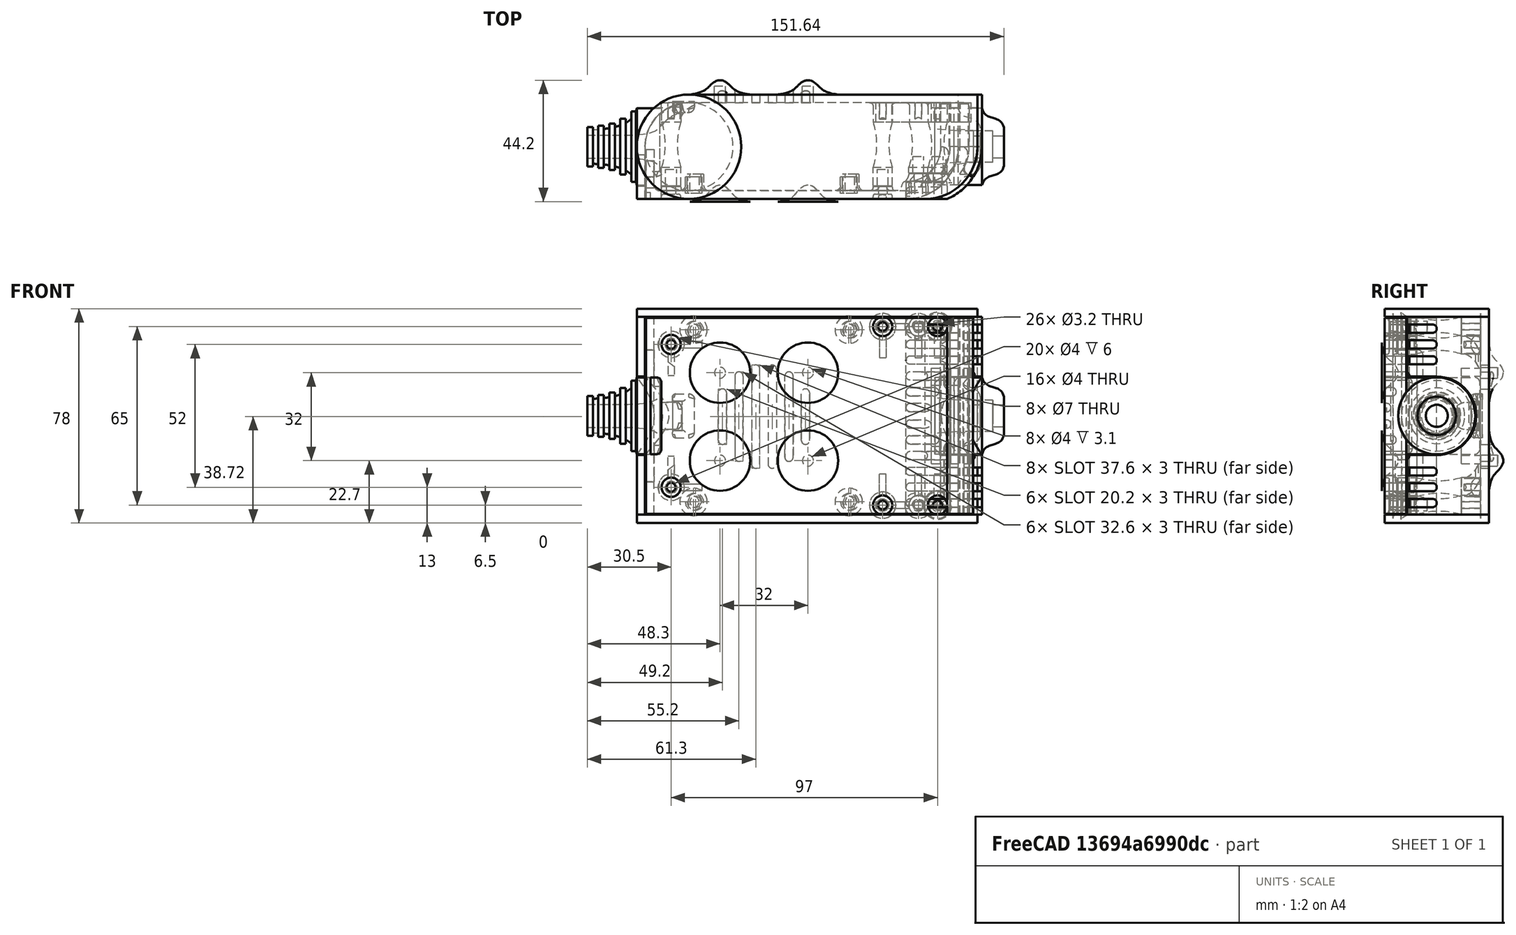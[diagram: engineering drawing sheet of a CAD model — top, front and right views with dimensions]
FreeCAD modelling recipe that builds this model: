
FCSTD DOCUMENT  (FreeCAD 0.19R0.19.2)
Label: enclosure_161
License: All rights reserved
LicenseURL: http://en.wikipedia.org/wiki/All_rights_reserved
objects: Part::Feature×140, Part::Revolution×140, Part::MultiFuse×120, Sketcher::SketchObject×67, Part::Extrusion×52, Part::Fillet×51, Part::Cut×51, Part::Cylinder×50, Part::Box×33, App::MeasureDistance×4
note: 704 computed .brp shape members not serialized (recipe doc carries the construction recipe); baked Part::Feature solids carry a one-line shape summary decoded from their .brp

FEATURE [Sketcher::SketchObject] Sketch  label="topSketch"
  FullyConstrained = true
  sketch-geometry (20):
    g0: LineSegment StartX=5.21097e-06 StartY=3 StartZ=0 EndX=5.21097e-06 EndY=19 EndZ=0
    g1: ArcOfCircle CenterX=19 CenterY=19 CenterZ=0 NormalX=0 NormalY=0 NormalZ=1 AngleXU=0 Radius=19 StartAngle=1.5708 EndAngle=3.14159
    g2: ArcOfCircle CenterX=19 CenterY=19 CenterZ=0 NormalX=0 NormalY=0 NormalZ=1 AngleXU=0 Radius=16 StartAngle=1.5708 EndAngle=3.14159
    g3: LineSegment StartX=114 StartY=35 StartZ=0 EndX=19 EndY=35 EndZ=0
    g4: LineSegment StartX=5.21097e-06 StartY=3 StartZ=0 EndX=5.21097e-06 EndY=0 EndZ=0
    g5: LineSegment StartX=3 StartY=0 StartZ=0 EndX=5.21097e-06 EndY=0 EndZ=0
    g6: LineSegment StartX=3 StartY=19 StartZ=0 EndX=3 EndY=0 EndZ=0
    g7: LineSegment StartX=19 StartY=38 StartZ=0 EndX=124 EndY=38 EndZ=0
    g8: Circle CenterX=119 CenterY=35 CenterZ=0 NormalX=0 NormalY=0 NormalZ=1 AngleXU=0 Radius=1
    g9: Circle CenterX=121 CenterY=35 CenterZ=0 NormalX=0 NormalY=0 NormalZ=1 AngleXU=0 Radius=1
    g10: Circle CenterX=121 CenterY=33 CenterZ=0 NormalX=0 NormalY=0 NormalZ=1 AngleXU=0 Radius=1
    g11: BSplineCurve PolesCount=3 KnotsCount=2 Degree=2 IsPeriodic=0
    g12: GeomPoint X=119 Y=35 Z=0
    g13: GeomPoint X=121 Y=33 Z=0
    g14: LineSegment StartX=119 StartY=35 StartZ=0 EndX=114 EndY=35 EndZ=0
    g15: ArcOfCircle CenterX=105 CenterY=19 CenterZ=0 NormalX=0 NormalY=0 NormalZ=1 AngleXU=0 Radius=19 StartAngle=5.7297 EndAngle=6.28319
    g16: ArcOfCircle CenterX=105 CenterY=19 CenterZ=0 NormalX=0 NormalY=0 NormalZ=1 AngleXU=0 Radius=16 StartAngle=5.60905 EndAngle=6.28319
    g17: LineSegment StartX=121 StartY=33 StartZ=0 EndX=121 EndY=19 EndZ=0
    g18: LineSegment StartX=124 StartY=38 StartZ=0 EndX=124 EndY=19 EndZ=0
    g19: LineSegment StartX=117.5 StartY=9.01251 StartZ=0 EndX=121.163 EndY=9.0125 EndZ=0
  constraints (46):
    c: Vertical(g0)
    c: Block(g0)
    c: Coincident(g1,g0)
    c: Block(g1)
    c: Coincident(g2,g1)
    c: Block(g2)
    c: Coincident(g3,g2)
    c: Horizontal(g3)
    c: Tangent(g3,g2)
    c: Coincident(g4,g0)
    c: Distance(g4) = 3
    c: Vertical(g4)
    c: Coincident(g5,g4)
    c: Horizontal(g5)
    c: Coincident(g6,g2)
    c: Coincident(g6,g5)
    c: Vertical(g6)
    c: Horizontal(g7)
    c: Distance(g7) = 105
    c: Coincident(g7,g1)
    c: Block(g3)
    c: Weight(g8) = 1
    c: Equal(g8,g9)
    c: Equal(g8,g10)
    c: InternalAlignment(g8,g11)
    c: InternalAlignment(g9,g11)
    c: InternalAlignment(g10,g11)
    c: InternalAlignment(g12,g11)
    c: InternalAlignment(g13,g11)
    c: Block(g11)
    c: Coincident(g14,g11)
    c: Coincident(g14,g3)
    c: Horizontal(g14)
    c: Block(g15)
    c: Coincident(g16,g15)
    c: Block(g16)
    c: Coincident(g17,g11)
    c: Coincident(g17,g16)
    c: Vertical(g17)
    c: Distance(g17) = 14
    c: Coincident(g18,g7)
    c: Coincident(g18,g15)
    c: Vertical(g18)
    c: Distance(g18) = 19
    c: Coincident(g19,g16)
    c: Coincident(g19,g15)
FEATURE [Sketcher::SketchObject] Sketch001  label="bottomSketch"
  FullyConstrained = true
  sketch-geometry (32):
    g0: LineSegment StartX=3.3 StartY=-6.03275e-07 StartZ=0 EndX=98 EndY=-6.03275e-07 EndZ=0
    g1: ArcOfCircle CenterX=98 CenterY=19 CenterZ=0 NormalX=0 NormalY=0 NormalZ=1 AngleXU=0 Radius=19 StartAngle=4.71239 EndAngle=5.71103
    g2: LineSegment StartX=6.3 StartY=8 StartZ=0 EndX=3.3 EndY=8 EndZ=0
    g3: LineSegment StartX=3.3 StartY=8 StartZ=0 EndX=3.3 EndY=-6.03275e-07 EndZ=0
    g4: ArcOfCircle CenterX=8.3 CenterY=5 CenterZ=0 NormalX=0 NormalY=0 NormalZ=1 AngleXU=0 Radius=2 StartAngle=3.14159 EndAngle=4.71239
    g5: LineSegment StartX=6.3 StartY=8 StartZ=0 EndX=6.3 EndY=5 EndZ=0
    g6: ArcOfCircle CenterX=98 CenterY=19 CenterZ=0 NormalX=0 NormalY=0 NormalZ=1 AngleXU=0 Radius=12.7 StartAngle=4.71239 EndAngle=6.28319
    g7: LineSegment StartX=94.7 StartY=3 StartZ=0 EndX=8.3 EndY=3 EndZ=0
    g8-g12: Circle x5 (B-spline internal-alignment scaffolding for g13; pole/knot coordinates omitted)
    g13: BSplineCurve PolesCount=5 KnotsCount=3 Degree=3 IsPeriodic=0
    g14: GeomPoint X=98 Y=6.3 Z=0
    g15: GeomPoint X=96.3938 Y=4.71946 Z=0
    g16: GeomPoint X=94.7 Y=3 Z=0
    g17-g23: Circle x7 (B-spline internal-alignment scaffolding for g24; pole/knot coordinates omitted)
    g24: BSplineCurve PolesCount=7 KnotsCount=5 Degree=3 IsPeriodic=0
    g25-g29: GeomPoint x5 (B-spline internal-alignment scaffolding for g24; pole/knot coordinates omitted)
    g30: ArcOfCircle CenterX=98 CenterY=19 CenterZ=0 NormalX=0 NormalY=0 NormalZ=1 AngleXU=0 Radius=15.7 StartAngle=5.81226 EndAngle=6.28319
    g31: LineSegment StartX=110.7 StartY=19 StartZ=0 EndX=113.7 EndY=19 EndZ=0
  constraints (41):
    c: Horizontal(g0)
    c: Coincident(g1,g0)
    c: Block(g1)
    c: Horizontal(g2)
    c: Distance(g2) = 3
    c: Coincident(g3,g2)
    c: Vertical(g3)
    c: Coincident(g3,g0)
    c: Block(g4)
    c: Block(g2)
    c: Coincident(g5,g2)
    c: Coincident(g5,g4)
    c: Vertical(g5)
    c: Coincident(g6,g1)
    c: Block(g6)
    c: Coincident(g7,g4)
    c: Horizontal(g7)
    c: Block(g0)
    c: Block(g7)
    c: Block(g3)
    c: Coincident(g13,g6)
    c: Weight(g8) = 1
    c: Equal(g8, g9-g12) x4
    c: Coincident(g13,g7)
    c: InternalAlignment(g8-g12 -> g13) x5
    c: InternalAlignment(g14,g13)
    c: InternalAlignment(g15,g13)
    c: InternalAlignment(g16,g13)
    c: Block(g13)
    c: Weight(g17) = 1
    c: Equal(g17, g18-g23) x6
    c: Coincident(g24,g1)
    c: InternalAlignment(g17-g23 -> g24) x7
    c: InternalAlignment(g25-g29 -> g24) x5
    c: Block(g24)
    c: Coincident(g30,g24)
    c: Coincident(g31,g6)
    c: Coincident(g31,g30)
    c: Horizontal(g31)
    c: Block(g31)
    c: Block(g30)
FEATURE [Part::Extrusion] Extrude  label="top"
  Base = -> Sketch
  Dir = (0,0,1)
  DirMode = 2
  FaceMakerClass = Part::FaceMakerBullseye
  LengthFwd = 72
  LengthRev = 0
  Solid = true
  Symmetric = false
FEATURE [Part::Extrusion] Extrude001  label="bottom"
  Base = -> Sketch001
  Dir = (0,0,1)
  DirMode = 2
  FaceMakerClass = Part::FaceMakerBullseye
  LengthFwd = 71.4
  LengthRev = 0
  Placement = pos=(0,0,0.3) rot=(0,0,1;0rad)
  Solid = true
  Symmetric = false
FEATURE [Sketcher::SketchObject] Sketch002  label="topSketch001"
  FullyConstrained = true
  sketch-geometry (6):
    g0: ArcOfCircle CenterX=19 CenterY=19 CenterZ=0 NormalX=0 NormalY=0 NormalZ=1 AngleXU=0 Radius=19 StartAngle=1.5708 EndAngle=3.14159
    g1: LineSegment StartX=5.22862e-06 StartY=19 StartZ=0 EndX=5.22862e-06 EndY=1.19904e-11 EndZ=0
    g2: LineSegment StartX=19 StartY=38 StartZ=0 EndX=124 EndY=38 EndZ=0
    g3: LineSegment StartX=5.22862e-06 StartY=1.19904e-11 StartZ=0 EndX=105 EndY=1.19904e-11 EndZ=0
    g4: ArcOfCircle CenterX=105 CenterY=19 CenterZ=0 NormalX=0 NormalY=0 NormalZ=1 AngleXU=0 Radius=19 StartAngle=4.71239 EndAngle=6.28319
    g5: LineSegment StartX=124 StartY=38 StartZ=0 EndX=124 EndY=19 EndZ=0
  constraints (16):
    c: Block(g0)
    c: Coincident(g1,g0)
    c: Vertical(g1)
    c: Horizontal(g2)
    c: Distance(g2) = 105
    c: Coincident(g2,g0)
    c: Distance(g1) = 19
    c: Coincident(g3,g1)
    c: Horizontal(g3)
    c: Distance(g3) = 105
    c: Block(g4)
    c: Coincident(g4,g3)
    c: Coincident(g5,g2)
    c: Coincident(g5,g4)
    c: Vertical(g5)
    c: Distance(g5) = 19
FEATURE [Part::Extrusion] Extrude002  label="sideA"
  Base = -> Sketch002
  Dir = (0,0,1)
  DirMode = 2
  FaceMakerClass = Part::FaceMakerBullseye
  LengthFwd = 3
  LengthRev = 0
  Placement = pos=(0,0,-3) rot=(0,0,1;0rad)
  Solid = true
  Symmetric = false
FEATURE [Sketcher::SketchObject] Sketch003  label="topSketch002"
  FullyConstrained = true
  sketch-geometry (6):
    g0: LineSegment StartX=19 StartY=38 StartZ=0 EndX=117 EndY=38 EndZ=0
    g1: ArcOfCircle CenterX=19 CenterY=19 CenterZ=0 NormalX=0 NormalY=0 NormalZ=1 AngleXU=0 Radius=19 StartAngle=1.5708 EndAngle=3.14159
    g2: LineSegment StartX=117 StartY=38 StartZ=0 EndX=117 EndY=19 EndZ=0
    g3: LineSegment StartX=98 StartY=1.0161e-12 StartZ=0 EndX=5.22862e-06 EndY=1.0161e-12 EndZ=0
    g4: LineSegment StartX=5.22862e-06 StartY=19 StartZ=0 EndX=5.22862e-06 EndY=1.0161e-12 EndZ=0
    g5: ArcOfCircle CenterX=98 CenterY=19 CenterZ=0 NormalX=0 NormalY=0 NormalZ=1 AngleXU=0 Radius=19 StartAngle=4.71239 EndAngle=6.28319
  constraints (16):
    c: Horizontal(g0)
    c: Distance(g0) = 98
    c: Coincident(g1,g0)
    c: Block(g1)
    c: Coincident(g2,g0)
    c: Vertical(g2)
    c: Distance(g2) = 19
    c: Horizontal(g3)
    c: Coincident(g4,g1)
    c: Vertical(g4)
    c: Coincident(g3,g4)
    c: Block(g3)
    c: Coincident(g5,g2)
    c: Coincident(g5,g3)
    c: Block(g0)
    c: Block(g5)
FEATURE [Sketcher::SketchObject] Sketch004
  FullyConstrained = true
  MapMode = 3
  Placement = pos=(0,0,0) rot=(1,0,0;1.5708rad)
  Support = -> [Extrude]
  sketch-geometry (8):
    g0: Circle CenterX=80.351 CenterY=-67.6202 CenterZ=0 NormalX=0 NormalY=0 NormalZ=1 AngleXU=0 Radius=2
    g1: Circle CenterX=80.351 CenterY=-67.6202 CenterZ=0 NormalX=0 NormalY=0 NormalZ=1 AngleXU=0 Radius=3
    g2: Circle CenterX=80.351 CenterY=-4.92017 CenterZ=0 NormalX=0 NormalY=0 NormalZ=1 AngleXU=0 Radius=2
    g3: Circle CenterX=80.351 CenterY=-4.92017 CenterZ=0 NormalX=0 NormalY=0 NormalZ=1 AngleXU=0 Radius=3
    g4: Circle CenterX=23.851 CenterY=-4.92017 CenterZ=0 NormalX=0 NormalY=0 NormalZ=1 AngleXU=0 Radius=2
    g5: Circle CenterX=23.851 CenterY=-4.92017 CenterZ=0 NormalX=0 NormalY=0 NormalZ=1 AngleXU=0 Radius=3
    g6: Circle CenterX=23.851 CenterY=-67.6202 CenterZ=0 NormalX=0 NormalY=0 NormalZ=1 AngleXU=0 Radius=2
    g7: Circle CenterX=23.851 CenterY=-67.6202 CenterZ=0 NormalX=0 NormalY=0 NormalZ=1 AngleXU=0 Radius=3
  constraints (8):
    c: Block(g3)
    c: Block(g2)
    c: Block(g1)
    c: Block(g0)
    c: Block(g6)
    c: Block(g7)
    c: Block(g4)
    c: Block(g5)
FEATURE [Part::Extrusion] Extrude004
  Base = -> Sketch004
  Dir = (0,-1,2e-16)
  DirMode = 2
  FaceMakerClass = Part::FaceMakerBullseye
  LengthFwd = 6
  LengthRev = 0
  Placement = pos=(0,9,0) rot=(0,0,1;0rad)
  Solid = true
  Symmetric = false
FEATURE [Sketcher::SketchObject] Sketch005
  FullyConstrained = true
  MapMode = 3
  Placement = pos=(0,0,0) rot=(1,0,0;1.5708rad)
  Support = -> [Extrude]
  sketch-geometry (8):
    g0: Circle CenterX=80.351 CenterY=-67.6202 CenterZ=0 NormalX=0 NormalY=0 NormalZ=1 AngleXU=0 Radius=3
    g1: Circle CenterX=80.351 CenterY=-4.92017 CenterZ=0 NormalX=0 NormalY=0 NormalZ=1 AngleXU=0 Radius=3
    g2: Circle CenterX=23.851 CenterY=-4.92017 CenterZ=0 NormalX=0 NormalY=0 NormalZ=1 AngleXU=0 Radius=3
    g3: Circle CenterX=23.851 CenterY=-67.6202 CenterZ=0 NormalX=0 NormalY=0 NormalZ=1 AngleXU=0 Radius=3
    g4: Circle CenterX=23.851 CenterY=-67.6202 CenterZ=0 NormalX=0 NormalY=0 NormalZ=1 AngleXU=0 Radius=5
    g5: Circle CenterX=80.351 CenterY=-67.6202 CenterZ=0 NormalX=0 NormalY=0 NormalZ=1 AngleXU=0 Radius=5
    g6: Circle CenterX=23.851 CenterY=-4.92017 CenterZ=0 NormalX=0 NormalY=0 NormalZ=1 AngleXU=0 Radius=5
    g7: Circle CenterX=80.351 CenterY=-4.92017 CenterZ=0 NormalX=0 NormalY=0 NormalZ=1 AngleXU=0 Radius=5
  constraints (8):
    c: Block(g1)
    c: Block(g0)
    c: Block(g3)
    c: Block(g2)
    c: Block(g5)
    c: Block(g4)
    c: Block(g6)
    c: Block(g7)
FEATURE [Part::Extrusion] Extrude005
  Base = -> Sketch005
  Dir = (0,-1,2e-16)
  DirMode = 2
  FaceMakerClass = Part::FaceMakerBullseye
  LengthFwd = 2
  LengthRev = 0
  Solid = true
  Symmetric = false
FEATURE [Sketcher::SketchObject] Sketch006
  FullyConstrained = true
  MapMode = 3
  Placement = pos=(0,0,0) rot=(1,0,0;1.5708rad)
  sketch-geometry (8):
    g0: Circle CenterX=80.351 CenterY=-67.6202 CenterZ=0 NormalX=0 NormalY=0 NormalZ=1 AngleXU=0 Radius=3
    g1: Circle CenterX=80.351 CenterY=-4.92017 CenterZ=0 NormalX=0 NormalY=0 NormalZ=1 AngleXU=0 Radius=3
    g2: Circle CenterX=23.851 CenterY=-4.92017 CenterZ=0 NormalX=0 NormalY=0 NormalZ=1 AngleXU=0 Radius=3
    g3: Circle CenterX=23.851 CenterY=-67.6202 CenterZ=0 NormalX=0 NormalY=0 NormalZ=1 AngleXU=0 Radius=3
    g4: Circle CenterX=23.851 CenterY=-67.6202 CenterZ=0 NormalX=0 NormalY=0 NormalZ=1 AngleXU=0 Radius=5
    g5: Circle CenterX=80.351 CenterY=-67.6202 CenterZ=0 NormalX=0 NormalY=0 NormalZ=1 AngleXU=0 Radius=5
    g6: Circle CenterX=23.851 CenterY=-4.92017 CenterZ=0 NormalX=0 NormalY=0 NormalZ=1 AngleXU=0 Radius=5
    g7: Circle CenterX=80.351 CenterY=-4.92017 CenterZ=0 NormalX=0 NormalY=0 NormalZ=1 AngleXU=0 Radius=5
  constraints (8):
    c: Block(g1)
    c: Block(g0)
    c: Block(g3)
    c: Block(g2)
    c: Block(g5)
    c: Block(g4)
    c: Block(g6)
    c: Block(g7)
FEATURE [Part::Extrusion] Extrude007
  Base = -> Sketch006
  Dir = (0,-1,2e-16)
  DirMode = 2
  FaceMakerClass = Part::FaceMakerBullseye
  LengthFwd = 2
  LengthRev = 0
  Solid = true
  Symmetric = false
FEATURE [Part::Fillet] Fillet
  Base = -> Extrude007
  Edges = 4 edges r=1.99: [Edge6,Edge12,Edge18,Edge24]
FEATURE [Part::Cut] Cut
  Base = -> Extrude005
  Placement = pos=(0,5,0) rot=(0,0,1;0rad)
  Tool = -> Fillet
FEATURE [Part::MultiFuse] Fusion  label="pCBScrews"
  Placement = pos=(-2.5,0,72.3) rot=(0,0,1;0rad)
  Shapes = -> [Extrude004,Cut]
FEATURE [App::MeasureDistance] Distance  label="Distance: 0.69 mm"
  Distance = 0.685967
  P1 = (24.0138,2.9647,0.3)
  P2 = (23.8901,3,-0.373787)
FEATURE [App::MeasureDistance] Distance001  label="Distance: 0.53 mm"
  Distance = 0.533607
  P1 = (80.2939,3,72.2334)
  P2 = (80.281,2.99661,71.7)
FEATURE [Part::Fillet] Fillet001
  Base = -> Extrude001
  Edges = 1 edges r=2.4: [Edge17]
FEATURE [Part::Fillet] Fillet002  label="bottom001"
  Base = -> Fillet001
  Edges = 1 edges r=2.4: [Edge36]
FEATURE [Part::Fillet] Fillet003  label="top001"
  Base = -> Extrude
  Edges = 1 edges r=2: [Edge1]
FEATURE [Sketcher::SketchObject] Sketch007
  FullyConstrained = true
  sketch-geometry (16):
    g0: LineSegment StartX=4 StartY=0 StartZ=0 EndX=4 EndY=2.4 EndZ=0
    g1: LineSegment StartX=4 StartY=2.4 StartZ=0 EndX=7 EndY=2.4 EndZ=0
    g2: LineSegment StartX=4 StartY=0 StartZ=0 EndX=5.7 EndY=0 EndZ=0
    g3: LineSegment StartX=5.7 StartY=0 StartZ=0 EndX=5.7 EndY=-5.6 EndZ=0
    g4-g8: Circle x5 (B-spline internal-alignment scaffolding for g9; pole/knot coordinates omitted)
    g9: BSplineCurve PolesCount=5 KnotsCount=3 Degree=3 IsPeriodic=0
    g10: GeomPoint X=7 Y=2.4 Z=0
    g11: GeomPoint X=10.4582 Y=-1.55472 Z=0
    g12: GeomPoint X=14 Y=-5.6 Z=0
    g13: LineSegment StartX=14 StartY=-5.6 StartZ=0 EndX=14 EndY=-14.1 EndZ=0
    g14: LineSegment StartX=14 StartY=-14.1 StartZ=0 EndX=6.5 EndY=-14.1 EndZ=0
    g15: LineSegment StartX=5.7 StartY=-5.6 StartZ=0 EndX=6.5 EndY=-14.1 EndZ=0
  constraints (28):
    c: Distance(g0) = 2.4
    c: Vertical(g0)
    c: Block(g0)
    c: Coincident(g1,g0)
    c: Horizontal(g1)
    c: Distance(g1) = 3
    c: Coincident(g2,g0)
    c: Horizontal(g2)
    c: Distance(g2) = 1.7
    c: Coincident(g3,g2)
    c: Vertical(g3)
    c: Distance(g3) = 5.6
    c: Coincident(g9,g1)
    c: Weight(g4) = 1
    c: Equal(g4, g5-g8) x4
    c: InternalAlignment(g4-g8 -> g9) x5
    c: InternalAlignment(g10,g9)
    c: InternalAlignment(g11,g9)
    c: InternalAlignment(g12,g9)
    c: Block(g9)
    c: Coincident(g13,g9)
    c: Vertical(g13)
    c: Distance(g13) = 8.5
    c: Coincident(g14,g13)
    c: Horizontal(g14)
    c: Distance(g14) = 7.5
    c: Coincident(g15,g3)
    c: Coincident(g15,g14)
FEATURE [Part::Feature] Face
  shape: bbox 10 x 16.5 x 2e-07 mm, 1 faces, 0 solids (baked)
FEATURE [Part::Revolution] Revolve  label="plugHousing"
  Angle = 360
  Axis = (0,1,0)
  Base = (0,0,0)
  FaceMakerClass = Part::FaceMakerBullseye
  Placement = pos=(0,0,36.15) rot=(0,0,1;0rad)
  Solid = false
  Source = -> Face
  Symmetric = false
FEATURE [Part::Feature] Face001
  shape: bbox 10 x 16.5 x 2e-07 mm, 1 faces, 0 solids (baked)
FEATURE [Part::Revolution] Revolve001  label="plugHousing001"
  Angle = 360
  Axis = (0,1,0)
  Base = (0,0,0)
  FaceMakerClass = Part::FaceMakerBullseye
  Placement = pos=(0,0,36.15) rot=(0,0,1;0rad)
  Solid = false
  Source = -> Face001
  Symmetric = false
FEATURE [Part::MultiFuse] Fusion001  label="plugHousing002"
  Placement = pos=(0,0,0) rot=(0,0,1;1.5708rad)
  Shapes = -> [Revolve001,Revolve]
FEATURE [Part::Feature] Face002
  shape: bbox 10 x 16.5 x 2e-07 mm, 1 faces, 0 solids (baked)
FEATURE [Part::Revolution] Revolve003  label="plugHousing005"
  Angle = 360
  Axis = (0,1,0)
  Base = (0,0,0)
  FaceMakerClass = Part::FaceMakerBullseye
  Placement = pos=(0,0,36.15) rot=(0,0,1;0rad)
  Solid = false
  Source = -> Face002
  Symmetric = false
FEATURE [Part::Feature] Face003
  shape: bbox 10 x 16.5 x 2e-07 mm, 1 faces, 0 solids (baked)
FEATURE [Part::Revolution] Revolve002  label="plugHousing003"
  Angle = 360
  Axis = (0,1,0)
  Base = (0,0,0)
  FaceMakerClass = Part::FaceMakerBullseye
  Placement = pos=(0,0,36.15) rot=(0,0,1;0rad)
  Solid = false
  Source = -> Face003
  Symmetric = false
FEATURE [Part::MultiFuse] Fusion002  label="plugHousing004"
  Placement = pos=(0,0,0) rot=(0,0,1;1.5708rad)
  Shapes = -> [Revolve002,Revolve003]
FEATURE [Part::MultiFuse] Fusion003  label="plugHousing006"
  Placement = pos=(0,19,0) rot=(0,0,1;3.14159rad)
  Shapes = -> [Fusion002,Fusion001]
FEATURE [Part::Feature] Face004
  shape: bbox 10 x 16.5 x 2e-07 mm, 1 faces, 0 solids (baked)
FEATURE [Part::Revolution] Revolve006  label="plugHousing010"
  Angle = 360
  Axis = (0,1,0)
  Base = (0,0,0)
  FaceMakerClass = Part::FaceMakerBullseye
  Placement = pos=(0,0,36.15) rot=(0,0,1;0rad)
  Solid = false
  Source = -> Face004
  Symmetric = false
FEATURE [Part::Feature] Face005
  shape: bbox 10 x 16.5 x 2e-07 mm, 1 faces, 0 solids (baked)
FEATURE [Part::Revolution] Revolve007  label="plugHousing011"
  Angle = 360
  Axis = (0,1,0)
  Base = (0,0,0)
  FaceMakerClass = Part::FaceMakerBullseye
  Placement = pos=(0,0,36.15) rot=(0,0,1;0rad)
  Solid = false
  Source = -> Face005
  Symmetric = false
FEATURE [Part::Feature] Face006
  shape: bbox 10 x 16.5 x 2e-07 mm, 1 faces, 0 solids (baked)
FEATURE [Part::Revolution] Revolve004  label="plugHousing007"
  Angle = 360
  Axis = (0,1,0)
  Base = (0,0,0)
  FaceMakerClass = Part::FaceMakerBullseye
  Placement = pos=(0,0,36.15) rot=(0,0,1;0rad)
  Solid = false
  Source = -> Face006
  Symmetric = false
FEATURE [Part::MultiFuse] Fusion004  label="plugHousing009"
  Placement = pos=(0,0,0) rot=(0,0,1;1.5708rad)
  Shapes = -> [Revolve004,Revolve007]
FEATURE [Part::Feature] Face007
  shape: bbox 10 x 16.5 x 2e-07 mm, 1 faces, 0 solids (baked)
FEATURE [Part::Revolution] Revolve005  label="plugHousing008"
  Angle = 360
  Axis = (0,1,0)
  Base = (0,0,0)
  FaceMakerClass = Part::FaceMakerBullseye
  Placement = pos=(0,0,36.15) rot=(0,0,1;0rad)
  Solid = false
  Source = -> Face007
  Symmetric = false
FEATURE [Part::MultiFuse] Fusion005  label="plugHousing012"
  Placement = pos=(0,0,0) rot=(0,0,1;1.5708rad)
  Shapes = -> [Revolve006,Revolve005]
FEATURE [Part::MultiFuse] Fusion006  label="plugHousing013"
  Placement = pos=(0,19,0) rot=(0,0,1;3.14159rad)
  Shapes = -> [Fusion005,Fusion004]
FEATURE [Part::MultiFuse] Fusion007  label="plugHousing014"
  Placement = pos=(122.621,0,-0.15) rot=(0,0,1;0rad)
  Shapes = -> [Fusion003,Fusion006]
FEATURE [Part::Cylinder] Cylinder002
  Angle = 360
  AttacherType = Attacher::AttachEngine3D
  Height = 20
  Placement = pos=(0,0,36.15) rot=(0,0,1;0rad)
  Radius = 4
FEATURE [Part::Cylinder] Cylinder003
  Angle = 360
  AttacherType = Attacher::AttachEngine3D
  Height = 10
  Placement = pos=(0,0,36.15) rot=(0,0,1;0rad)
  Radius = 4
FEATURE [Part::MultiFuse] Fusion009  label="removeToCreateHoleForPlugHousing"
  Placement = pos=(70,19,36.15) rot=(0,1,0;1.5708rad)
  Shapes = -> [Cylinder002,Cylinder003]
FEATURE [Part::Cylinder] Cylinder004
  Angle = 360
  AttacherType = Attacher::AttachEngine3D
  Height = 20
  Placement = pos=(0,0,36.15) rot=(0,0,1;0rad)
  Radius = 4
FEATURE [Part::Cylinder] Cylinder005
  Angle = 360
  AttacherType = Attacher::AttachEngine3D
  Height = 10
  Placement = pos=(0,0,36.15) rot=(0,0,1;0rad)
  Radius = 4
FEATURE [Part::MultiFuse] Fusion010  label="removeToCreateHoleForPlugHousing001"
  Placement = pos=(70,19,36.15) rot=(0,1,0;1.5708rad)
  Shapes = -> [Cylinder004,Cylinder005]
FEATURE [Part::Cut] Cut001
  Base = -> Fillet003
  Tool = -> Fusion010
FEATURE [Part::Cut] Cut002  label="Bottom"
  Base = -> Fillet002
  Tool = -> Fusion009
FEATURE [Part::Feature] Face008
  shape: bbox 10 x 16.5 x 2e-07 mm, 1 faces, 0 solids (baked)
FEATURE [Part::Revolution] Revolve011  label="plugHousing021"
  Angle = 360
  Axis = (0,1,0)
  Base = (0,0,0)
  FaceMakerClass = Part::FaceMakerBullseye
  Placement = pos=(0,0,36.15) rot=(0,0,1;0rad)
  Solid = false
  Source = -> Face008
  Symmetric = false
FEATURE [Part::Feature] Face009
  shape: bbox 10 x 16.5 x 2e-07 mm, 1 faces, 0 solids (baked)
FEATURE [Part::Revolution] Revolve012  label="plugHousing022"
  Angle = 360
  Axis = (0,1,0)
  Base = (0,0,0)
  FaceMakerClass = Part::FaceMakerBullseye
  Placement = pos=(0,0,36.15) rot=(0,0,1;0rad)
  Solid = false
  Source = -> Face009
  Symmetric = false
FEATURE [Part::Feature] Face010 .. Face013  x4 (patterned run collapsed; names and placements below)
  shape: bbox 10 x 16.5 x 2e-07 mm, 1 faces, 0 solids (baked)
FEATURE [Part::Revolution] Revolve015  label="plugHousing027"
  Angle = 360
  Axis = (0,1,0)
  Base = (0,0,0)
  FaceMakerClass = Part::FaceMakerBullseye
  Placement = pos=(0,0,36.15) rot=(0,0,1;0rad)
  Solid = false
  Source = -> Face013
  Symmetric = false
FEATURE [Part::Feature] Face014
  shape: bbox 10 x 16.5 x 2e-07 mm, 1 faces, 0 solids (baked)
FEATURE [Part::Feature] Face015
  shape: bbox 10 x 16.5 x 2e-07 mm, 1 faces, 0 solids (baked)
FEATURE [Part::Feature] Face016
  shape: bbox 10 x 16.5 x 2e-07 mm, 1 faces, 0 solids (baked)
FEATURE [Part::Revolution] Revolve019  label="plugHousing033"
  Angle = 360
  Axis = (0,1,0)
  Base = (0,0,0)
  FaceMakerClass = Part::FaceMakerBullseye
  Placement = pos=(0,0,36.15) rot=(0,0,1;0rad)
  Solid = false
  Source = -> Face016
  Symmetric = false
FEATURE [Part::Feature] Face017
  shape: bbox 10 x 16.5 x 2e-07 mm, 1 faces, 0 solids (baked)
FEATURE [Part::Revolution] Revolve020  label="plugHousing034"
  Angle = 360
  Axis = (0,1,0)
  Base = (0,0,0)
  FaceMakerClass = Part::FaceMakerBullseye
  Placement = pos=(0,0,36.15) rot=(0,0,1;0rad)
  Solid = false
  Source = -> Face017
  Symmetric = false
FEATURE [Part::Feature] Face018
  shape: bbox 10 x 16.5 x 2e-07 mm, 1 faces, 0 solids (baked)
FEATURE [Part::Revolution] Revolve016  label="plugHousing030"
  Angle = 360
  Axis = (0,1,0)
  Base = (0,0,0)
  FaceMakerClass = Part::FaceMakerBullseye
  Placement = pos=(0,0,36.15) rot=(0,0,1;0rad)
  Solid = false
  Source = -> Face018
  Symmetric = false
FEATURE [Part::MultiFuse] Fusion020  label="plugHousing038"
  Placement = pos=(0,0,0) rot=(0,0,1;1.5708rad)
  Shapes = -> [Revolve016,Revolve020]
FEATURE [Part::Feature] Face019
  shape: bbox 10 x 16.5 x 2e-07 mm, 1 faces, 0 solids (baked)
FEATURE [Part::Feature] Face020
  shape: bbox 10 x 16.5 x 2e-07 mm, 1 faces, 0 solids (baked)
FEATURE [Part::Revolution] Revolve017  label="plugHousing031"
  Angle = 360
  Axis = (0,1,0)
  Base = (0,0,0)
  FaceMakerClass = Part::FaceMakerBullseye
  Placement = pos=(0,0,36.15) rot=(0,0,1;0rad)
  Solid = false
  Source = -> Face020
  Symmetric = false
FEATURE [Part::MultiFuse] Fusion021  label="plugHousing039"
  Placement = pos=(0,0,0) rot=(0,0,1;1.5708rad)
  Shapes = -> [Revolve019,Revolve017]
FEATURE [Part::MultiFuse] Fusion023  label="plugHousing041"
  Placement = pos=(0,19,0) rot=(0,0,1;3.14159rad)
  Shapes = -> [Fusion021,Fusion020]
FEATURE [Part::Revolution] Revolve022  label="plugHousing043"
  Angle = 360
  Axis = (0,1,0)
  Base = (0,0,0)
  FaceMakerClass = Part::FaceMakerBullseye
  Placement = pos=(0,0,36.15) rot=(0,0,1;0rad)
  Solid = false
  Source = -> Face019
  Symmetric = false
FEATURE [Part::Feature] Face021
  shape: bbox 10 x 16.5 x 2e-07 mm, 1 faces, 0 solids (baked)
FEATURE [Part::Revolution] Revolve023  label="plugHousing044"
  Angle = 360
  Axis = (0,1,0)
  Base = (0,0,0)
  FaceMakerClass = Part::FaceMakerBullseye
  Placement = pos=(0,0,36.15) rot=(0,0,1;0rad)
  Solid = false
  Source = -> Face021
  Symmetric = false
FEATURE [Part::Feature] Face022
  shape: bbox 10 x 16.5 x 2e-07 mm, 1 faces, 0 solids (baked)
FEATURE [Part::Revolution] Revolve018  label="plugHousing032"
  Angle = 360
  Axis = (0,1,0)
  Base = (0,0,0)
  FaceMakerClass = Part::FaceMakerBullseye
  Placement = pos=(0,0,36.15) rot=(0,0,1;0rad)
  Solid = false
  Source = -> Face022
  Symmetric = false
FEATURE [Part::MultiFuse] Fusion022  label="plugHousing040"
  Placement = pos=(0,0,0) rot=(0,0,1;1.5708rad)
  Shapes = -> [Revolve018,Revolve023]
FEATURE [Part::Feature] Face023
  shape: bbox 10 x 16.5 x 2e-07 mm, 1 faces, 0 solids (baked)
FEATURE [Part::Revolution] Revolve021  label="plugHousing035"
  Angle = 360
  Axis = (0,1,0)
  Base = (0,0,0)
  FaceMakerClass = Part::FaceMakerBullseye
  Placement = pos=(0,0,36.15) rot=(0,0,1;0rad)
  Solid = false
  Source = -> Face023
  Symmetric = false
FEATURE [Part::MultiFuse] Fusion018  label="plugHousing036"
  Placement = pos=(0,0,0) rot=(0,0,1;1.5708rad)
  Shapes = -> [Revolve022,Revolve021]
FEATURE [Part::MultiFuse] Fusion019  label="plugHousing037"
  Placement = pos=(0,19,0) rot=(0,0,1;3.14159rad)
  Shapes = -> [Fusion018,Fusion022]
FEATURE [Part::MultiFuse] Fusion024  label="plugHousing042"
  Placement = pos=(122.621,0,-0.15) rot=(0,0,1;0rad)
  Shapes = -> [Fusion023,Fusion019]
FEATURE [Part::Cylinder] Cylinder006
  Angle = 360
  AttacherType = Attacher::AttachEngine3D
  Height = 20
  Placement = pos=(0,0,36.15) rot=(0,0,1;0rad)
  Radius = 14.3
FEATURE [Part::Cylinder] Cylinder007
  Angle = 360
  AttacherType = Attacher::AttachEngine3D
  Height = 10
  Placement = pos=(0,0,36.15) rot=(0,0,1;0rad)
  Radius = 4
FEATURE [Part::MultiFuse] Fusion026  label="removeToCreteHoleForPlugHousing"
  Placement = pos=(70,19,36) rot=(0,1,0;1.5708rad)
  Shapes = -> [Cylinder006,Cylinder007]
FEATURE [Part::Box] Box001  label="Cube001"
  AttacherType = Attacher::AttachEngine3D
  Height = 28
  Length = 3
  Placement = pos=(110.7,19,22) rot=(0,0,1;0rad)
  Width = 15.7
FEATURE [Part::Cut] Cut003  label="top002"
  Base = -> Cut001
  Tool = -> Fusion007
FEATURE [Part::Revolution] Revolve008  label="plugHousing015"
  Angle = 360
  Axis = (0,1,0)
  Base = (0,0,0)
  FaceMakerClass = Part::FaceMakerBullseye
  Placement = pos=(0,0,36.15) rot=(0,0,1;0rad)
  Solid = false
  Source = -> Face010
  Symmetric = false
FEATURE [Part::MultiFuse] Fusion013  label="plugHousing020"
  Placement = pos=(0,0,0) rot=(0,0,1;1.5708rad)
  Shapes = -> [Revolve008,Revolve012]
FEATURE [Part::Cut] Cut004  label="top003"
  Base = -> Cut003
  Placement = pos=(1,0,0) rot=(0,0,1;0rad)
  Tool = -> Fusion026
FEATURE [Part::Cylinder] Cylinder008
  Angle = 360
  AttacherType = Attacher::AttachEngine3D
  Height = 20
  Placement = pos=(0,0,36.15) rot=(0,0,1;0rad)
  Radius = 10.3
FEATURE [Part::Cylinder] Cylinder009
  Angle = 360
  AttacherType = Attacher::AttachEngine3D
  Height = 10
  Placement = pos=(0,0,36.15) rot=(0,0,1;0rad)
  Radius = 4
FEATURE [Part::MultiFuse] Fusion027  label="removeToCreteHoleForPlugHousing001"
  Placement = pos=(70,19,36) rot=(0,1,0;1.5708rad)
  Shapes = -> [Cylinder008,Cylinder009]
FEATURE [Part::Cut] Cut005  label="plugHousingTab"
  Base = -> Box001
  Tool = -> Fusion027
FEATURE [Part::MultiFuse] Fusion028  label="plugHousing045"
  Shapes = -> [Fusion024,Cut005]
FEATURE [Part::Box] Box002  label="Cube002"
  AttacherType = Attacher::AttachEngine3D
  Height = 28.8
  Length = 3
  Placement = pos=(107.3,28,21.6) rot=(0,0,1;0rad)
  Width = 7
FEATURE [Part::Box] Box003  label="Cube003"
  AttacherType = Attacher::AttachEngine3D
  Height = 3
  Length = 6.4
  Placement = pos=(107.3,28,18.6) rot=(0,0,1;0rad)
  Width = 7
FEATURE [Part::Box] Box004  label="Cube004"
  AttacherType = Attacher::AttachEngine3D
  Height = 3
  Length = 6.4
  Placement = pos=(107.3,28,50.4) rot=(0,0,1;0rad)
  Width = 7
FEATURE [Part::MultiFuse] Fusion029  label="plugHousingBracketHolder"
  Shapes = -> [Box004,Box002,Box003]
FEATURE [Part::Cylinder] Cylinder010
  Angle = 360
  AttacherType = Attacher::AttachEngine3D
  Height = 20
  Placement = pos=(0,0,36.15) rot=(0,0,1;0rad)
  Radius = 14.3
FEATURE [Part::Cylinder] Cylinder011
  Angle = 360
  AttacherType = Attacher::AttachEngine3D
  Height = 10
  Placement = pos=(0,0,36.15) rot=(0,0,1;0rad)
  Radius = 4
FEATURE [Part::MultiFuse] Fusion030  label="removeToCreteHoleForPlugHousing002"
  Placement = pos=(70,19,36) rot=(0,1,0;1.5708rad)
  Shapes = -> [Cylinder010,Cylinder011]
FEATURE [Part::Cut] Cut006  label="plugHousingBracketHolder001"
  Base = -> Fusion029
  Tool = -> Fusion030
FEATURE [Part::Cylinder] Cylinder012
  Angle = 360
  AttacherType = Attacher::AttachEngine3D
  Height = 20
  Placement = pos=(0,0,36.15) rot=(0,0,1;0rad)
  Radius = 7
FEATURE [Part::Cylinder] Cylinder013
  Angle = 360
  AttacherType = Attacher::AttachEngine3D
  Height = 10
  Placement = pos=(0,0,36.15) rot=(0,0,1;0rad)
  Radius = 4
FEATURE [Part::MultiFuse] Fusion032  label="removeToCreteHoleForPlugHousing003"
  Placement = pos=(70,19,36) rot=(0,1,0;1.5708rad)
  Shapes = -> [Cylinder012,Cylinder013]
FEATURE [Part::Cut] Cut007  label="bottom002"
  Base = -> Cut002
  Tool = -> Fusion032
FEATURE [Sketcher::SketchObject] Sketch008
  FullyConstrained = true
  sketch-geometry (54):
    g0: LineSegment StartX=-4.2 StartY=0 StartZ=0 EndX=-6.2 EndY=0 EndZ=0
    g1: LineSegment StartX=-14 StartY=-18 StartZ=0 EndX=-14 EndY=-26.5 EndZ=0
    g2: LineSegment StartX=-4.2 StartY=0 StartZ=0 EndX=-4.2 EndY=-13.4877 EndZ=0
    g3: Circle CenterX=-4.2 CenterY=-13.4877 CenterZ=0 NormalX=0 NormalY=0 NormalZ=1 AngleXU=0 Radius=1
    g4: Circle CenterX=-4.2 CenterY=-26.5 CenterZ=0 NormalX=0 NormalY=0 NormalZ=1 AngleXU=0 Radius=1
    g5: Circle CenterX=-8.2 CenterY=-26.5 CenterZ=0 NormalX=0 NormalY=0 NormalZ=1 AngleXU=0 Radius=1
    g6: BSplineCurve PolesCount=3 KnotsCount=2 Degree=2 IsPeriodic=0
    g7: GeomPoint X=-4.2 Y=-13.4877 Z=0
    g8: GeomPoint X=-8.2 Y=-26.5 Z=0
    g9: LineSegment StartX=-14 StartY=-26.5 StartZ=0 EndX=-8.2 EndY=-26.5 EndZ=0
    g10: LineSegment StartX=-10.15 StartY=-12 StartZ=0 EndX=-10.15 EndY=-14 EndZ=0
    g11: LineSegment StartX=-12.8401 StartY=-16 StartZ=0 EndX=-10.1571 EndY=-16 EndZ=0
    g12: LineSegment StartX=-10.15 StartY=-14 StartZ=0 EndX=-8.70761 EndY=-14 EndZ=0
    g13: LineSegment StartX=-12.8401 StartY=-16 StartZ=0 EndX=-12.8401 EndY=-17.6958 EndZ=0
    g14: LineSegment StartX=-10.15 StartY=-12 StartZ=0 EndX=-7.79258 EndY=-12 EndZ=0
    g15: Circle CenterX=-6.2215 CenterY=-2 CenterZ=0 NormalX=0 NormalY=0 NormalZ=1 AngleXU=0 Radius=1
    g16: Circle CenterX=-6.22762 CenterY=-2.58724 CenterZ=0 NormalX=0 NormalY=0 NormalZ=1 AngleXU=0 Radius=1
    g17: Circle CenterX=-6.32538 CenterY=-4 CenterZ=0 NormalX=0 NormalY=0 NormalZ=1 AngleXU=0 Radius=1
    g18: BSplineCurve PolesCount=3 KnotsCount=2 Degree=2 IsPeriodic=0
    g19: GeomPoint X=-6.2215 Y=-2 Z=0
    g20: GeomPoint X=-6.32538 Y=-4 Z=0
    g21: Circle CenterX=-6.48644 CenterY=-5.99526 CenterZ=0 NormalX=0 NormalY=0 NormalZ=1 AngleXU=0 Radius=1
    g22: Circle CenterX=-6.58486 CenterY=-6.99526 CenterZ=0 NormalX=0 NormalY=0 NormalZ=1 AngleXU=0 Radius=1
    g23: Circle CenterX=-6.77343 CenterY=-8 CenterZ=0 NormalX=0 NormalY=0 NormalZ=1 AngleXU=0 Radius=1
    g24: BSplineCurve PolesCount=3 KnotsCount=2 Degree=2 IsPeriodic=0
    g25: GeomPoint X=-6.48644 Y=-5.99526 Z=0
    g26: GeomPoint X=-6.77343 Y=-8 Z=0
    g27: Circle CenterX=-7.19003 CenterY=-10 CenterZ=0 NormalX=0 NormalY=0 NormalZ=1 AngleXU=0 Radius=1
    g28: Circle CenterX=-7.44407 CenterY=-11.0915 CenterZ=0 NormalX=0 NormalY=0 NormalZ=1 AngleXU=0 Radius=1
    g29: Circle CenterX=-7.79258 CenterY=-12 CenterZ=0 NormalX=0 NormalY=0 NormalZ=1 AngleXU=0 Radius=1
    g30: BSplineCurve PolesCount=3 KnotsCount=2 Degree=2 IsPeriodic=0
    g31: GeomPoint X=-7.19003 Y=-10 Z=0
    g32: GeomPoint X=-7.79258 Y=-12 Z=0
    g33: Circle CenterX=-8.70761 CenterY=-14 CenterZ=0 NormalX=0 NormalY=0 NormalZ=1 AngleXU=0 Radius=1
    g34: Circle CenterX=-9.33087 CenterY=-15.1837 CenterZ=0 NormalX=0 NormalY=0 NormalZ=1 AngleXU=0 Radius=1
    g35: Circle CenterX=-10.1571 CenterY=-16 CenterZ=0 NormalX=0 NormalY=0 NormalZ=1 AngleXU=0 Radius=1
    g36: BSplineCurve PolesCount=3 KnotsCount=2 Degree=2 IsPeriodic=0
    g37: GeomPoint X=-8.70761 Y=-14 Z=0
    g38: GeomPoint X=-10.1571 Y=-16 Z=0
    g39: Circle CenterX=-12.8401 CenterY=-17.6958 CenterZ=0 NormalX=0 NormalY=0 NormalZ=1 AngleXU=0 Radius=1
    g40: Circle CenterX=-13.3521 CenterY=-17.9027 CenterZ=0 NormalX=0 NormalY=0 NormalZ=1 AngleXU=0 Radius=1
    g41: Circle CenterX=-14 CenterY=-18 CenterZ=0 NormalX=0 NormalY=0 NormalZ=1 AngleXU=0 Radius=1
    g42: BSplineCurve PolesCount=3 KnotsCount=2 Degree=2 IsPeriodic=0
    g43: GeomPoint X=-12.8401 Y=-17.6958 Z=0
    g44: GeomPoint X=-14 Y=-18 Z=0
    g45: LineSegment StartX=-6.2 StartY=0 StartZ=0 EndX=-7.2 EndY=0 EndZ=0
    g46: LineSegment StartX=-7.2 StartY=0 StartZ=0 EndX=-7.2 EndY=-2 EndZ=0
    g47: LineSegment StartX=-7.2 StartY=-2 StartZ=0 EndX=-6.2215 EndY=-2 EndZ=0
    g48: LineSegment StartX=-6.32538 StartY=-4 StartZ=0 EndX=-7.65538 EndY=-4 EndZ=0
    g49: LineSegment StartX=-7.65538 StartY=-4 StartZ=0 EndX=-7.65538 EndY=-5.99526 EndZ=0
    g50: LineSegment StartX=-7.65538 StartY=-5.99526 StartZ=0 EndX=-6.48644 EndY=-5.99526 EndZ=0
    g51: LineSegment StartX=-6.77343 StartY=-8 StartZ=0 EndX=-8.43343 EndY=-8 EndZ=0
    g52: LineSegment StartX=-8.43343 StartY=-8 StartZ=0 EndX=-8.43343 EndY=-10 EndZ=0
    g53: LineSegment StartX=-8.43343 StartY=-10 StartZ=0 EndX=-7.19003 EndY=-10 EndZ=0
  constraints (112):
    c: Horizontal(g0)
    c: Distance(g0) = 2
    c: Block(g0)
    c: Vertical(g1)
    c: Coincident(g2,g0)
    c: Vertical(g2)
    c: Block(g2)
    c: Coincident(g6,g2)
    c: Weight(g3) = 1
    c: Equal(g3,g4)
    c: Equal(g3,g5)
    c: InternalAlignment(g3,g6)
    c: InternalAlignment(g4,g6)
    c: InternalAlignment(g5,g6)
    c: InternalAlignment(g7,g6)
    c: InternalAlignment(g8,g6)
    c: Block(g6)
    c: Coincident(g9,g1)
    c: Coincident(g9,g6)
    c: Horizontal(g9)
    c: Vertical(g10)
    c: Block(g10)
    c: Horizontal(g11)
    c: Block(g11)
    c: Coincident(g12,g10)
    c: Horizontal(g12)
    c: Block(g12)
    c: Coincident(g13,g11)
    c: Vertical(g13)
    c: Block(g13)
    c: Coincident(g14,g10)
    c: Horizontal(g14)
    c: Block(g14)
    c: Block(g9)
    c: Block(g1)
    c: Weight(g15) = 1
    c: Equal(g15,g16)
    c: Equal(g15,g17)
    c: InternalAlignment(g15,g18)
    c: InternalAlignment(g16,g18)
    c: InternalAlignment(g17,g18)
    c: InternalAlignment(g19,g18)
    c: InternalAlignment(g20,g18)
    c: Weight(g21) = 1
    c: Equal(g21,g22)
    c: Equal(g21,g23)
    c: InternalAlignment(g21,g24)
    c: InternalAlignment(g22,g24)
    c: InternalAlignment(g23,g24)
    c: InternalAlignment(g25,g24)
    c: InternalAlignment(g26,g24)
    c: Weight(g27) = 1
    c: Equal(g27,g28)
    c: Equal(g27,g29)
    c: Coincident(g30,g14)
    c: InternalAlignment(g27,g30)
    c: InternalAlignment(g28,g30)
    c: InternalAlignment(g29,g30)
    c: InternalAlignment(g31,g30)
    c: InternalAlignment(g32,g30)
    c: Coincident(g36,g12)
    c: Weight(g33) = 1
    c: Equal(g33,g34)
    c: Equal(g33,g35)
    c: Coincident(g36,g11)
    c: InternalAlignment(g33,g36)
    c: InternalAlignment(g34,g36)
    c: InternalAlignment(g35,g36)
    c: InternalAlignment(g37,g36)
    c: InternalAlignment(g38,g36)
    c: Coincident(g42,g13)
    c: Weight(g39) = 1
    c: Equal(g39,g40)
    c: Equal(g39,g41)
    c: Coincident(g42,g1)
    c: InternalAlignment(g39,g42)
    c: InternalAlignment(g40,g42)
    c: InternalAlignment(g41,g42)
    c: InternalAlignment(g43,g42)
    c: InternalAlignment(g44,g42)
    c: Block(g18)
    c: Block(g24)
    c: Block(g30)
    c: Block(g36)
    c: Block(g42)
    c: Horizontal(g45)
    c: Coincident(g45,g0)
    c: Vertical(g46)
    c: Coincident(g46,g45)
    c: Coincident(g47,g46)
    c: Coincident(g47,g18)
    c: Horizontal(g47)
    c: Block(g46)
    c: Coincident(g48,g18)
    c: Horizontal(g48)
    c: Distance(g48) = 1.33
    c: Vertical(g49)
    c: Coincident(g49,g48)
    c: Coincident(g50,g49)
    c: Coincident(g50,g24)
    c: Horizontal(g50)
    c: Tangent(g50,g22)
    c: Horizontal(g51)
    c: Coincident(g51,g24)
    c: Block(g51)
    c: Vertical(g52)
    c: Block(g52)
    c: Coincident(g52,g51)
    c: Coincident(g53,g52)
    c: Coincident(g53,g30)
    c: Horizontal(g53)
    c: Distance(g1) = 8.5
FEATURE [Part::Feature] Face024
  shape: bbox 9.8 x 26.5 x 2e-07 mm, 1 faces, 0 solids (baked)
FEATURE [Part::Revolution] Revolve024
  Angle = 360
  Axis = (0,1,0)
  Base = (0,0,0)
  FaceMakerClass = Part::FaceMakerBullseye
  Placement = pos=(0,0,0) rot=(0,0,1;1.5708rad)
  Solid = false
  Source = -> Face024
  Symmetric = false
FEATURE [Part::Feature] Face025
  shape: bbox 9.8 x 26.5 x 2e-07 mm, 1 faces, 0 solids (baked)
FEATURE [Part::Revolution] Revolve025
  Angle = 360
  Axis = (0,1,0)
  Base = (0,0,0)
  FaceMakerClass = Part::FaceMakerBullseye
  Placement = pos=(0,0,0) rot=(0,0,1;1.5708rad)
  Solid = false
  Source = -> Face025
  Symmetric = false
FEATURE [Part::MultiFuse] Fusion033
  Placement = pos=(-18,19,36) rot=(0,0,1;0rad)
  Shapes = -> [Revolve025,Revolve024]
FEATURE [Part::Cylinder] Cylinder014
  Angle = 360
  AttacherType = Attacher::AttachEngine3D
  Height = 20
  Placement = pos=(0,0,36.15) rot=(0,0,1;0rad)
  Radius = 14.3
FEATURE [Part::Cylinder] Cylinder015
  Angle = 360
  AttacherType = Attacher::AttachEngine3D
  Height = 10
  Placement = pos=(0,0,36.15) rot=(0,0,1;0rad)
  Radius = 4
FEATURE [Part::MultiFuse] Fusion034  label="removeToCreteHoleForPlugHousing004"
  Placement = pos=(-42,19,36) rot=(0,1,0;1.5708rad)
  Shapes = -> [Cylinder014,Cylinder015]
FEATURE [Part::Cut] Cut008  label="top004"
  Base = -> Cut004
  Placement = pos=(-1,0,0) rot=(0,0,1;0rad)
  Tool = -> Fusion034
FEATURE [Part::Box] Box005  label="Cube005"
  AttacherType = Attacher::AttachEngine3D
  Height = 28
  Length = 3
  Placement = pos=(110.7,19,22) rot=(0,0,1;0rad)
  Width = 15.7
FEATURE [Part::Cylinder] Cylinder016
  Angle = 360
  AttacherType = Attacher::AttachEngine3D
  Height = 10
  Placement = pos=(0,0,36.15) rot=(0,0,1;0rad)
  Radius = 4
FEATURE [Part::Cylinder] Cylinder017
  Angle = 360
  AttacherType = Attacher::AttachEngine3D
  Height = 20
  Placement = pos=(0,0,36.15) rot=(0,0,1;0rad)
  Radius = 10.3
FEATURE [Part::MultiFuse] Fusion035  label="removeToCreteHoleForPlugHousing005"
  Placement = pos=(70,19,36) rot=(0,1,0;1.5708rad)
  Shapes = -> [Cylinder017,Cylinder016]
FEATURE [Part::Cut] Cut009  label="plugHousingTab001"
  Base = -> Box005
  Placement = pos=(-107.4,-14,0) rot=(0,0,1;0rad)
  Tool = -> Fusion035
FEATURE [Part::Box] Box006  label="Cube006"
  AttacherType = Attacher::AttachEngine3D
  Height = 28
  Length = 3
  Placement = pos=(110.7,19,22) rot=(0,0,1;0rad)
  Width = 15.7
FEATURE [Part::Cylinder] Cylinder018
  Angle = 360
  AttacherType = Attacher::AttachEngine3D
  Height = 10
  Placement = pos=(0,0,36.15) rot=(0,0,1;0rad)
  Radius = 4
FEATURE [Part::Cylinder] Cylinder019
  Angle = 360
  AttacherType = Attacher::AttachEngine3D
  Height = 20
  Placement = pos=(0,0,36.15) rot=(0,0,1;0rad)
  Radius = 10.3
FEATURE [Part::MultiFuse] Fusion036  label="removeToCreteHoleForPlugHousing006"
  Placement = pos=(70,19,36) rot=(0,1,0;1.5708rad)
  Shapes = -> [Cylinder019,Cylinder018]
FEATURE [Part::Cut] Cut010  label="plugHousingTab002"
  Base = -> Box006
  Placement = pos=(-107.4,-14,0) rot=(0,0,1;0rad)
  Tool = -> Fusion036
FEATURE [Part::MultiFuse] Fusion037
  Placement = pos=(9.6,23,0) rot=(0,0,1;3.14159rad)
  Shapes = -> [Cut009,Cut010]
FEATURE [Part::Box] Box  label="Cube"
  AttacherType = Attacher::AttachEngine3D
  Height = 10
  Length = 3
  Placement = pos=(3.3,4,12) rot=(0,0,1;0rad)
  Width = 10
FEATURE [Part::Fillet] Fillet004
  Base = -> Fusion028
  Edges = 1 edges r=2: [Edge25]
FEATURE [Part::Fillet] Fillet005  label="plugHousing046"
  Base = -> Fillet004
  Edges = 1 edges r=2: [Edge8]
FEATURE [Part::Fillet] Fillet006
  Base = -> Box
  Edges = 1 edges r=2: [Edge11]
FEATURE [Part::Box] Box007  label="Cube007"
  AttacherType = Attacher::AttachEngine3D
  Height = 10
  Length = 3
  Placement = pos=(3.3,4,50) rot=(0,0,1;0rad)
  Width = 10
FEATURE [Part::Fillet] Fillet007
  Base = -> Box007
  Edges = 1 edges r=2: [Edge12]
FEATURE [Part::Box] Box008  label="Cube008"
  AttacherType = Attacher::AttachEngine3D
  Height = 28
  Length = 4
  Placement = pos=(5,0,22) rot=(0,0,1;0rad)
  Width = 10
FEATURE [Part::Fillet] Fillet008
  Base = -> Box008
  Edges = 1 edges r=1: [Edge7]
FEATURE [Part::Fillet] Fillet009
  Base = -> Fillet008
  Edges = 1 edges r=2: [Edge5]
FEATURE [Part::Fillet] Fillet010
  Base = -> Fillet009
  Edges = 1 edges r=2: [Edge2]
FEATURE [Sketcher::SketchObject] Sketch009  label="topSketch003"
  FullyConstrained = true
  sketch-geometry (4):
    g0: LineSegment StartX=16.8446 StartY=31.512 StartZ=0 EndX=16.3251 EndY=34.4666 EndZ=0
    g1: ArcOfCircle CenterX=19 CenterY=19.2524 CenterZ=0 NormalX=0 NormalY=0 NormalZ=1 AngleXU=0 Radius=15.4476 StartAngle=1.74483 EndAngle=2.72717
    g2: ArcOfCircle CenterX=19 CenterY=19.2524 CenterZ=0 NormalX=0 NormalY=0 NormalZ=1 AngleXU=0 Radius=12.4476 StartAngle=1.74483 EndAngle=2.73189
    g3: LineSegment StartX=4.86004 StartY=25.4725 StartZ=0 EndX=7.58253 EndY=24.2107 EndZ=0
  constraints (7):
    c: Block(g0)
    c: Coincident(g1,g0)
    c: Coincident(g2,g0)
    c: Coincident(g3,g1)
    c: Coincident(g3,g2)
    c: Block(g1)
    c: Block(g2)
FEATURE [Part::Extrusion] Extrude008
  Base = -> Sketch009
  Dir = (0,0,1)
  DirMode = 2
  FaceMakerClass = Part::FaceMakerBullseye
  LengthFwd = 10
  LengthRev = 0
  Placement = pos=(0,0,31) rot=(0,0,1;0rad)
  Solid = true
  Symmetric = false
FEATURE [Part::Cylinder] Cylinder020
  Angle = 360
  AttacherType = Attacher::AttachEngine3D
  Height = 20
  Placement = pos=(0,0,36.15) rot=(0,0,1;0rad)
  Radius = 8.2
FEATURE [Part::Cylinder] Cylinder021
  Angle = 360
  AttacherType = Attacher::AttachEngine3D
  Height = 10
  Placement = pos=(0,0,36.15) rot=(0,0,1;0rad)
  Radius = 4
FEATURE [Part::MultiFuse] Fusion038  label="removeToCreteHoleForPlugHousing007"
  Placement = pos=(-42,19,36) rot=(0,1,0;1.5708rad)
  Shapes = -> [Cylinder020,Cylinder021]
FEATURE [Part::Cut] Cut011
  Base = -> Extrude008
  Tool = -> Fusion038
FEATURE [Part::Fillet] Fillet011
  Base = -> Cut011
  Edges = 1 edges r=2: [Edge1]
FEATURE [Part::Fillet] Fillet012
  Base = -> Fillet011
  Edges = 1 edges r=2.5: [Edge1]
FEATURE [Part::Fillet] Fillet013
  Base = -> Fillet012
  Edges = 1 edges r=2.5: [Edge2]
FEATURE [Part::Box] Box010  label="Cube010"
  AttacherType = Attacher::AttachEngine3D
  Height = 16
  Length = 8
  Placement = pos=(12.7,31.52,28) rot=(0,0,1;0rad)
  Width = 4
FEATURE [Sketcher::SketchObject] Sketch010  label="topSketch004"
  FullyConstrained = true
  sketch-geometry (4):
    g0: LineSegment StartX=16.8446 StartY=31.512 StartZ=0 EndX=16.3251 EndY=34.4666 EndZ=0
    g1: ArcOfCircle CenterX=19 CenterY=19.2524 CenterZ=0 NormalX=0 NormalY=0 NormalZ=1 AngleXU=0 Radius=15.4476 StartAngle=1.74483 EndAngle=2.72717
    g2: ArcOfCircle CenterX=19 CenterY=19.2524 CenterZ=0 NormalX=0 NormalY=0 NormalZ=1 AngleXU=0 Radius=12.4476 StartAngle=1.74483 EndAngle=2.73189
    g3: LineSegment StartX=4.86004 StartY=25.4725 StartZ=0 EndX=7.58253 EndY=24.2107 EndZ=0
  constraints (7):
    c: Block(g0)
    c: Coincident(g1,g0)
    c: Coincident(g2,g0)
    c: Coincident(g3,g1)
    c: Coincident(g3,g2)
    c: Block(g1)
    c: Block(g2)
FEATURE [Part::Cylinder] Cylinder022
  Angle = 360
  AttacherType = Attacher::AttachEngine3D
  Height = 10
  Placement = pos=(0,0,36.15) rot=(0,0,1;0rad)
  Radius = 4
FEATURE [Sketcher::SketchObject] Sketch011  label="topSketch005"
  FullyConstrained = true
  sketch-geometry (4):
    g0: LineSegment StartX=16.8446 StartY=31.512 StartZ=0 EndX=16.3251 EndY=34.4666 EndZ=0
    g1: ArcOfCircle CenterX=19 CenterY=19.2524 CenterZ=0 NormalX=0 NormalY=0 NormalZ=1 AngleXU=0 Radius=15.4476 StartAngle=1.74483 EndAngle=2.72717
    g2: ArcOfCircle CenterX=19 CenterY=19.2524 CenterZ=0 NormalX=0 NormalY=0 NormalZ=1 AngleXU=0 Radius=12.4476 StartAngle=1.74483 EndAngle=2.73189
    g3: LineSegment StartX=4.86004 StartY=25.4725 StartZ=0 EndX=7.58253 EndY=24.2107 EndZ=0
  constraints (7):
    c: Block(g0)
    c: Coincident(g1,g0)
    c: Coincident(g2,g0)
    c: Coincident(g3,g1)
    c: Coincident(g3,g2)
    c: Block(g1)
    c: Block(g2)
FEATURE [Part::Extrusion] Extrude010
  Base = -> Sketch011
  Dir = (0,0,1)
  DirMode = 2
  FaceMakerClass = Part::FaceMakerBullseye
  LengthFwd = 10.6
  LengthRev = 0
  Placement = pos=(0,0,31) rot=(0,0,1;0rad)
  Solid = true
  Symmetric = false
FEATURE [Part::Cylinder] Cylinder023
  Angle = 360
  AttacherType = Attacher::AttachEngine3D
  Height = 20
  Placement = pos=(0,0,36.15) rot=(0,0,1;0rad)
  Radius = 8.2
FEATURE [Part::MultiFuse] Fusion039  label="removeToCreteHoleForPlugHousing008"
  Placement = pos=(-42,19,36) rot=(0,1,0;1.5708rad)
  Shapes = -> [Cylinder023,Cylinder022]
FEATURE [Part::Cut] Cut012
  Base = -> Extrude010
  Placement = pos=(0,0,-0.3) rot=(0,0,1;0rad)
  Tool = -> Fusion039
FEATURE [Part::Cut] Cut013
  Base = -> Box010
  Tool = -> Cut012
FEATURE [Part::Fillet] Fillet014
  Base = -> Cut013
  Edges = 1 edges r=0.7: [Edge13]
FEATURE [Part::Fillet] Fillet015
  Base = -> Fillet014
  Edges = 1 edges r=0.7: [Edge13]
FEATURE [Part::Fillet] Fillet016
  Base = -> Fillet015
  Edges = 1 edges r=0.7: [Edge16]
FEATURE [Part::Fillet] Fillet017
  Base = -> Fillet016
  Edges = 1 edges r=0.7: [Edge11]
FEATURE [Part::Fillet] Fillet018
  Base = -> Fillet017
  Edges = 1 edges r=0.7: [Edge10]
FEATURE [Part::Fillet] Fillet019
  Base = -> Fillet018
  Edges = 1 edges r=1.2: [Edge5]
FEATURE [Part::Fillet] Fillet020
  Base = -> Fillet019
  Edges = 1 edges r=1.2: [Edge12]
FEATURE [Part::Fillet] Fillet021
  Base = -> Fillet020
  Edges = 1 edges r=2: [Edge1]
  Placement = pos=(0.3,0,0) rot=(0,0,1;0rad)
FEATURE [Part::MultiFuse] Fusion040  label="top005"
  Shapes = -> [Cut008,Fillet021]
FEATURE [Part::MultiFuse] Fusion041  label="wireHolder"
  Shapes = -> [Fusion033,Fillet013]
FEATURE [Part::MultiFuse] Fusion042
  Shapes = -> [Fillet007,Fusion041]
FEATURE [Part::MultiFuse] Fusion043  label="wireHolder001"
  Shapes = -> [Fusion042,Fillet010]
FEATURE [Part::MultiFuse] Fusion044  label="wireHolder002"
  Shapes = -> [Fillet006,Fusion037,Fusion043]
FEATURE [Part::Feature] Face026
  shape: bbox 11 x 6 x 2e-07 mm, 1 faces, 0 solids (baked)
FEATURE [Part::Revolution] Revolve026
  Angle = 360
  Axis = (0,1,0)
  Base = (0,0,0)
  FaceMakerClass = Part::FaceMakerBullseye
  Placement = pos=(30.3,-1,19.7) rot=(0,0,1;0rad)
  Solid = false
  Source = -> Face026
  Symmetric = false
FEATURE [Sketcher::SketchObject] Sketch013  label="topSketch006"
  FullyConstrained = true
  sketch-geometry (13):
    g0: LineSegment StartX=117 StartY=19 StartZ=0 EndX=117 EndY=38 EndZ=0
    g1: ArcOfCircle CenterX=98 CenterY=19 CenterZ=0 NormalX=0 NormalY=0 NormalZ=1 AngleXU=0 Radius=19 StartAngle=5.7297 EndAngle=6.28319
    g2: LineSegment StartX=0 StartY=3 StartZ=0 EndX=0 EndY=19 EndZ=0
    g3: LineSegment StartX=19 StartY=38 StartZ=0 EndX=117 EndY=38 EndZ=0
    g4: ArcOfCircle CenterX=19 CenterY=19 CenterZ=0 NormalX=0 NormalY=0 NormalZ=1 AngleXU=0 Radius=19 StartAngle=1.5708 EndAngle=3.14159
    g5: ArcOfCircle CenterX=19 CenterY=19 CenterZ=0 NormalX=0 NormalY=0 NormalZ=1 AngleXU=0 Radius=16 StartAngle=1.5708 EndAngle=3.14159
    g6: ArcOfCircle CenterX=98 CenterY=19 CenterZ=0 NormalX=0 NormalY=0 NormalZ=1 AngleXU=0 Radius=16 StartAngle=5.60905 EndAngle=6.28319
    g7: LineSegment StartX=114 StartY=19 StartZ=0 EndX=114 EndY=35 EndZ=0
    g8: LineSegment StartX=110.5 StartY=9.01251 StartZ=0 EndX=114.163 EndY=9.01251 EndZ=0
    g9: LineSegment StartX=114 StartY=35 StartZ=0 EndX=19 EndY=35 EndZ=0
    g10: LineSegment StartX=0 StartY=3 StartZ=0 EndX=0 EndY=0 EndZ=0
    g11: LineSegment StartX=3 StartY=0 StartZ=0 EndX=0 EndY=0 EndZ=0
    g12: LineSegment StartX=3 StartY=19 StartZ=0 EndX=3 EndY=0 EndZ=0
  constraints (33):
    c: Vertical(g0)
    c: Distance(g0) = 19
    c: Block(g0)
    c: Coincident(g1,g0)
    c: Block(g1)
    c: Vertical(g2)
    c: Block(g2)
    c: Coincident(g3,g0)
    c: Horizontal(g3)
    c: Distance(g3) = 98
    c: Coincident(g4,g3)
    c: Coincident(g4,g2)
    c: Block(g4)
    c: Coincident(g5,g4)
    c: Coincident(g6,g1)
    c: Block(g6)
    c: Block(g5)
    c: Coincident(g7,g6)
    c: Vertical(g7)
    c: Coincident(g8,g6)
    c: Coincident(g8,g1)
    c: Coincident(g9,g7)
    c: Coincident(g9,g5)
    c: Horizontal(g9)
    c: Tangent(g9,g5)
    c: Coincident(g10,g2)
    c: Distance(g10) = 3
    c: Vertical(g10)
    c: Coincident(g11,g10)
    c: Horizontal(g11)
    c: Coincident(g12,g5)
    c: Coincident(g12,g11)
    c: Vertical(g12)
FEATURE [Part::Extrusion] Extrude011  label="top006"
  Base = -> Sketch013
  Dir = (0,0,1)
  DirMode = 2
  FaceMakerClass = Part::FaceMakerBullseye
  LengthFwd = 72
  LengthRev = 0
  Solid = true
  Symmetric = false
FEATURE [Sketcher::SketchObject] Sketch014
  FullyConstrained = true
  MapMode = 3
  Placement = pos=(0,0,0) rot=(1,0,0;1.5708rad)
  Support = -> [Extrude011]
  sketch-geometry (8):
    g0: Circle CenterX=80.351 CenterY=-67.6202 CenterZ=0 NormalX=0 NormalY=0 NormalZ=1 AngleXU=0 Radius=2
    g1: Circle CenterX=80.351 CenterY=-67.6202 CenterZ=0 NormalX=0 NormalY=0 NormalZ=1 AngleXU=0 Radius=3
    g2: Circle CenterX=80.351 CenterY=-4.92017 CenterZ=0 NormalX=0 NormalY=0 NormalZ=1 AngleXU=0 Radius=2
    g3: Circle CenterX=80.351 CenterY=-4.92017 CenterZ=0 NormalX=0 NormalY=0 NormalZ=1 AngleXU=0 Radius=3
    g4: Circle CenterX=23.851 CenterY=-4.92017 CenterZ=0 NormalX=0 NormalY=0 NormalZ=1 AngleXU=0 Radius=2
    g5: Circle CenterX=23.851 CenterY=-4.92017 CenterZ=0 NormalX=0 NormalY=0 NormalZ=1 AngleXU=0 Radius=3
    g6: Circle CenterX=23.851 CenterY=-67.6202 CenterZ=0 NormalX=0 NormalY=0 NormalZ=1 AngleXU=0 Radius=2
    g7: Circle CenterX=23.851 CenterY=-67.6202 CenterZ=0 NormalX=0 NormalY=0 NormalZ=1 AngleXU=0 Radius=3
  constraints (8):
    c: Block(g3)
    c: Block(g2)
    c: Block(g1)
    c: Block(g0)
    c: Block(g6)
    c: Block(g7)
    c: Block(g4)
    c: Block(g5)
FEATURE [Part::Feature] Face027
  shape: bbox 11 x 6 x 2e-07 mm, 1 faces, 0 solids (baked)
FEATURE [Part::Revolution] Revolve027
  Angle = 360
  Axis = (0,1,0)
  Base = (0,0,0)
  FaceMakerClass = Part::FaceMakerBullseye
  Placement = pos=(30.3,-1,51.7) rot=(0,0,1;0rad)
  Solid = false
  Source = -> Face027
  Symmetric = false
FEATURE [Part::Feature] Face028
  shape: bbox 11 x 6 x 2e-07 mm, 1 faces, 0 solids (baked)
FEATURE [Part::Revolution] Revolve028
  Angle = 360
  Axis = (0,1,0)
  Base = (0,0,0)
  FaceMakerClass = Part::FaceMakerBullseye
  Placement = pos=(62.3,-1,19.7) rot=(0,0,1;0rad)
  Solid = false
  Source = -> Face028
  Symmetric = false
FEATURE [Part::Feature] Face029
  shape: bbox 11 x 6 x 2e-07 mm, 1 faces, 0 solids (baked)
FEATURE [Part::Revolution] Revolve029
  Angle = 360
  Axis = (0,1,0)
  Base = (0,0,0)
  FaceMakerClass = Part::FaceMakerBullseye
  Placement = pos=(62.3,-1,51.7) rot=(0,0,1;0rad)
  Solid = false
  Source = -> Face029
  Symmetric = false
FEATURE [Part::Feature] Wire
  shape: bbox 11 x 5.2 x 2e-07 mm, 0 faces, 0 solids (baked)
FEATURE [Part::Revolution] Revolve030
  Angle = 360
  Axis = (0,1,0)
  Base = (0,0,0)
  FaceMakerClass = Part::FaceMakerBullseye
  Placement = pos=(30.3,38,19.7) rot=(0,0,1;0rad)
  Solid = true
  Source = -> Wire
  Symmetric = false
FEATURE [Part::Feature] Wire001
  shape: bbox 11 x 5.2 x 2e-07 mm, 0 faces, 0 solids (baked)
FEATURE [Part::Revolution] Revolve031
  Angle = 360
  Axis = (0,1,0)
  Base = (0,0,0)
  FaceMakerClass = Part::FaceMakerBullseye
  Placement = pos=(30.3,38,51.7) rot=(0,0,1;0rad)
  Solid = true
  Source = -> Wire001
  Symmetric = false
FEATURE [Part::Feature] Wire002
  shape: bbox 11 x 5.2 x 2e-07 mm, 0 faces, 0 solids (baked)
FEATURE [Part::Revolution] Revolve032
  Angle = 360
  Axis = (0,1,0)
  Base = (0,0,0)
  FaceMakerClass = Part::FaceMakerBullseye
  Placement = pos=(62.3,38,51.7) rot=(0,0,1;0rad)
  Solid = true
  Source = -> Wire002
  Symmetric = false
FEATURE [Part::Feature] Wire003
  shape: bbox 11 x 5.2 x 2e-07 mm, 0 faces, 0 solids (baked)
FEATURE [Part::Revolution] Revolve033
  Angle = 360
  Axis = (0,1,0)
  Base = (0,0,0)
  FaceMakerClass = Part::FaceMakerBullseye
  Placement = pos=(62.3,38,19.7) rot=(0,0,1;0rad)
  Solid = true
  Source = -> Wire003
  Symmetric = false
FEATURE [Part::MultiFuse] Fusion045  label="altRandScrewHousing"
  Shapes = -> [Revolve029,Revolve027,Revolve028,Revolve026]
FEATURE [Part::MultiFuse] Fusion046  label="fanScrewHousing"
  Shapes = -> [Revolve033,Revolve032,Revolve031,Revolve030]
FEATURE [Sketcher::SketchObject] Sketch015
  FullyConstrained = true
  sketch-geometry (17):
    g0: Circle CenterX=-3.5 CenterY=23.5 CenterZ=0 NormalX=0 NormalY=0 NormalZ=1 AngleXU=0 Radius=1
    g1: Circle CenterX=-1 CenterY=15.25 CenterZ=0 NormalX=0 NormalY=0 NormalZ=1 AngleXU=0 Radius=1
    g2: Circle CenterX=-3.5 CenterY=7 CenterZ=0 NormalX=0 NormalY=0 NormalZ=1 AngleXU=0 Radius=1
    g3: BSplineCurve PolesCount=3 KnotsCount=2 Degree=2 IsPeriodic=0
    g4: GeomPoint X=-3.5 Y=23.5 Z=0
    g5: GeomPoint X=-3.5 Y=7 Z=0
    g6: Circle CenterX=-4.8 CenterY=30.5 CenterZ=0 NormalX=0 NormalY=0 NormalZ=1 AngleXU=0 Radius=1
    g7: Circle CenterX=-3.5 CenterY=30.5 CenterZ=0 NormalX=0 NormalY=0 NormalZ=1 AngleXU=0 Radius=1
    g8: Circle CenterX=-3.5 CenterY=29.2 CenterZ=0 NormalX=0 NormalY=0 NormalZ=1 AngleXU=0 Radius=1
    g9: BSplineCurve PolesCount=3 KnotsCount=2 Degree=2 IsPeriodic=0
    g10: GeomPoint X=-4.8 Y=30.5 Z=0
    g11: GeomPoint X=-3.5 Y=29.2 Z=0
    g12: LineSegment StartX=-3.5 StartY=29.2 StartZ=0 EndX=-3.5 EndY=23.5 EndZ=0
    g13: LineSegment StartX=-4.8 StartY=30.5 StartZ=0 EndX=0 EndY=30.5 EndZ=0
    g14: LineSegment StartX=-3.5 StartY=0.3 StartZ=0 EndX=0 EndY=0.3 EndZ=0
    g15: LineSegment StartX=-3.5 StartY=0.3 StartZ=0 EndX=-3.5 EndY=7 EndZ=0
    g16: LineSegment StartX=0 StartY=0.3 StartZ=0 EndX=0 EndY=30.5 EndZ=0
  constraints (33):
    c: Weight(g0) = 1
    c: Equal(g0,g1)
    c: Equal(g0,g2)
    c: InternalAlignment(g0,g3)
    c: InternalAlignment(g1,g3)
    c: InternalAlignment(g2,g3)
    c: InternalAlignment(g4,g3)
    c: InternalAlignment(g5,g3)
    c: Block(g3)
    c: Weight(g6) = 1
    c: Equal(g6,g7)
    c: Equal(g6,g8)
    c: InternalAlignment(g6,g9)
    c: InternalAlignment(g7,g9)
    c: InternalAlignment(g8,g9)
    c: InternalAlignment(g10,g9)
    c: InternalAlignment(g11,g9)
    c: Block(g9)
    c: Coincident(g12,g9)
    c: Coincident(g12,g3)
    c: Vertical(g12)
    c: Coincident(g13,g9)
    c: Horizontal(g13)
    c: Distance(g13) = 4.8
    c: Horizontal(g14)
    c: Block(g14)
    c: Coincident(g15,g14)
    c: Coincident(g15,g3)
    c: Vertical(g15)
    c: Coincident(g16,g14)
    c: Coincident(g16,g13)
    c: Vertical(g16)
    c: Tangent(g16,g1)
FEATURE [Sketcher::SketchObject] Sketch016
  FullyConstrained = true
  sketch-geometry (16):
    g0: Circle CenterX=-3.5 CenterY=23.5 CenterZ=0 NormalX=0 NormalY=0 NormalZ=1 AngleXU=0 Radius=1
    g1: Circle CenterX=-1 CenterY=15.25 CenterZ=0 NormalX=0 NormalY=0 NormalZ=1 AngleXU=0 Radius=1
    g2: Circle CenterX=-3.5 CenterY=7 CenterZ=0 NormalX=0 NormalY=0 NormalZ=1 AngleXU=0 Radius=1
    g3: BSplineCurve PolesCount=3 KnotsCount=2 Degree=2 IsPeriodic=0
    g4: GeomPoint X=-3.5 Y=23.5 Z=0
    g5: GeomPoint X=-3.5 Y=7 Z=0
    g6: LineSegment StartX=-3.5 StartY=28.2 StartZ=0 EndX=-3.5 EndY=23.5 EndZ=0
    g7: LineSegment StartX=0 StartY=29.5 StartZ=0 EndX=0 EndY=30 EndZ=0
    g8: LineSegment StartX=-3.5 StartY=28.2 StartZ=0 EndX=-3.5 EndY=30 EndZ=0
    g9: LineSegment StartX=0 StartY=30 StartZ=0 EndX=0 EndY=30.5 EndZ=0
    g10: LineSegment StartX=0 StartY=30.5 StartZ=0 EndX=-3.5 EndY=30.5 EndZ=0
    g11: LineSegment StartX=-3.5 StartY=30.5 StartZ=0 EndX=-3.5 EndY=30 EndZ=0
    g12: LineSegment StartX=0 StartY=29.5 StartZ=0 EndX=0 EndY=5 EndZ=0
    g13: LineSegment StartX=-3.5 StartY=0.3 StartZ=0 EndX=-3.5 EndY=7 EndZ=0
    g14: LineSegment StartX=-3.5 StartY=0.3 StartZ=0 EndX=0 EndY=0.3 EndZ=0
    g15: LineSegment StartX=0 StartY=5 StartZ=0 EndX=0 EndY=0.3 EndZ=0
  constraints (39):
    c: Weight(g0) = 1
    c: Equal(g0,g1)
    c: Equal(g0,g2)
    c: InternalAlignment(g0,g3)
    c: InternalAlignment(g1,g3)
    c: InternalAlignment(g2,g3)
    c: InternalAlignment(g4,g3)
    c: InternalAlignment(g5,g3)
    c: Block(g3)
    c: Coincident(g6,g3)
    c: Vertical(g6)
    c: Vertical(g7)
    c: Distance(g7) = 0.5
    c: Coincident(g8,g6)
    c: Vertical(g8)
    c: Block(g6)
    c: Block(g7)
    c: Vertical(g9)
    c: Equal(g7,g9) = 0.5
    c: Block(g9)
    c: Coincident(g9,g7)
    c: Horizontal(g10)
    c: Coincident(g10,g9)
    c: Coincident(g11,g10)
    c: Coincident(g11,g8)
    c: Vertical(g11)
    c: Block(g11)
    c: Coincident(g12,g7)
    c: Vertical(g12)
    c: Coincident(g13,g3)
    c: Vertical(g13)
    c: Distance(g13) = 6.7
    c: Coincident(g14,g13)
    c: Horizontal(g14)
    c: Block(g14)
    c: Coincident(g15,g12)
    c: Coincident(g15,g14)
    c: Vertical(g15)
    c: Block(g15)
FEATURE [Sketcher::SketchObject] Sketch017
  FullyConstrained = true
  sketch-geometry (11):
    g0: LineSegment StartX=-3.5 StartY=1e-16 StartZ=0 EndX=-1.6 EndY=1e-16 EndZ=0
    g1: LineSegment StartX=-1.6 StartY=1e-16 StartZ=0 EndX=-1.6 EndY=1.5 EndZ=0
    g2: LineSegment StartX=-3.5 StartY=1.5 StartZ=0 EndX=-1.6 EndY=1.5 EndZ=0
    g3: LineSegment StartX=-3.5 StartY=1e-16 StartZ=0 EndX=-4.8 EndY=1e-16 EndZ=0
    g4: Circle CenterX=-3.5 CenterY=1.3 CenterZ=0 NormalX=0 NormalY=0 NormalZ=1 AngleXU=0 Radius=1
    g5: Circle CenterX=-3.5 CenterY=1e-16 CenterZ=0 NormalX=0 NormalY=0 NormalZ=1 AngleXU=0 Radius=1
    g6: Circle CenterX=-4.8 CenterY=1e-16 CenterZ=0 NormalX=0 NormalY=0 NormalZ=1 AngleXU=0 Radius=1
    g7: BSplineCurve PolesCount=3 KnotsCount=2 Degree=2 IsPeriodic=0
    g8: GeomPoint X=-3.5 Y=1.3 Z=0
    g9: GeomPoint X=-4.8 Y=1e-16 Z=0
    g10: LineSegment StartX=-3.5 StartY=1.3 StartZ=0 EndX=-3.5 EndY=1.5 EndZ=0
  constraints (24):
    c: Horizontal(g0)
    c: Distance(g0) = 1.9
    c: Block(g0)
    c: Coincident(g1,g0)
    c: Vertical(g1)
    c: Coincident(g2,g1)
    c: Horizontal(g2)
    c: Coincident(g3,g0)
    c: Horizontal(g3)
    c: Distance(g3) = 1.3
    c: Weight(g4) = 1
    c: Equal(g4,g5)
    c: Coincident(g5,g0)
    c: Equal(g4,g6)
    c: Coincident(g7,g3)
    c: InternalAlignment(g4,g7)
    c: InternalAlignment(g5,g7)
    c: InternalAlignment(g6,g7)
    c: InternalAlignment(g8,g7)
    c: InternalAlignment(g9,g7)
    c: Coincident(g10,g7)
    c: Coincident(g10,g2)
    c: Vertical(g10)
    c: Block(g10)
FEATURE [Part::Feature] Face035
  shape: bbox 3.2 x 1.5 x 2e-07 mm, 1 faces, 0 solids (baked)
FEATURE [Part::Revolution] Revolve039  label="backCaseScrewRetainer"
  Angle = 360
  Axis = (0,1,0)
  Base = (0,0,0)
  FaceMakerClass = Part::FaceMakerBullseye
  Placement = pos=(12.5,3,62) rot=(0,0,1;0rad)
  Solid = false
  Source = -> Face035
  Symmetric = false
FEATURE [Part::Feature] Face036
  shape: bbox 3.2 x 1.5 x 2e-07 mm, 1 faces, 0 solids (baked)
FEATURE [Part::Feature] Face039
  shape: bbox 4.8 x 30.2 x 2e-07 mm, 1 faces, 0 solids (baked)
FEATURE [Part::Revolution] Revolve043  label="frontCaseScrewPost002"
  Angle = 360
  Axis = (0,1,0)
  Base = (0,0,0)
  FaceMakerClass = Part::FaceMakerBullseye
  Placement = pos=(89.5,4.5,3.5) rot=(0,0,1;0rad)
  Solid = false
  Source = -> Face039
  Symmetric = false
FEATURE [Part::Feature] Face042
  shape: bbox 4.8 x 30.2 x 2e-07 mm, 1 faces, 0 solids (baked)
FEATURE [Part::Revolution] Revolve046  label="frontCaseScrewPost003"
  Angle = 360
  Axis = (0,1,0)
  Base = (0,0,0)
  FaceMakerClass = Part::FaceMakerBullseye
  Placement = pos=(89.5,4.5,68.5) rot=(0,0,1;0rad)
  Solid = false
  Source = -> Face042
  Symmetric = false
FEATURE [Part::Feature] Face043
  shape: bbox 3.2 x 1.5 x 2e-07 mm, 1 faces, 0 solids (baked)
FEATURE [Part::Revolution] Revolve047  label="frontCaseScrewRetainer002"
  Angle = 360
  Axis = (0,1,0)
  Base = (0,0,0)
  FaceMakerClass = Part::FaceMakerBullseye
  Placement = pos=(89.5,3,68.5) rot=(0,0,1;0rad)
  Solid = false
  Source = -> Face043
  Symmetric = false
FEATURE [Part::Feature] Face044
  shape: bbox 3.2 x 1.5 x 2e-07 mm, 1 faces, 0 solids (baked)
FEATURE [Part::Revolution] Revolve048  label="frontCaseScrewRetainer003"
  Angle = 360
  Axis = (0,1,0)
  Base = (0,0,0)
  FaceMakerClass = Part::FaceMakerBullseye
  Placement = pos=(89.5,3,3.5) rot=(0,0,1;0rad)
  Solid = false
  Source = -> Face044
  Symmetric = false
FEATURE [App::MeasureDistance] Distance002  label="Distance: 1.67 mm"
  Distance = 1.66921
  P1 = (99.2361,4.7524,71.7)
  P2 = (99.2347,6.42161,71.7)
FEATURE [Sketcher::SketchObject] Sketch018
  FullyConstrained = true
  sketch-geometry (7):
    g0: LineSegment StartX=0 StartY=0 StartZ=0 EndX=0 EndY=6 EndZ=0
    g1: Circle CenterX=0 CenterY=0 CenterZ=0 NormalX=0 NormalY=0 NormalZ=1 AngleXU=0 Radius=1
    g2: Circle CenterX=8 CenterY=6 CenterZ=0 NormalX=0 NormalY=0 NormalZ=1 AngleXU=0 Radius=1
    g3: BSplineCurve PolesCount=3 KnotsCount=2 Degree=2 IsPeriodic=0
    g4: GeomPoint X=0 Y=0 Z=0
    g5: GeomPoint X=8 Y=6 Z=0
    g6: LineSegment StartX=0 StartY=6 StartZ=0 EndX=8 EndY=6 EndZ=0
  constraints (14):
    c: Coincident(g0,g-1)
    c: Distance(g0) = 6
    c: Vertical(g0)
    c: Coincident(g3,g0)
    c: Weight(g1) = 1
    c: Equal(g1,g2)
    c: InternalAlignment(g1,g3)
    c: InternalAlignment(g2,g3)
    c: InternalAlignment(g4,g3)
    c: InternalAlignment(g5,g3)
    c: Block(g3)
    c: Coincident(g6,g0)
    c: Coincident(g6,g3)
    c: Horizontal(g6)
FEATURE [Part::Extrusion] Extrude012  label="caseScrewPillarBracket"
  Base = -> Sketch018
  Dir = (0,0,1)
  DirMode = 2
  FaceMakerClass = Part::FaceMakerBullseye
  LengthFwd = 2.4
  LengthRev = 0
  Placement = pos=(15.76,29,8.8) rot=(0,1,0;0rad)
  Solid = true
  Symmetric = false
FEATURE [Sketcher::SketchObject] Sketch019
  FullyConstrained = true
  sketch-geometry (7):
    g0: LineSegment StartX=0 StartY=0 StartZ=0 EndX=0 EndY=6 EndZ=0
    g1: Circle CenterX=0 CenterY=0 CenterZ=0 NormalX=0 NormalY=0 NormalZ=1 AngleXU=0 Radius=1
    g2: Circle CenterX=8 CenterY=6 CenterZ=0 NormalX=0 NormalY=0 NormalZ=1 AngleXU=0 Radius=1
    g3: BSplineCurve PolesCount=3 KnotsCount=2 Degree=2 IsPeriodic=0
    g4: GeomPoint X=0 Y=0 Z=0
    g5: GeomPoint X=8 Y=6 Z=0
    g6: LineSegment StartX=0 StartY=6 StartZ=0 EndX=8 EndY=6 EndZ=0
  constraints (14):
    c: Coincident(g0,g-1)
    c: Distance(g0) = 6
    c: Vertical(g0)
    c: Coincident(g3,g0)
    c: Weight(g1) = 1
    c: Equal(g1,g2)
    c: InternalAlignment(g1,g3)
    c: InternalAlignment(g2,g3)
    c: InternalAlignment(g4,g3)
    c: InternalAlignment(g5,g3)
    c: Block(g3)
    c: Coincident(g6,g0)
    c: Coincident(g6,g3)
    c: Horizontal(g6)
FEATURE [Part::Extrusion] Extrude013  label="caseScrewPillarBracket001"
  Base = -> Sketch019
  Dir = (0,0,1)
  DirMode = 2
  FaceMakerClass = Part::FaceMakerBullseye
  LengthFwd = 2.4
  LengthRev = 0
  Placement = pos=(15.76,29,60.8) rot=(0,0,1;0rad)
  Solid = true
  Symmetric = false
FEATURE [Sketcher::SketchObject] Sketch020
  FullyConstrained = true
  sketch-geometry (7):
    g0: LineSegment StartX=0 StartY=0 StartZ=0 EndX=0 EndY=6 EndZ=0
    g1: Circle CenterX=0 CenterY=0 CenterZ=0 NormalX=0 NormalY=0 NormalZ=1 AngleXU=0 Radius=1
    g2: Circle CenterX=8 CenterY=6 CenterZ=0 NormalX=0 NormalY=0 NormalZ=1 AngleXU=0 Radius=1
    g3: BSplineCurve PolesCount=3 KnotsCount=2 Degree=2 IsPeriodic=0
    g4: GeomPoint X=0 Y=0 Z=0
    g5: GeomPoint X=8 Y=6 Z=0
    g6: LineSegment StartX=0 StartY=6 StartZ=0 EndX=8 EndY=6 EndZ=0
  constraints (14):
    c: Coincident(g0,g-1)
    c: Distance(g0) = 6
    c: Vertical(g0)
    c: Coincident(g3,g0)
    c: Weight(g1) = 1
    c: Equal(g1,g2)
    c: InternalAlignment(g1,g3)
    c: InternalAlignment(g2,g3)
    c: InternalAlignment(g4,g3)
    c: InternalAlignment(g5,g3)
    c: Block(g3)
    c: Coincident(g6,g0)
    c: Coincident(g6,g3)
    c: Horizontal(g6)
FEATURE [Part::Extrusion] Extrude014  label="caseScrewPillarBracket002"
  Base = -> Sketch020
  Dir = (0,0,1)
  DirMode = 2
  FaceMakerClass = Part::FaceMakerBullseye
  LengthFwd = 2.4
  LengthRev = 0
  Placement = pos=(13.7,29,13.26) rot=(0,-1,0;1.5708rad)
  Solid = true
  Symmetric = false
FEATURE [Sketcher::SketchObject] Sketch021
  FullyConstrained = true
  sketch-geometry (7):
    g0: LineSegment StartX=0 StartY=0 StartZ=0 EndX=0 EndY=6 EndZ=0
    g1: Circle CenterX=0 CenterY=0 CenterZ=0 NormalX=0 NormalY=0 NormalZ=1 AngleXU=0 Radius=1
    g2: Circle CenterX=8 CenterY=6 CenterZ=0 NormalX=0 NormalY=0 NormalZ=1 AngleXU=0 Radius=1
    g3: BSplineCurve PolesCount=3 KnotsCount=2 Degree=2 IsPeriodic=0
    g4: GeomPoint X=0 Y=0 Z=0
    g5: GeomPoint X=8 Y=6 Z=0
    g6: LineSegment StartX=0 StartY=6 StartZ=0 EndX=8 EndY=6 EndZ=0
  constraints (14):
    c: Coincident(g0,g-1)
    c: Distance(g0) = 6
    c: Vertical(g0)
    c: Coincident(g3,g0)
    c: Weight(g1) = 1
    c: Equal(g1,g2)
    c: InternalAlignment(g1,g3)
    c: InternalAlignment(g2,g3)
    c: InternalAlignment(g4,g3)
    c: InternalAlignment(g5,g3)
    c: Block(g3)
    c: Coincident(g6,g0)
    c: Coincident(g6,g3)
    c: Horizontal(g6)
FEATURE [Part::Extrusion] Extrude015  label="caseScrewPillarBracket003"
  Base = -> Sketch021
  Dir = (0,0,1)
  DirMode = 2
  FaceMakerClass = Part::FaceMakerBullseye
  LengthFwd = 2.4
  LengthRev = 0
  Placement = pos=(11.3,29,58.74) rot=(0,1,0;1.5708rad)
  Solid = true
  Symmetric = false
FEATURE [Sketcher::SketchObject] Sketch022
  FullyConstrained = true
  sketch-geometry (7):
    g0: LineSegment StartX=0 StartY=0 StartZ=0 EndX=0 EndY=6 EndZ=0
    g1: Circle CenterX=0 CenterY=0 CenterZ=0 NormalX=0 NormalY=0 NormalZ=1 AngleXU=0 Radius=1
    g2: Circle CenterX=8 CenterY=6 CenterZ=0 NormalX=0 NormalY=0 NormalZ=1 AngleXU=0 Radius=1
    g3: BSplineCurve PolesCount=3 KnotsCount=2 Degree=2 IsPeriodic=0
    g4: GeomPoint X=0 Y=0 Z=0
    g5: GeomPoint X=8 Y=6 Z=0
    g6: LineSegment StartX=0 StartY=6 StartZ=0 EndX=8 EndY=6 EndZ=0
  constraints (14):
    c: Coincident(g0,g-1)
    c: Distance(g0) = 6
    c: Vertical(g0)
    c: Coincident(g3,g0)
    c: Weight(g1) = 1
    c: Equal(g1,g2)
    c: InternalAlignment(g1,g3)
    c: InternalAlignment(g2,g3)
    c: InternalAlignment(g4,g3)
    c: InternalAlignment(g5,g3)
    c: Block(g3)
    c: Coincident(g6,g0)
    c: Coincident(g6,g3)
    c: Horizontal(g6)
FEATURE [Part::Extrusion] Extrude016  label="caseScrewPillarBracket004"
  Base = -> Sketch022
  Dir = (0,0,1)
  DirMode = 2
  FaceMakerClass = Part::FaceMakerBullseye
  LengthFwd = 2.4
  LengthRev = 0
  Placement = pos=(88.3,29,65.23) rot=(0,1,0;1.5708rad)
  Solid = true
  Symmetric = false
FEATURE [Sketcher::SketchObject] Sketch023
  FullyConstrained = true
  sketch-geometry (7):
    g0: LineSegment StartX=0 StartY=0 StartZ=0 EndX=0 EndY=6 EndZ=0
    g1: Circle CenterX=0 CenterY=0 CenterZ=0 NormalX=0 NormalY=0 NormalZ=1 AngleXU=0 Radius=1
    g2: Circle CenterX=8 CenterY=6 CenterZ=0 NormalX=0 NormalY=0 NormalZ=1 AngleXU=0 Radius=1
    g3: BSplineCurve PolesCount=3 KnotsCount=2 Degree=2 IsPeriodic=0
    g4: GeomPoint X=0 Y=0 Z=0
    g5: GeomPoint X=8 Y=6 Z=0
    g6: LineSegment StartX=0 StartY=6 StartZ=0 EndX=8 EndY=6 EndZ=0
  constraints (14):
    c: Coincident(g0,g-1)
    c: Distance(g0) = 6
    c: Vertical(g0)
    c: Coincident(g3,g0)
    c: Weight(g1) = 1
    c: Equal(g1,g2)
    c: InternalAlignment(g1,g3)
    c: InternalAlignment(g2,g3)
    c: InternalAlignment(g4,g3)
    c: InternalAlignment(g5,g3)
    c: Block(g3)
    c: Coincident(g6,g0)
    c: Coincident(g6,g3)
    c: Horizontal(g6)
FEATURE [Part::Extrusion] Extrude017  label="caseScrewPillarBracket005"
  Base = -> Sketch023
  Dir = (0,0,1)
  DirMode = 2
  FaceMakerClass = Part::FaceMakerBullseye
  LengthFwd = 2.4
  LengthRev = 0
  Placement = pos=(90.7,29,6.77) rot=(0,-1,0;1.5708rad)
  Solid = true
  Symmetric = false
FEATURE [Sketcher::SketchObject] Sketch024
  FullyConstrained = true
  sketch-geometry (7):
    g0: LineSegment StartX=0 StartY=0 StartZ=0 EndX=0 EndY=6 EndZ=0
    g1: Circle CenterX=0 CenterY=0 CenterZ=0 NormalX=0 NormalY=0 NormalZ=1 AngleXU=0 Radius=1
    g2: Circle CenterX=8 CenterY=6 CenterZ=0 NormalX=0 NormalY=0 NormalZ=1 AngleXU=0 Radius=1
    g3: BSplineCurve PolesCount=3 KnotsCount=2 Degree=2 IsPeriodic=0
    g4: GeomPoint X=0 Y=0 Z=0
    g5: GeomPoint X=8 Y=6 Z=0
    g6: LineSegment StartX=0 StartY=6 StartZ=0 EndX=8 EndY=6 EndZ=0
  constraints (14):
    c: Coincident(g0,g-1)
    c: Distance(g0) = 6
    c: Vertical(g0)
    c: Coincident(g3,g0)
    c: Weight(g1) = 1
    c: Equal(g1,g2)
    c: InternalAlignment(g1,g3)
    c: InternalAlignment(g2,g3)
    c: InternalAlignment(g4,g3)
    c: InternalAlignment(g5,g3)
    c: Block(g3)
    c: Coincident(g6,g0)
    c: Coincident(g6,g3)
    c: Horizontal(g6)
FEATURE [Part::Extrusion] Extrude018  label="caseScrewPillarBracket006"
  Base = -> Sketch024
  Dir = (0,0,1)
  DirMode = 2
  FaceMakerClass = Part::FaceMakerBullseye
  LengthFwd = 2.4
  LengthRev = 0
  Placement = pos=(103.7,29,6.77) rot=(0,-1,0;1.5708rad)
  Solid = true
  Symmetric = false
FEATURE [Sketcher::SketchObject] Sketch025
  FullyConstrained = true
  sketch-geometry (7):
    g0: LineSegment StartX=0 StartY=0 StartZ=0 EndX=0 EndY=6 EndZ=0
    g1: Circle CenterX=0 CenterY=0 CenterZ=0 NormalX=0 NormalY=0 NormalZ=1 AngleXU=0 Radius=1
    g2: Circle CenterX=8 CenterY=6 CenterZ=0 NormalX=0 NormalY=0 NormalZ=1 AngleXU=0 Radius=1
    g3: BSplineCurve PolesCount=3 KnotsCount=2 Degree=2 IsPeriodic=0
    g4: GeomPoint X=0 Y=0 Z=0
    g5: GeomPoint X=8 Y=6 Z=0
    g6: LineSegment StartX=0 StartY=6 StartZ=0 EndX=8 EndY=6 EndZ=0
  constraints (14):
    c: Coincident(g0,g-1)
    c: Distance(g0) = 6
    c: Vertical(g0)
    c: Coincident(g3,g0)
    c: Weight(g1) = 1
    c: Equal(g1,g2)
    c: InternalAlignment(g1,g3)
    c: InternalAlignment(g2,g3)
    c: InternalAlignment(g4,g3)
    c: InternalAlignment(g5,g3)
    c: Block(g3)
    c: Coincident(g6,g0)
    c: Coincident(g6,g3)
    c: Horizontal(g6)
FEATURE [Part::Extrusion] Extrude019  label="caseScrewPillarBracket007"
  Base = -> Sketch025
  Dir = (0,0,1)
  DirMode = 2
  FaceMakerClass = Part::FaceMakerBullseye
  LengthFwd = 2.4
  LengthRev = 0
  Placement = pos=(101.3,29,65.23) rot=(0,1,0;1.5708rad)
  Solid = true
  Symmetric = false
FEATURE [Part::Box] Box011  label="frontCaseScrewPillarBracket"
  AttacherType = Attacher::AttachEngine3D
  Height = 2.4
  Length = 16
  Placement = pos=(87,28,2.3) rot=(0,0,1;0rad)
  Width = 7
FEATURE [Part::Box] Box012  label="frontCaseScrewPillarBracket001"
  AttacherType = Attacher::AttachEngine3D
  Height = 2.4
  Length = 16
  Placement = pos=(87,28,67.3) rot=(0,0,1;0rad)
  Width = 7
FEATURE [Sketcher::SketchObject] Sketch026
  FullyConstrained = true
  sketch-geometry (17):
    g0: Circle CenterX=-3.5 CenterY=23.5 CenterZ=0 NormalX=0 NormalY=0 NormalZ=1 AngleXU=0 Radius=1
    g1: Circle CenterX=-1 CenterY=15.25 CenterZ=0 NormalX=0 NormalY=0 NormalZ=1 AngleXU=0 Radius=1
    g2: Circle CenterX=-3.5 CenterY=7 CenterZ=0 NormalX=0 NormalY=0 NormalZ=1 AngleXU=0 Radius=1
    g3: BSplineCurve PolesCount=3 KnotsCount=2 Degree=2 IsPeriodic=0
    g4: GeomPoint X=-3.5 Y=23.5 Z=0
    g5: GeomPoint X=-3.5 Y=7 Z=0
    g6: Circle CenterX=-4.8 CenterY=30.5 CenterZ=0 NormalX=0 NormalY=0 NormalZ=1 AngleXU=0 Radius=1
    g7: Circle CenterX=-3.5 CenterY=30.5 CenterZ=0 NormalX=0 NormalY=0 NormalZ=1 AngleXU=0 Radius=1
    g8: Circle CenterX=-3.5 CenterY=29.2 CenterZ=0 NormalX=0 NormalY=0 NormalZ=1 AngleXU=0 Radius=1
    g9: BSplineCurve PolesCount=3 KnotsCount=2 Degree=2 IsPeriodic=0
    g10: GeomPoint X=-4.8 Y=30.5 Z=0
    g11: GeomPoint X=-3.5 Y=29.2 Z=0
    g12: LineSegment StartX=-3.5 StartY=29.2 StartZ=0 EndX=-3.5 EndY=23.5 EndZ=0
    g13: LineSegment StartX=-4.8 StartY=30.5 StartZ=0 EndX=0 EndY=30.5 EndZ=0
    g14: LineSegment StartX=-3.5 StartY=5 StartZ=0 EndX=-3.5 EndY=7 EndZ=0
    g15: LineSegment StartX=0 StartY=5 StartZ=0 EndX=0 EndY=30.5 EndZ=0
    g16: LineSegment StartX=-3.5 StartY=5 StartZ=0 EndX=0 EndY=5 EndZ=0
  constraints (33):
    c: Weight(g0) = 1
    c: Equal(g0,g1)
    c: Equal(g0,g2)
    c: InternalAlignment(g0,g3)
    c: InternalAlignment(g1,g3)
    c: InternalAlignment(g2,g3)
    c: InternalAlignment(g4,g3)
    c: InternalAlignment(g5,g3)
    c: Block(g3)
    c: Weight(g6) = 1
    c: Equal(g6,g7)
    c: Equal(g6,g8)
    c: InternalAlignment(g6,g9)
    c: InternalAlignment(g7,g9)
    c: InternalAlignment(g8,g9)
    c: InternalAlignment(g10,g9)
    c: InternalAlignment(g11,g9)
    c: Block(g9)
    c: Coincident(g12,g9)
    c: Coincident(g12,g3)
    c: Vertical(g12)
    c: Coincident(g13,g9)
    c: Horizontal(g13)
    c: Distance(g13) = 4.8
    c: Coincident(g14,g3)
    c: Vertical(g14)
    c: Coincident(g15,g13)
    c: Vertical(g15)
    c: Tangent(g15,g1)
    c: Distance(g14) = 2
    c: Coincident(g16,g14)
    c: Horizontal(g16)
    c: Coincident(g15,g16)
FEATURE [Part::Feature] Face050
  shape: bbox 4.8 x 25.5 x 2e-07 mm, 1 faces, 0 solids (baked)
FEATURE [Part::Revolution] Revolve054  label="moreFrontCaseScrewPost001"
  Angle = 360
  Axis = (0,1,0)
  Base = (0,0,0)
  FaceMakerClass = Part::FaceMakerBullseye
  Placement = pos=(102.5,4.5,3.5) rot=(0,0,1;0rad)
  Solid = false
  Source = -> Face050
  Symmetric = false
FEATURE [Part::Feature] Face051
  shape: bbox 4.8 x 25.5 x 2e-07 mm, 1 faces, 0 solids (baked)
FEATURE [Part::Revolution] Revolve055  label="moreFrontCaseScrewPost002"
  Angle = 360
  Axis = (0,1,0)
  Base = (0,0,0)
  FaceMakerClass = Part::FaceMakerBullseye
  Placement = pos=(102.5,4.5,68.5) rot=(0,0,1;0rad)
  Solid = false
  Source = -> Face051
  Symmetric = false
FEATURE [Sketcher::SketchObject] Sketch027
  FullyConstrained = true
  sketch-geometry (10):
    g0: LineSegment StartX=-1.6 StartY=4.7 StartZ=0 EndX=-1.6 EndY=1.7 EndZ=0
    g1: LineSegment StartX=-3.5 StartY=4.7 StartZ=0 EndX=-1.6 EndY=4.7 EndZ=0
    g2: LineSegment StartX=-1.6 StartY=1.7 StartZ=0 EndX=-1.6 EndY=1.5 EndZ=0
    g3: LineSegment StartX=-1.6 StartY=1.5 StartZ=0 EndX=-5.2 EndY=1.5 EndZ=0
    g4: Circle CenterX=-3.5 CenterY=4.7 CenterZ=0 NormalX=0 NormalY=0 NormalZ=1 AngleXU=0 Radius=1
    g5: Circle CenterX=-3.59627 CenterY=2.99743 CenterZ=0 NormalX=0 NormalY=0 NormalZ=1 AngleXU=0 Radius=1
    g6: Circle CenterX=-5.2 CenterY=1.5 CenterZ=0 NormalX=0 NormalY=0 NormalZ=1 AngleXU=0 Radius=1
    g7: BSplineCurve PolesCount=3 KnotsCount=2 Degree=2 IsPeriodic=0
    g8: GeomPoint X=-3.5 Y=4.7 Z=0
    g9: GeomPoint X=-5.2 Y=1.5 Z=0
  constraints (23):
    c: Vertical(g0)
    c: Distance(g0) = 3
    c: Coincident(g1,g0)
    c: Horizontal(g1)
    c: Block(g0)
    c: Block(g1)
    c: Coincident(g2,g0)
    c: Vertical(g2)
    c: Distance(g2) = 0.2
    c: Coincident(g3,g2)
    c: Horizontal(g3)
    c: Block(g3)
    c: Coincident(g7,g1)
    c: Weight(g4) = 1
    c: Equal(g4,g5)
    c: Equal(g4,g6)
    c: Coincident(g7,g3)
    c: InternalAlignment(g4,g7)
    c: InternalAlignment(g5,g7)
    c: InternalAlignment(g6,g7)
    c: InternalAlignment(g8,g7)
    c: InternalAlignment(g9,g7)
    c: Block(g7)
FEATURE [Sketcher::SketchObject] Sketch028
  FullyConstrained = true
  sketch-geometry (18):
    g0: LineSegment StartX=0 StartY=3e-16 StartZ=0 EndX=0 EndY=1.7 EndZ=0
    g1: LineSegment StartX=-3.5 StartY=0 StartZ=0 EndX=-3.5 EndY=0.9 EndZ=0
    g2: Circle CenterX=-2.7 CenterY=1.7 CenterZ=0 NormalX=0 NormalY=0 NormalZ=1 AngleXU=0 Radius=1
    g3: Circle CenterX=-3.5 CenterY=1.7 CenterZ=0 NormalX=0 NormalY=0 NormalZ=1 AngleXU=0 Radius=1
    g4: Circle CenterX=-3.5 CenterY=0.9 CenterZ=0 NormalX=0 NormalY=0 NormalZ=1 AngleXU=0 Radius=1
    g5: BSplineCurve PolesCount=3 KnotsCount=2 Degree=2 IsPeriodic=0
    g6: GeomPoint X=-2.7 Y=1.7 Z=0
    g7: GeomPoint X=-3.5 Y=0.9 Z=0
    g8: LineSegment StartX=-3.5 StartY=0 StartZ=0 EndX=-3.5 EndY=-7 EndZ=0
    g9: LineSegment StartX=0 StartY=3e-16 StartZ=0 EndX=0 EndY=-7 EndZ=0
    g10: LineSegment StartX=-3.5 StartY=-7 StartZ=0 EndX=0 EndY=-7 EndZ=0
    g11: LineSegment StartX=-2.7 StartY=1.7 StartZ=0 EndX=-1.6 EndY=1.7 EndZ=0
    g12: LineSegment StartX=0 StartY=1.7 StartZ=0 EndX=0 EndY=4.5 EndZ=0
    g13: LineSegment StartX=0 StartY=4.5 StartZ=0 EndX=0 EndY=10.8 EndZ=0
    g14: LineSegment StartX=0 StartY=10.8 StartZ=0 EndX=-2 EndY=10.8 EndZ=0
    g15: LineSegment StartX=-1.6 StartY=4.7 StartZ=0 EndX=-1.6 EndY=1.7 EndZ=0
    g16: LineSegment StartX=-1.6 StartY=4.7 StartZ=0 EndX=-2 EndY=4.7 EndZ=0
    g17: LineSegment StartX=-2 StartY=4.7 StartZ=0 EndX=-2 EndY=10.8 EndZ=0
  constraints (44):
    c: Vertical(g0)
    c: Vertical(g1)
    c: Distance(g1) = 0.9
    c: Block(g0)
    c: Distance(g0) = 1.7
    c: Weight(g2) = 1
    c: Equal(g2,g3)
    c: Equal(g2,g4)
    c: Coincident(g5,g1)
    c: InternalAlignment(g2,g5)
    c: InternalAlignment(g3,g5)
    c: InternalAlignment(g4,g5)
    c: InternalAlignment(g6,g5)
    c: InternalAlignment(g7,g5)
    c: Block(g5)
    c: Coincident(g8,g1)
    c: Vertical(g8)
    c: Distance(g8) = 7
    c: Vertical(g9)
    c: Equal(g8,g9) = 7
    c: Coincident(g9,g0)
    c: Coincident(g10,g8)
    c: Coincident(g10,g9)
    c: Horizontal(g10)
    c: Coincident(g11,g5)
    c: Horizontal(g11)
    c: Coincident(g12,g0)
    c: Vertical(g12)
    c: Distance(g12) = 2.8
    c: Coincident(g13,g12)
    c: Vertical(g13)
    c: Distance(g13) = 6.3
    c: Coincident(g14,g13)
    c: Horizontal(g14)
    c: Distance(g14) = 2
    c: Vertical(g15)
    c: Distance(g15) = 3
    c: Block(g11)
    c: Coincident(g15,g11)
    c: Coincident(g16,g15)
    c: Horizontal(g16)
    c: Coincident(g17,g16)
    c: Coincident(g17,g14)
    c: Vertical(g17)
FEATURE [Part::Revolution] Revolve040  label="backCaseScrewRetainer001"
  Angle = 360
  Axis = (0,1,0)
  Base = (0,0,0)
  FaceMakerClass = Part::FaceMakerBullseye
  Placement = pos=(12.5,3,10) rot=(0,0,1;0rad)
  Solid = false
  Source = -> Face036
  Symmetric = false
FEATURE [Part::Feature] Face055
  shape: bbox 3.5 x 30.2 x 2e-07 mm, 1 faces, 0 solids (baked)
FEATURE [Part::Revolution] Revolve059  label="backCaseScrewPost"
  Angle = 360
  Axis = (0,1,0)
  Base = (0,0,0)
  FaceMakerClass = Part::FaceMakerBullseye
  Placement = pos=(12.5,4.5,10) rot=(0,0,1;0rad)
  Solid = false
  Source = -> Face055
  Symmetric = false
FEATURE [Part::Feature] Face056
  shape: bbox 3.5 x 30.2 x 2e-07 mm, 1 faces, 0 solids (baked)
FEATURE [Part::Revolution] Revolve060  label="backCaseScrewPost001"
  Angle = 360
  Axis = (0,1,0)
  Base = (0,0,0)
  FaceMakerClass = Part::FaceMakerBullseye
  Placement = pos=(12.5,4.5,62) rot=(0,0,1;0rad)
  Solid = false
  Source = -> Face056
  Symmetric = false
FEATURE [Part::Feature] Face057
  shape: bbox 3.5 x 17.8 x 2e-07 mm, 1 faces, 0 solids (baked)
FEATURE [Part::Revolution] Revolve061  label="removeToCreateScrewAndThreadedInsertHole"
  Angle = 360
  Axis = (0,1,0)
  Base = (0,0,0)
  FaceMakerClass = Part::FaceMakerBullseye
  Placement = pos=(12.5,0,10) rot=(0,0,1;0rad)
  Solid = false
  Source = -> Face057
  Symmetric = false
FEATURE [Part::Feature] Face058
  shape: bbox 3.5 x 17.8 x 2e-07 mm, 1 faces, 0 solids (baked)
FEATURE [Part::Revolution] Revolve062  label="removeToCreateScrewAndThreadedInsertHole001"
  Angle = 360
  Axis = (0,1,0)
  Base = (0,0,0)
  FaceMakerClass = Part::FaceMakerBullseye
  Placement = pos=(12.5,0,62) rot=(0,0,1;0rad)
  Solid = false
  Source = -> Face058
  Symmetric = false
FEATURE [Part::Feature] Face059
  shape: bbox 3.5 x 17.8 x 2e-07 mm, 1 faces, 0 solids (baked)
FEATURE [Part::Revolution] Revolve063  label="removeToCreateScrewAndThreadedInsertHole002"
  Angle = 360
  Axis = (0,1,0)
  Base = (0,0,0)
  FaceMakerClass = Part::FaceMakerBullseye
  Placement = pos=(89.5,0,68.5) rot=(0,0,1;0rad)
  Solid = false
  Source = -> Face059
  Symmetric = false
FEATURE [Part::Feature] Face060
  shape: bbox 3.5 x 17.8 x 2e-07 mm, 1 faces, 0 solids (baked)
FEATURE [Part::Revolution] Revolve064  label="removeToCreateScrewAndThreadedInsertHole003"
  Angle = 360
  Axis = (0,1,0)
  Base = (0,0,0)
  FaceMakerClass = Part::FaceMakerBullseye
  Placement = pos=(89.5,0,3.5) rot=(0,0,1;0rad)
  Solid = false
  Source = -> Face060
  Symmetric = false
FEATURE [Part::Feature] Face061
  shape: bbox 3.5 x 17.8 x 2e-07 mm, 1 faces, 0 solids (baked)
FEATURE [Part::Revolution] Revolve065  label="removeToCreateScrewAndThreadedInsertHole004"
  Angle = 360
  Axis = (0,1,0)
  Base = (0,0,0)
  FaceMakerClass = Part::FaceMakerBullseye
  Placement = pos=(102.5,4.7,3.5) rot=(0,0,1;0rad)
  Solid = false
  Source = -> Face061
  Symmetric = false
FEATURE [Part::Feature] Face062
  shape: bbox 3.5 x 17.8 x 2e-07 mm, 1 faces, 0 solids (baked)
FEATURE [Part::Revolution] Revolve066  label="removeToCreateScrewAndThreadedInsertHole005"
  Angle = 360
  Axis = (0,1,0)
  Base = (0,0,0)
  FaceMakerClass = Part::FaceMakerBullseye
  Placement = pos=(102.5,4.7,68.5) rot=(0,0,1;0rad)
  Solid = false
  Source = -> Face062
  Symmetric = false
FEATURE [Part::MultiFuse] Fusion047  label="makeHoles"
  Shapes = -> [Revolve066,Revolve065,Revolve064,Revolve063,Revolve062,Revolve061]
FEATURE [Part::Feature] Face063
  shape: bbox 3.6 x 3.2 x 2e-07 mm, 1 faces, 0 solids (baked)
FEATURE [Part::Revolution] Revolve067  label="moreFrontCaseScrewRetainer002"
  Angle = 360
  Axis = (0,1,0)
  Base = (0,0,0)
  FaceMakerClass = Part::FaceMakerBullseye
  Placement = pos=(102.5,4.5,68.5) rot=(0,0,1;0rad)
  Solid = false
  Source = -> Face063
  Symmetric = false
FEATURE [Part::Feature] Face064
  shape: bbox 3.6 x 3.2 x 2e-07 mm, 1 faces, 0 solids (baked)
FEATURE [Part::Revolution] Revolve068  label="moreFrontCaseScrewRetainer003"
  Angle = 360
  Axis = (0,1,0)
  Base = (0,0,0)
  FaceMakerClass = Part::FaceMakerBullseye
  Placement = pos=(102.5,4.5,3.5) rot=(0,0,1;0rad)
  Solid = false
  Source = -> Face064
  Symmetric = false
FEATURE [Part::Feature] Face065
  shape: bbox 3.5 x 17.8 x 2e-07 mm, 1 faces, 0 solids (baked)
FEATURE [Part::Revolution] Revolve069  label="removeToCreateScrewAndThreadedInsertHole006"
  Angle = 360
  Axis = (0,1,0)
  Base = (0,0,0)
  FaceMakerClass = Part::FaceMakerBullseye
  Placement = pos=(12.5,0,10) rot=(0,0,1;0rad)
  Solid = false
  Source = -> Face065
  Symmetric = false
FEATURE [Part::Feature] Face066
  shape: bbox 3.5 x 17.8 x 2e-07 mm, 1 faces, 0 solids (baked)
FEATURE [Part::Revolution] Revolve070  label="removeToCreateScrewAndThreadedInsertHole007"
  Angle = 360
  Axis = (0,1,0)
  Base = (0,0,0)
  FaceMakerClass = Part::FaceMakerBullseye
  Placement = pos=(12.5,0,62) rot=(0,0,1;0rad)
  Solid = false
  Source = -> Face066
  Symmetric = false
FEATURE [Part::Feature] Face067
  shape: bbox 3.5 x 17.8 x 2e-07 mm, 1 faces, 0 solids (baked)
FEATURE [Part::Revolution] Revolve071  label="removeToCreateScrewAndThreadedInsertHole008"
  Angle = 360
  Axis = (0,1,0)
  Base = (0,0,0)
  FaceMakerClass = Part::FaceMakerBullseye
  Placement = pos=(89.5,0,68.5) rot=(0,0,1;0rad)
  Solid = false
  Source = -> Face067
  Symmetric = false
FEATURE [Part::Feature] Face068
  shape: bbox 3.5 x 17.8 x 2e-07 mm, 1 faces, 0 solids (baked)
FEATURE [Part::Revolution] Revolve072  label="removeToCreateScrewAndThreadedInsertHole009"
  Angle = 360
  Axis = (0,1,0)
  Base = (0,0,0)
  FaceMakerClass = Part::FaceMakerBullseye
  Placement = pos=(89.5,0,3.5) rot=(0,0,1;0rad)
  Solid = false
  Source = -> Face068
  Symmetric = false
FEATURE [Part::Feature] Face069
  shape: bbox 3.5 x 17.8 x 2e-07 mm, 1 faces, 0 solids (baked)
FEATURE [Part::Feature] Face070
  shape: bbox 3.5 x 17.8 x 2e-07 mm, 1 faces, 0 solids (baked)
FEATURE [Part::Revolution] Revolve073  label="removeToCreateScrewAndThreadedInsertHole010"
  Angle = 360
  Axis = (0,1,0)
  Base = (0,0,0)
  FaceMakerClass = Part::FaceMakerBullseye
  Placement = pos=(102.5,4.7,3.5) rot=(0,0,1;0rad)
  Solid = false
  Source = -> Face069
  Symmetric = false
FEATURE [Part::Revolution] Revolve074  label="removeToCreateScrewAndThreadedInsertHole011"
  Angle = 360
  Axis = (0,1,0)
  Base = (0,0,0)
  FaceMakerClass = Part::FaceMakerBullseye
  Placement = pos=(102.5,4.7,68.5) rot=(0,0,1;0rad)
  Solid = false
  Source = -> Face070
  Symmetric = false
FEATURE [Part::MultiFuse] Fusion048  label="makeHoles001"
  Shapes = -> [Revolve074,Revolve073,Revolve072,Revolve071,Revolve070,Revolve069]
FEATURE [Part::MultiFuse] Fusion049  label="caseScrewRetainers"
  Shapes = -> [Revolve067,Revolve068,Revolve048,Revolve047,Revolve039,Revolve040]
FEATURE [Part::Cut] Cut015  label="caseScrewRetainers001"
  Base = -> Fusion049
  Tool = -> Fusion048
FEATURE [Part::MultiFuse] Fusion050  label="casePillars"
  Shapes = -> [Revolve055,Revolve054,Revolve043,Revolve046,Revolve059,Revolve060]
FEATURE [Part::Feature] Face071 .. Face076  x6 (patterned run collapsed; names and placements below)
  shape: bbox 3.5 x 17.8 x 2e-07 mm, 1 faces, 0 solids (baked)
FEATURE [Part::Revolution] Revolve075  label="removeToCreateScrewAndThreadedInsertHole012"
  Angle = 360
  Axis = (0,1,0)
  Base = (0,0,0)
  FaceMakerClass = Part::FaceMakerBullseye
  Placement = pos=(12.5,0,10) rot=(0,0,1;0rad)
  Solid = false
  Source = -> Face071
  Symmetric = false
FEATURE [Part::Revolution] Revolve076  label="removeToCreateScrewAndThreadedInsertHole013"
  Angle = 360
  Axis = (0,1,0)
  Base = (0,0,0)
  FaceMakerClass = Part::FaceMakerBullseye
  Placement = pos=(12.5,0,62) rot=(0,0,1;0rad)
  Solid = false
  Source = -> Face072
  Symmetric = false
FEATURE [Part::Revolution] Revolve077  label="removeToCreateScrewAndThreadedInsertHole014"
  Angle = 360
  Axis = (0,1,0)
  Base = (0,0,0)
  FaceMakerClass = Part::FaceMakerBullseye
  Placement = pos=(89.5,0,68.5) rot=(0,0,1;0rad)
  Solid = false
  Source = -> Face073
  Symmetric = false
FEATURE [Part::Revolution] Revolve078  label="removeToCreateScrewAndThreadedInsertHole015"
  Angle = 360
  Axis = (0,1,0)
  Base = (0,0,0)
  FaceMakerClass = Part::FaceMakerBullseye
  Placement = pos=(89.5,0,3.5) rot=(0,0,1;0rad)
  Solid = false
  Source = -> Face074
  Symmetric = false
FEATURE [Part::Revolution] Revolve079  label="removeToCreateScrewAndThreadedInsertHole016"
  Angle = 360
  Axis = (0,1,0)
  Base = (0,0,0)
  FaceMakerClass = Part::FaceMakerBullseye
  Placement = pos=(102.5,4.7,3.5) rot=(0,0,1;0rad)
  Solid = false
  Source = -> Face075
  Symmetric = false
FEATURE [Part::Revolution] Revolve080  label="removeToCreateScrewAndThreadedInsertHole017"
  Angle = 360
  Axis = (0,1,0)
  Base = (0,0,0)
  FaceMakerClass = Part::FaceMakerBullseye
  Placement = pos=(102.5,4.7,68.5) rot=(0,0,1;0rad)
  Solid = false
  Source = -> Face076
  Symmetric = false
FEATURE [Part::MultiFuse] Fusion051  label="makeHoles002"
  Shapes = -> [Revolve080,Revolve079,Revolve078,Revolve077,Revolve076,Revolve075]
FEATURE [Part::Cut] Cut016  label="caesPillars"
  Base = -> Fusion050
  Tool = -> Fusion051
FEATURE [Part::Revolution] Revolve009  label="plugHousing016"
  Angle = 360
  Axis = (0,1,0)
  Base = (0,0,0)
  FaceMakerClass = Part::FaceMakerBullseye
  Placement = pos=(0,0,36.15) rot=(0,0,1;0rad)
  Solid = false
  Source = -> Face012
  Symmetric = false
FEATURE [Part::MultiFuse] Fusion014  label="plugHousing023"
  Placement = pos=(0,0,0) rot=(0,0,1;1.5708rad)
  Shapes = -> [Revolve011,Revolve009]
FEATURE [Part::Revolution] Revolve010  label="plugHousing017"
  Angle = 360
  Axis = (0,1,0)
  Base = (0,0,0)
  FaceMakerClass = Part::FaceMakerBullseye
  Placement = pos=(0,0,36.15) rot=(0,0,1;0rad)
  Solid = false
  Source = -> Face014
  Symmetric = false
FEATURE [Part::MultiFuse] Fusion015  label="plugHousing024"
  Placement = pos=(0,0,0) rot=(0,0,1;1.5708rad)
  Shapes = -> [Revolve010,Revolve015]
FEATURE [Part::Revolution] Revolve014  label="plugHousing026"
  Angle = 360
  Axis = (0,1,0)
  Base = (0,0,0)
  FaceMakerClass = Part::FaceMakerBullseye
  Placement = pos=(0,0,36.15) rot=(0,0,1;0rad)
  Solid = false
  Source = -> Face011
  Symmetric = false
FEATURE [Part::Revolution] Revolve013  label="plugHousing025"
  Angle = 360
  Axis = (0,1,0)
  Base = (0,0,0)
  FaceMakerClass = Part::FaceMakerBullseye
  Placement = pos=(0,0,36.15) rot=(0,0,1;0rad)
  Solid = false
  Source = -> Face015
  Symmetric = false
FEATURE [Part::MultiFuse] Fusion016  label="plugHousing028"
  Placement = pos=(0,19,0) rot=(0,0,1;3.14159rad)
  Shapes = -> [Fusion014,Fusion013]
FEATURE [Part::MultiFuse] Fusion011  label="plugHousing018"
  Placement = pos=(0,0,0) rot=(0,0,1;1.5708rad)
  Shapes = -> [Revolve014,Revolve013]
FEATURE [Part::MultiFuse] Fusion012  label="plugHousing019"
  Placement = pos=(0,19,0) rot=(0,0,1;3.14159rad)
  Shapes = -> [Fusion011,Fusion015]
FEATURE [Part::MultiFuse] Fusion017  label="plugHousing029"
  Placement = pos=(122.621,0,-0.15) rot=(0,0,1;0rad)
  Shapes = -> [Fusion016,Fusion012]
FEATURE [Part::MultiFuse] Fusion052  label="casePillarRetainers"
  Shapes = -> [Extrude012,Extrude013,Extrude014,Extrude015,Extrude016,Extrude017,Extrude018,Extrude019,Box011,Box012]
FEATURE [Part::Feature] Face077
  shape: bbox 3.5 x 17.8 x 2e-07 mm, 1 faces, 0 solids (baked)
FEATURE [Part::Revolution] Revolve081  label="removeToCreateScrewAndThreadedInsertHole018"
  Angle = 360
  Axis = (0,1,0)
  Base = (0,0,0)
  FaceMakerClass = Part::FaceMakerBullseye
  Placement = pos=(62.3,30.3,19.7) rot=(0,0,1;0rad)
  Solid = false
  Source = -> Face077
  Symmetric = false
FEATURE [Part::Feature] Face078
  shape: bbox 3.5 x 17.8 x 2e-07 mm, 1 faces, 0 solids (baked)
FEATURE [Part::Revolution] Revolve082  label="removeToCreateScrewAndThreadedInsertHole019"
  Angle = 360
  Axis = (0,1,0)
  Base = (0,0,0)
  FaceMakerClass = Part::FaceMakerBullseye
  Placement = pos=(62.3,30.3,51.7) rot=(0,0,1;0rad)
  Solid = false
  Source = -> Face078
  Symmetric = false
FEATURE [Part::Feature] Face079
  shape: bbox 3.5 x 17.8 x 2e-07 mm, 1 faces, 0 solids (baked)
FEATURE [Part::Revolution] Revolve083  label="removeToCreateScrewAndThreadedInsertHole020"
  Angle = 360
  Axis = (0,1,0)
  Base = (0,0,0)
  FaceMakerClass = Part::FaceMakerBullseye
  Placement = pos=(30.3,30.3,19.7) rot=(0,0,1;0rad)
  Solid = false
  Source = -> Face079
  Symmetric = false
FEATURE [Part::Feature] Face080
  shape: bbox 3.5 x 17.8 x 2e-07 mm, 1 faces, 0 solids (baked)
FEATURE [Part::Revolution] Revolve084  label="removeToCreateScrewAndThreadedInsertHole021"
  Angle = 360
  Axis = (0,1,0)
  Base = (0,0,0)
  FaceMakerClass = Part::FaceMakerBullseye
  Placement = pos=(30.3,30.3,51.7) rot=(0,0,1;0rad)
  Solid = false
  Source = -> Face080
  Symmetric = false
FEATURE [Part::MultiFuse] Fusion053  label="createThreadedInsertHolesForFan"
  Shapes = -> [Revolve081,Revolve082,Revolve083,Revolve084]
FEATURE [Part::Cut] Cut017  label="fanScrewHousing001"
  Base = -> Fusion046
  Tool = -> Fusion053
FEATURE [Part::Feature] Face081
  shape: bbox 3.5 x 17.8 x 2e-07 mm, 1 faces, 0 solids (baked)
FEATURE [Part::Revolution] Revolve085  label="removeToCreateScrewAndThreadedInsertHole022"
  Angle = 360
  Axis = (0,1,0)
  Base = (0,0,0)
  FaceMakerClass = Part::FaceMakerBullseye
  Placement = pos=(62.3,30.3,19.7) rot=(0,0,1;0rad)
  Solid = false
  Source = -> Face081
  Symmetric = false
FEATURE [Part::Feature] Face082
  shape: bbox 3.5 x 17.8 x 2e-07 mm, 1 faces, 0 solids (baked)
FEATURE [Part::Revolution] Revolve086  label="removeToCreateScrewAndThreadedInsertHole023"
  Angle = 360
  Axis = (0,1,0)
  Base = (0,0,0)
  FaceMakerClass = Part::FaceMakerBullseye
  Placement = pos=(62.3,30.3,51.7) rot=(0,0,1;0rad)
  Solid = false
  Source = -> Face082
  Symmetric = false
FEATURE [Part::Feature] Face083
  shape: bbox 3.5 x 17.8 x 2e-07 mm, 1 faces, 0 solids (baked)
FEATURE [Part::Revolution] Revolve087  label="removeToCreateScrewAndThreadedInsertHole024"
  Angle = 360
  Axis = (0,1,0)
  Base = (0,0,0)
  FaceMakerClass = Part::FaceMakerBullseye
  Placement = pos=(30.3,30.3,19.7) rot=(0,0,1;0rad)
  Solid = false
  Source = -> Face083
  Symmetric = false
FEATURE [Part::Feature] Face084
  shape: bbox 3.5 x 17.8 x 2e-07 mm, 1 faces, 0 solids (baked)
FEATURE [Part::Revolution] Revolve088  label="removeToCreateScrewAndThreadedInsertHole025"
  Angle = 360
  Axis = (0,1,0)
  Base = (0,0,0)
  FaceMakerClass = Part::FaceMakerBullseye
  Placement = pos=(30.3,30.3,51.7) rot=(0,0,1;0rad)
  Solid = false
  Source = -> Face084
  Symmetric = false
FEATURE [Part::MultiFuse] Fusion054  label="createThreadedInsertHolesForFan001"
  Shapes = -> [Revolve085,Revolve086,Revolve087,Revolve088]
FEATURE [Part::Cut] Cut018  label="top007"
  Base = -> Fusion040
  Tool = -> Fusion054
FEATURE [Sketcher::SketchObject] Sketch029
  FullyConstrained = false
  Placement = pos=(0,0,0) rot=(1,0,0;1.5708rad)
  sketch-geometry (24):
    g0: ArcOfCircle CenterX=-4 CenterY=-10.5 CenterZ=0 NormalX=0 NormalY=0 NormalZ=1 AngleXU=0 Radius=1.5 StartAngle=6e-16 EndAngle=3.14159
    g1: ArcOfCircle CenterX=-34.2 CenterY=-10.5 CenterZ=0 NormalX=0 NormalY=0 NormalZ=1 AngleXU=0 Radius=1.5 StartAngle=0 EndAngle=3.14159
    g2: ArcOfCircle CenterX=-34.2 CenterY=-27.7 CenterZ=0 NormalX=0 NormalY=0 NormalZ=1 AngleXU=0 Radius=1.5 StartAngle=3.14159 EndAngle=6.28319
    g3: ArcOfCircle CenterX=-4 CenterY=-27.7 CenterZ=0 NormalX=0 NormalY=0 NormalZ=1 AngleXU=0 Radius=1.5 StartAngle=3.1416 EndAngle=6.28319
    g4: ArcOfCircle CenterX=-10 CenterY=-4.3 CenterZ=0 NormalX=0 NormalY=0 NormalZ=1 AngleXU=0 Radius=1.5 StartAngle=2e-16 EndAngle=3.14159
    g5: ArcOfCircle CenterX=-16.1 CenterY=-1.8 CenterZ=0 NormalX=0 NormalY=0 NormalZ=1 AngleXU=0 Radius=1.5 StartAngle=5e-16 EndAngle=3.14159
    g6: ArcOfCircle CenterX=-22.1 CenterY=-1.8 CenterZ=0 NormalX=0 NormalY=0 NormalZ=1 AngleXU=0 Radius=1.5 StartAngle=5e-16 EndAngle=3.14159
    g7: ArcOfCircle CenterX=-28.2 CenterY=-4.3 CenterZ=0 NormalX=0 NormalY=0 NormalZ=1 AngleXU=0 Radius=1.5 StartAngle=2e-16 EndAngle=3.14159
    g8: ArcOfCircle CenterX=-10 CenterY=-33.9 CenterZ=0 NormalX=0 NormalY=0 NormalZ=1 AngleXU=0 Radius=1.5 StartAngle=3.14159 EndAngle=6.28319
    g9: ArcOfCircle CenterX=-16.1 CenterY=-36.4 CenterZ=0 NormalX=0 NormalY=0 NormalZ=1 AngleXU=0 Radius=1.5 StartAngle=3.14159 EndAngle=6.28319
    g10: ArcOfCircle CenterX=-22.1 CenterY=-36.4 CenterZ=0 NormalX=0 NormalY=0 NormalZ=1 AngleXU=0 Radius=1.5 StartAngle=3.14159 EndAngle=6.28319
    g11: ArcOfCircle CenterX=-28.2 CenterY=-33.9 CenterZ=0 NormalX=0 NormalY=0 NormalZ=1 AngleXU=0 Radius=1.5 StartAngle=3.14159 EndAngle=6.28319
    g12: LineSegment StartX=-35.7 StartY=-10.5 StartZ=0 EndX=-35.7 EndY=-27.7 EndZ=0
    g13: LineSegment StartX=-32.7 StartY=-10.5 StartZ=0 EndX=-32.7 EndY=-27.7 EndZ=0
    g14: LineSegment StartX=-29.7 StartY=-33.9 StartZ=0 EndX=-29.7 EndY=-4.3 EndZ=0
    g15: LineSegment StartX=-26.7 StartY=-33.9 StartZ=0 EndX=-26.7 EndY=-4.3 EndZ=0
    g16: LineSegment StartX=-2.5 StartY=-10.5 StartZ=0 EndX=-2.5 EndY=-27.7 EndZ=0
    g17: LineSegment StartX=-8.5 StartY=-4.3 StartZ=0 EndX=-8.5 EndY=-33.9 EndZ=0
    g18: LineSegment StartX=-5.5 StartY=-10.5 StartZ=0 EndX=-5.5 EndY=-27.7 EndZ=0
    g19: LineSegment StartX=-11.5 StartY=-4.3 StartZ=0 EndX=-11.5 EndY=-33.9 EndZ=0
    g20: LineSegment StartX=-14.6 StartY=-1.8 StartZ=0 EndX=-14.6 EndY=-36.4 EndZ=0
    g21: LineSegment StartX=-17.6 StartY=-1.8 StartZ=0 EndX=-17.6 EndY=-36.4 EndZ=0
    g22: LineSegment StartX=-20.6 StartY=-36.4 StartZ=0 EndX=-20.6 EndY=-1.8 EndZ=0
    g23: LineSegment StartX=-23.6 StartY=-1.8 StartZ=0 EndX=-23.6 EndY=-36.4 EndZ=0
  constraints (48):
    c: Block(g0)
    c: Block(g1)
    c: Block(g2)
    c: Block(g3)
    c: Block(g4)
    c: Block(g5)
    c: Block(g6)
    c: Block(g7)
    c: Block(g8)
    c: Block(g9)
    c: Block(g10)
    c: Block(g11)
    c: Coincident(g12,g1)
    c: Coincident(g12,g2)
    c: Vertical(g12)
    c: Coincident(g13,g1)
    c: Coincident(g13,g2)
    c: Vertical(g13)
    c: Coincident(g14,g11)
    c: Coincident(g14,g7)
    c: Vertical(g14)
    c: Coincident(g15,g11)
    c: Coincident(g15,g7)
    c: Vertical(g15)
    c: Coincident(g16,g0)
    c: Coincident(g16,g3)
    c: Vertical(g16)
    c: Coincident(g17,g4)
    c: Coincident(g17,g8)
    c: Vertical(g17)
    c: Coincident(g18,g0)
    c: Coincident(g18,g3)
    c: Vertical(g18)
    c: Coincident(g19,g4)
    c: Coincident(g19,g8)
    c: Vertical(g19)
    c: Coincident(g20,g5)
    c: Coincident(g20,g9)
    c: Vertical(g20)
    c: Coincident(g21,g5)
    c: Coincident(g21,g9)
    c: Vertical(g21)
    c: Coincident(g22,g10)
    c: Coincident(g22,g6)
    c: Vertical(g22)
    c: Coincident(g23,g6)
    c: Coincident(g23,g10)
    c: Vertical(g23)
FEATURE [Part::Extrusion] Extrude020  label="removeToCreateFanGrillHoles"
  Base = -> Sketch029
  Dir = (0,-1,6e-16)
  DirMode = 2
  FaceMakerClass = Part::FaceMakerBullseye
  LengthFwd = 10
  LengthRev = 0
  Placement = pos=(65.4,44,54.82) rot=(0,0,1;0rad)
  Solid = true
  Symmetric = false
FEATURE [Part::MultiFuse] Fusion055  label="top008"
  Shapes = -> [Cut017,Cut018]
FEATURE [Part::Cut] Cut019  label="top009"
  Base = -> Fusion055
  Tool = -> Extrude020
FEATURE [App::MeasureDistance] Distance003  label="Distance: 71.95 mm"
  Distance = 71.9513
  P1 = (117,38,72)
  P2 = (117,38,0.0487319)
FEATURE [Sketcher::SketchObject] Sketch030
  FullyConstrained = true
  Placement = pos=(117,19,0) rot=(0.57735,0.57735,0.57735;2.0944rad)
  sketch-geometry (48):
    g0: LineSegment StartX=-49.19 StartY=69.25 StartZ=0 EndX=-49.19 EndY=66.25 EndZ=0
    g1: LineSegment StartX=-49.19 StartY=63.5 StartZ=0 EndX=-49.19 EndY=60.5 EndZ=0
    g2: LineSegment StartX=-49.19 StartY=57.75 StartZ=0 EndX=-49.19 EndY=54.75 EndZ=0
    g3: LineSegment StartX=-49.19 StartY=52 StartZ=0 EndX=-49.19 EndY=49 EndZ=0
    g4: LineSegment StartX=-49.19 StartY=46.25 StartZ=0 EndX=-49.19 EndY=43.25 EndZ=0
    g5: LineSegment StartX=-49.19 StartY=40.5 StartZ=0 EndX=-49.19 EndY=37.5 EndZ=0
    g6: LineSegment StartX=-49.19 StartY=34.5 StartZ=0 EndX=-49.19 EndY=31.5 EndZ=0
    g7: LineSegment StartX=-49.19 StartY=28.75 StartZ=0 EndX=-49.19 EndY=25.75 EndZ=0
    g8: LineSegment StartX=-49.19 StartY=23 StartZ=0 EndX=-49.19 EndY=20 EndZ=0
    g9: LineSegment StartX=-49.19 StartY=17.25 StartZ=0 EndX=-49.19 EndY=14.25 EndZ=0
    g10: LineSegment StartX=-49.19 StartY=11.5 StartZ=0 EndX=-49.19 EndY=8.5 EndZ=0
    g11: LineSegment StartX=-49.19 StartY=5.75 StartZ=0 EndX=-49.19 EndY=2.75 EndZ=0
    g12: ArcOfCircle CenterX=-1.5 CenterY=67.75 CenterZ=0 NormalX=0 NormalY=0 NormalZ=1 AngleXU=0 Radius=1.5 StartAngle=4.71239 EndAngle=7.85398
    g13: ArcOfCircle CenterX=-1.5 CenterY=62 CenterZ=0 NormalX=0 NormalY=0 NormalZ=1 AngleXU=0 Radius=1.5 StartAngle=4.71239 EndAngle=7.85398
    g14: ArcOfCircle CenterX=-1.5 CenterY=56.25 CenterZ=0 NormalX=0 NormalY=0 NormalZ=1 AngleXU=0 Radius=1.5 StartAngle=4.71239 EndAngle=7.85398
    g15: ArcOfCircle CenterX=-11.49 CenterY=50.5 CenterZ=0 NormalX=0 NormalY=0 NormalZ=1 AngleXU=0 Radius=1.5 StartAngle=4.71239 EndAngle=7.85398
    g16: ArcOfCircle CenterX=-16.28 CenterY=44.75 CenterZ=0 NormalX=0 NormalY=0 NormalZ=1 AngleXU=0 Radius=1.5 StartAngle=4.71239 EndAngle=7.85398
    g17: ArcOfCircle CenterX=-18.2337 CenterY=39 CenterZ=0 NormalX=0 NormalY=0 NormalZ=1 AngleXU=0 Radius=1.5 StartAngle=4.71485 EndAngle=7.85398
    g18: ArcOfCircle CenterX=-16.2837 CenterY=27.25 CenterZ=0 NormalX=0 NormalY=0 NormalZ=1 AngleXU=0 Radius=1.5 StartAngle=4.71485 EndAngle=7.85398
    g19: ArcOfCircle CenterX=-18.2337 CenterY=33 CenterZ=0 NormalX=0 NormalY=0 NormalZ=1 AngleXU=0 Radius=1.5 StartAngle=4.71485 EndAngle=7.85398
    g20: ArcOfCircle CenterX=-11.49 CenterY=21.5 CenterZ=0 NormalX=0 NormalY=0 NormalZ=1 AngleXU=0 Radius=1.5 StartAngle=4.71239 EndAngle=7.85398
    g21: ArcOfCircle CenterX=-1.5 CenterY=4.25 CenterZ=0 NormalX=0 NormalY=0 NormalZ=1 AngleXU=0 Radius=1.5 StartAngle=4.71239 EndAngle=7.85398
    g22: ArcOfCircle CenterX=-1.5 CenterY=10 CenterZ=0 NormalX=0 NormalY=0 NormalZ=1 AngleXU=0 Radius=1.5 StartAngle=4.71239 EndAngle=7.85398
    g23: ArcOfCircle CenterX=-1.5 CenterY=15.75 CenterZ=0 NormalX=0 NormalY=0 NormalZ=1 AngleXU=0 Radius=1.5 StartAngle=4.71239 EndAngle=7.85398
    g24: LineSegment StartX=-49.19 StartY=69.25 StartZ=0 EndX=-1.5 EndY=69.25 EndZ=0
    g25: LineSegment StartX=-49.19 StartY=66.25 StartZ=0 EndX=-1.5 EndY=66.25 EndZ=0
    g26: LineSegment StartX=-49.19 StartY=63.5 StartZ=0 EndX=-1.5 EndY=63.5 EndZ=0
    g27: LineSegment StartX=-49.19 StartY=60.5 StartZ=0 EndX=-1.5 EndY=60.5 EndZ=0
    g28: LineSegment StartX=-49.19 StartY=57.75 StartZ=0 EndX=-1.5 EndY=57.75 EndZ=0
    g29: LineSegment StartX=-49.19 StartY=54.75 StartZ=0 EndX=-1.5 EndY=54.75 EndZ=0
    g30: LineSegment StartX=-49.19 StartY=52 StartZ=0 EndX=-11.49 EndY=52 EndZ=0
    g31: LineSegment StartX=-49.19 StartY=49 StartZ=0 EndX=-11.49 EndY=49 EndZ=0
    g32: LineSegment StartX=-49.19 StartY=46.25 StartZ=0 EndX=-16.28 EndY=46.25 EndZ=0
    g33: LineSegment StartX=-49.19 StartY=43.25 StartZ=0 EndX=-16.28 EndY=43.25 EndZ=0
    g34: LineSegment StartX=-49.19 StartY=40.5 StartZ=0 EndX=-18.2337 EndY=40.5 EndZ=0
    g35: LineSegment StartX=-49.19 StartY=37.5 StartZ=0 EndX=-18.23 EndY=37.5 EndZ=0
    g36: LineSegment StartX=-49.19 StartY=34.5 StartZ=0 EndX=-18.2337 EndY=34.5 EndZ=0
    g37: LineSegment StartX=-49.19 StartY=31.5 StartZ=0 EndX=-18.23 EndY=31.5 EndZ=0
    g38: LineSegment StartX=-49.19 StartY=28.75 StartZ=0 EndX=-16.2837 EndY=28.75 EndZ=0
    g39: LineSegment StartX=-49.19 StartY=25.75 StartZ=0 EndX=-16.28 EndY=25.75 EndZ=0
    g40: LineSegment StartX=-49.19 StartY=23 StartZ=0 EndX=-11.49 EndY=23 EndZ=0
    g41: LineSegment StartX=-49.19 StartY=20 StartZ=0 EndX=-11.49 EndY=20 EndZ=0
    g42: LineSegment StartX=-49.19 StartY=17.25 StartZ=0 EndX=-1.5 EndY=17.25 EndZ=0
    g43: LineSegment StartX=-49.19 StartY=14.25 StartZ=0 EndX=-1.5 EndY=14.25 EndZ=0
    g44: LineSegment StartX=-49.19 StartY=11.5 StartZ=0 EndX=-1.5 EndY=11.5 EndZ=0
    g45: LineSegment StartX=-49.19 StartY=8.5 StartZ=0 EndX=-1.5 EndY=8.5 EndZ=0
    g46: LineSegment StartX=-49.19 StartY=5.75 StartZ=0 EndX=-1.5 EndY=5.75 EndZ=0
    g47: LineSegment StartX=-49.19 StartY=2.75 StartZ=0 EndX=-1.5 EndY=2.75 EndZ=0
  constraints (120):
    c: Vertical(g0)
    c: Distance(g0) = 3
    c: Block(g0)
    c: Vertical(g1)
    c: Distance(g1) = 3
    c: Vertical(g2)
    c: Equal(g0,g2) = 3
    c: Block(g2)
    c: Vertical(g3)
    c: Equal(g1,g3) = 3
    c: Vertical(g4)
    c: Equal(g0,g4) = 3
    c: Block(g4)
    c: Vertical(g5)
    c: Equal(g1,g5) = 3
    c: Vertical(g6)
    c: Equal(g0,g6) = 3
    c: Block(g6)
    c: Vertical(g7)
    c: Equal(g1,g7) = 3
    c: Vertical(g8)
    c: Equal(g0,g8) = 3
    c: Block(g8)
    c: Vertical(g9)
    c: Equal(g1,g9) = 3
    c: Vertical(g10)
    c: Equal(g0,g10) = 3
    c: Block(g10)
    c: Vertical(g11)
    c: Equal(g1,g11) = 3
    c: Block(g12)
    c: Block(g13)
    c: Block(g14)
    c: Block(g15)
    c: Block(g16)
    c: Block(g17)
    c: Block(g18)
    c: Block(g19)
    c: Block(g20)
    c: Block(g21)
    c: Block(g22)
    c: Block(g23)
    c: Block(g11)
    c: Block(g9)
    c: Block(g7)
    c: Block(g5)
    c: Block(g3)
    c: Block(g1)
    c: Coincident(g24,g0)
    c: Coincident(g24,g12)
    c: Horizontal(g24)
    c: Coincident(g25,g0)
    c: Coincident(g25,g12)
    c: Horizontal(g25)
    c: Coincident(g26,g1)
    c: Coincident(g26,g13)
    c: Horizontal(g26)
    c: Coincident(g27,g1)
    c: Coincident(g27,g13)
    c: Horizontal(g27)
    c: Coincident(g28,g2)
    c: Coincident(g28,g14)
    c: Horizontal(g28)
    c: Coincident(g29,g2)
    c: Coincident(g29,g14)
    c: Horizontal(g29)
    c: Coincident(g30,g3)
    c: Coincident(g30,g15)
    c: Horizontal(g30)
    c: Coincident(g31,g3)
    c: Coincident(g31,g15)
    c: Horizontal(g31)
    c: Coincident(g32,g4)
    c: Coincident(g32,g16)
    c: Horizontal(g32)
    c: Coincident(g33,g4)
    c: Coincident(g33,g16)
    c: Horizontal(g33)
    c: Coincident(g34,g5)
    c: Coincident(g34,g17)
    c: Horizontal(g34)
    c: Coincident(g35,g5)
    c: Coincident(g35,g17)
    c: Horizontal(g35)
    c: Coincident(g36,g6)
    c: Coincident(g36,g19)
    c: Horizontal(g36)
    c: Coincident(g37,g6)
    c: Coincident(g37,g19)
    c: Horizontal(g37)
    c: Coincident(g38,g7)
    c: Coincident(g38,g18)
    c: Horizontal(g38)
    c: Coincident(g39,g7)
    c: Coincident(g39,g18)
    c: Horizontal(g39)
    c: Coincident(g40,g8)
    c: Coincident(g40,g20)
    c: Horizontal(g40)
    c: Coincident(g41,g8)
    c: Coincident(g41,g20)
    c: Horizontal(g41)
    c: Coincident(g42,g9)
    c: Coincident(g42,g23)
    c: Horizontal(g42)
    c: Coincident(g43,g9)
    c: Coincident(g43,g23)
    c: Horizontal(g43)
    c: Coincident(g44,g10)
    c: Coincident(g44,g22)
    c: Horizontal(g44)
    c: Coincident(g45,g10)
    c: Coincident(g45,g22)
    c: Horizontal(g45)
    c: Coincident(g46,g11)
    c: Coincident(g46,g21)
    c: Horizontal(g46)
    c: Coincident(g47,g11)
    c: Coincident(g47,g21)
    c: Horizontal(g47)
FEATURE [Sketcher::SketchObject] Sketch031
  FullyConstrained = true
  Placement = pos=(117,19,0) rot=(0.57735,0.57735,0.57735;2.0944rad)
  sketch-geometry (24):
    g0: ArcOfCircle CenterX=-49.19 CenterY=67.75 CenterZ=0 NormalX=0 NormalY=0 NormalZ=1 AngleXU=0 Radius=1.5 StartAngle=1.5708 EndAngle=4.71239
    g1: ArcOfCircle CenterX=-49.19 CenterY=62 CenterZ=0 NormalX=0 NormalY=0 NormalZ=1 AngleXU=0 Radius=1.5 StartAngle=1.5708 EndAngle=4.71239
    g2: ArcOfCircle CenterX=-49.19 CenterY=56.25 CenterZ=0 NormalX=0 NormalY=0 NormalZ=1 AngleXU=0 Radius=1.5 StartAngle=1.5708 EndAngle=4.71239
    g3: ArcOfCircle CenterX=-49.19 CenterY=50.5 CenterZ=0 NormalX=0 NormalY=0 NormalZ=1 AngleXU=0 Radius=1.5 StartAngle=1.5708 EndAngle=4.71239
    g4: ArcOfCircle CenterX=-49.19 CenterY=44.75 CenterZ=0 NormalX=0 NormalY=0 NormalZ=1 AngleXU=0 Radius=1.5 StartAngle=1.5708 EndAngle=4.71239
    g5: ArcOfCircle CenterX=-49.19 CenterY=39 CenterZ=0 NormalX=0 NormalY=0 NormalZ=1 AngleXU=0 Radius=1.5 StartAngle=1.5708 EndAngle=4.71239
    g6: ArcOfCircle CenterX=-49.19 CenterY=33 CenterZ=0 NormalX=0 NormalY=0 NormalZ=1 AngleXU=0 Radius=1.5 StartAngle=1.5708 EndAngle=4.71239
    g7: ArcOfCircle CenterX=-49.19 CenterY=27.25 CenterZ=0 NormalX=0 NormalY=0 NormalZ=1 AngleXU=0 Radius=1.5 StartAngle=1.5708 EndAngle=4.71239
    g8: ArcOfCircle CenterX=-49.19 CenterY=21.5 CenterZ=0 NormalX=0 NormalY=0 NormalZ=1 AngleXU=0 Radius=1.5 StartAngle=1.5708 EndAngle=4.71239
    g9: ArcOfCircle CenterX=-49.19 CenterY=15.75 CenterZ=0 NormalX=0 NormalY=0 NormalZ=1 AngleXU=0 Radius=1.5 StartAngle=1.5708 EndAngle=4.71239
    g10: ArcOfCircle CenterX=-49.19 CenterY=10 CenterZ=0 NormalX=0 NormalY=0 NormalZ=1 AngleXU=0 Radius=1.5 StartAngle=1.5708 EndAngle=4.71239
    g11: ArcOfCircle CenterX=-49.19 CenterY=4.25 CenterZ=0 NormalX=0 NormalY=0 NormalZ=1 AngleXU=0 Radius=1.5 StartAngle=1.5708 EndAngle=4.71239
    g12: LineSegment StartX=-49.19 StartY=69.25 StartZ=0 EndX=-49.19 EndY=66.25 EndZ=0
    g13: LineSegment StartX=-49.19 StartY=63.5 StartZ=0 EndX=-49.19 EndY=60.5 EndZ=0
    g14: LineSegment StartX=-49.19 StartY=57.75 StartZ=0 EndX=-49.19 EndY=54.75 EndZ=0
    g15: LineSegment StartX=-49.19 StartY=52 StartZ=0 EndX=-49.19 EndY=49 EndZ=0
    g16: LineSegment StartX=-49.19 StartY=46.25 StartZ=0 EndX=-49.19 EndY=43.25 EndZ=0
    g17: LineSegment StartX=-49.19 StartY=40.5 StartZ=0 EndX=-49.19 EndY=37.5 EndZ=0
    g18: LineSegment StartX=-49.19 StartY=34.5 StartZ=0 EndX=-49.19 EndY=31.5 EndZ=0
    g19: LineSegment StartX=-49.19 StartY=28.75 StartZ=0 EndX=-49.19 EndY=25.75 EndZ=0
    g20: LineSegment StartX=-49.19 StartY=23 StartZ=0 EndX=-49.19 EndY=20 EndZ=0
    g21: LineSegment StartX=-49.19 StartY=17.25 StartZ=0 EndX=-49.19 EndY=14.25 EndZ=0
    g22: LineSegment StartX=-49.19 StartY=11.5 StartZ=0 EndX=-49.19 EndY=8.5 EndZ=0
    g23: LineSegment StartX=-49.19 StartY=5.75 StartZ=0 EndX=-49.19 EndY=2.75 EndZ=0
  constraints (48):
    c: Block(g0)
    c: Block(g1)
    c: Block(g2)
    c: Block(g3)
    c: Block(g4)
    c: Block(g5)
    c: Block(g6)
    c: Block(g7)
    c: Block(g8)
    c: Block(g9)
    c: Block(g10)
    c: Block(g11)
    c: Coincident(g12,g0)
    c: Coincident(g12,g0)
    c: Vertical(g12)
    c: Vertical(g13)
    c: Coincident(g13,g1)
    c: Vertical(g14)
    c: Coincident(g14,g2)
    c: Vertical(g15)
    c: Coincident(g15,g3)
    c: Vertical(g16)
    c: Coincident(g16,g4)
    c: Vertical(g17)
    c: Coincident(g17,g5)
    c: Vertical(g18)
    c: Coincident(g18,g6)
    c: Vertical(g19)
    c: Coincident(g19,g7)
    c: Vertical(g20)
    c: Coincident(g20,g8)
    c: Vertical(g21)
    c: Coincident(g21,g9)
    c: Vertical(g22)
    c: Coincident(g22,g10)
    c: Vertical(g23)
    c: Coincident(g23,g11)
    c: Block(g23)
    c: Block(g22)
    c: Block(g21)
    c: Block(g20)
    c: Block(g13)
    c: Block(g14)
    c: Block(g15)
    c: Block(g16)
    c: Block(g17)
    c: Block(g18)
    c: Block(g19)
FEATURE [Part::Extrusion] Extrude022
  Base = -> Sketch030
  Dir = (1,-2e-16,2e-16)
  DirMode = 2
  FaceMakerClass = Part::FaceMakerBullseye
  LengthFwd = 19
  LengthRev = 0
  Placement = pos=(-19,0,0) rot=(0,0,1;0rad)
  Solid = true
  Symmetric = false
FEATURE [Part::Fillet] Fillet022
  Base = -> Extrude022
  Edges = 24 edges r=1.49: [Edge6,Edge11,Edge18,Edge23,Edge30,Edge35,Edge42,Edge47,Edge54,Edge59,Edge66,Edge71,Edge78,Edge83,Edge90,Edge95,Edge102,Edge107,Edge114,Edge119,Edge126,Edge131,Edge138,Edge143]
FEATURE [Part::Cut] Cut020  label="top010"
  Base = -> Cut019
  Tool = -> Fillet022
FEATURE [Sketcher::SketchObject] Sketch032
  FullyConstrained = true
  Placement = pos=(117,19,0) rot=(0.57735,0.57735,0.57735;2.0944rad)
  sketch-geometry (48):
    g0: LineSegment StartX=-49.19 StartY=69.25 StartZ=0 EndX=-49.19 EndY=66.25 EndZ=0
    g1: LineSegment StartX=-49.19 StartY=63.5 StartZ=0 EndX=-49.19 EndY=60.5 EndZ=0
    g2: LineSegment StartX=-49.19 StartY=57.75 StartZ=0 EndX=-49.19 EndY=54.75 EndZ=0
    g3: LineSegment StartX=-49.19 StartY=52 StartZ=0 EndX=-49.19 EndY=49 EndZ=0
    g4: LineSegment StartX=-49.19 StartY=46.25 StartZ=0 EndX=-49.19 EndY=43.25 EndZ=0
    g5: LineSegment StartX=-49.19 StartY=40.5 StartZ=0 EndX=-49.19 EndY=37.5 EndZ=0
    g6: LineSegment StartX=-49.19 StartY=34.5 StartZ=0 EndX=-49.19 EndY=31.5 EndZ=0
    g7: LineSegment StartX=-49.19 StartY=28.75 StartZ=0 EndX=-49.19 EndY=25.75 EndZ=0
    g8: LineSegment StartX=-49.19 StartY=23 StartZ=0 EndX=-49.19 EndY=20 EndZ=0
    g9: LineSegment StartX=-49.19 StartY=17.25 StartZ=0 EndX=-49.19 EndY=14.25 EndZ=0
    g10: LineSegment StartX=-49.19 StartY=11.5 StartZ=0 EndX=-49.19 EndY=8.5 EndZ=0
    g11: LineSegment StartX=-49.19 StartY=5.75 StartZ=0 EndX=-49.19 EndY=2.75 EndZ=0
    g12: ArcOfCircle CenterX=-1.5 CenterY=67.75 CenterZ=0 NormalX=0 NormalY=0 NormalZ=1 AngleXU=0 Radius=1.5 StartAngle=4.71239 EndAngle=7.85398
    g13: ArcOfCircle CenterX=-1.5 CenterY=62 CenterZ=0 NormalX=0 NormalY=0 NormalZ=1 AngleXU=0 Radius=1.5 StartAngle=4.71239 EndAngle=7.85398
    g14: ArcOfCircle CenterX=-1.5 CenterY=56.25 CenterZ=0 NormalX=0 NormalY=0 NormalZ=1 AngleXU=0 Radius=1.5 StartAngle=4.71239 EndAngle=7.85398
    g15: ArcOfCircle CenterX=-11.49 CenterY=50.5 CenterZ=0 NormalX=0 NormalY=0 NormalZ=1 AngleXU=0 Radius=1.5 StartAngle=4.71239 EndAngle=7.85398
    g16: ArcOfCircle CenterX=-16.28 CenterY=44.75 CenterZ=0 NormalX=0 NormalY=0 NormalZ=1 AngleXU=0 Radius=1.5 StartAngle=4.71239 EndAngle=7.85398
    g17: ArcOfCircle CenterX=-18.2337 CenterY=39 CenterZ=0 NormalX=0 NormalY=0 NormalZ=1 AngleXU=0 Radius=1.5 StartAngle=4.71485 EndAngle=7.85398
    g18: ArcOfCircle CenterX=-16.2837 CenterY=27.25 CenterZ=0 NormalX=0 NormalY=0 NormalZ=1 AngleXU=0 Radius=1.5 StartAngle=4.71485 EndAngle=7.85398
    g19: ArcOfCircle CenterX=-18.2337 CenterY=33 CenterZ=0 NormalX=0 NormalY=0 NormalZ=1 AngleXU=0 Radius=1.5 StartAngle=4.71485 EndAngle=7.85398
    g20: ArcOfCircle CenterX=-11.49 CenterY=21.5 CenterZ=0 NormalX=0 NormalY=0 NormalZ=1 AngleXU=0 Radius=1.5 StartAngle=4.71239 EndAngle=7.85398
    g21: ArcOfCircle CenterX=-1.5 CenterY=4.25 CenterZ=0 NormalX=0 NormalY=0 NormalZ=1 AngleXU=0 Radius=1.5 StartAngle=4.71239 EndAngle=7.85398
    g22: ArcOfCircle CenterX=-1.5 CenterY=10 CenterZ=0 NormalX=0 NormalY=0 NormalZ=1 AngleXU=0 Radius=1.5 StartAngle=4.71239 EndAngle=7.85398
    g23: ArcOfCircle CenterX=-1.5 CenterY=15.75 CenterZ=0 NormalX=0 NormalY=0 NormalZ=1 AngleXU=0 Radius=1.5 StartAngle=4.71239 EndAngle=7.85398
    g24: LineSegment StartX=-49.19 StartY=69.25 StartZ=0 EndX=-1.5 EndY=69.25 EndZ=0
    g25: LineSegment StartX=-49.19 StartY=66.25 StartZ=0 EndX=-1.5 EndY=66.25 EndZ=0
    g26: LineSegment StartX=-49.19 StartY=63.5 StartZ=0 EndX=-1.5 EndY=63.5 EndZ=0
    g27: LineSegment StartX=-49.19 StartY=60.5 StartZ=0 EndX=-1.5 EndY=60.5 EndZ=0
    g28: LineSegment StartX=-49.19 StartY=57.75 StartZ=0 EndX=-1.5 EndY=57.75 EndZ=0
    g29: LineSegment StartX=-49.19 StartY=54.75 StartZ=0 EndX=-1.5 EndY=54.75 EndZ=0
    g30: LineSegment StartX=-49.19 StartY=52 StartZ=0 EndX=-11.49 EndY=52 EndZ=0
    g31: LineSegment StartX=-49.19 StartY=49 StartZ=0 EndX=-11.49 EndY=49 EndZ=0
    g32: LineSegment StartX=-49.19 StartY=46.25 StartZ=0 EndX=-16.28 EndY=46.25 EndZ=0
    g33: LineSegment StartX=-49.19 StartY=43.25 StartZ=0 EndX=-16.28 EndY=43.25 EndZ=0
    g34: LineSegment StartX=-49.19 StartY=40.5 StartZ=0 EndX=-18.2337 EndY=40.5 EndZ=0
    g35: LineSegment StartX=-49.19 StartY=37.5 StartZ=0 EndX=-18.23 EndY=37.5 EndZ=0
    g36: LineSegment StartX=-49.19 StartY=34.5 StartZ=0 EndX=-18.2337 EndY=34.5 EndZ=0
    g37: LineSegment StartX=-49.19 StartY=31.5 StartZ=0 EndX=-18.23 EndY=31.5 EndZ=0
    g38: LineSegment StartX=-49.19 StartY=28.75 StartZ=0 EndX=-16.2837 EndY=28.75 EndZ=0
    g39: LineSegment StartX=-49.19 StartY=25.75 StartZ=0 EndX=-16.28 EndY=25.75 EndZ=0
    g40: LineSegment StartX=-49.19 StartY=23 StartZ=0 EndX=-11.49 EndY=23 EndZ=0
    g41: LineSegment StartX=-49.19 StartY=20 StartZ=0 EndX=-11.49 EndY=20 EndZ=0
    g42: LineSegment StartX=-49.19 StartY=17.25 StartZ=0 EndX=-1.5 EndY=17.25 EndZ=0
    g43: LineSegment StartX=-49.19 StartY=14.25 StartZ=0 EndX=-1.5 EndY=14.25 EndZ=0
    g44: LineSegment StartX=-49.19 StartY=11.5 StartZ=0 EndX=-1.5 EndY=11.5 EndZ=0
    g45: LineSegment StartX=-49.19 StartY=8.5 StartZ=0 EndX=-1.5 EndY=8.5 EndZ=0
    g46: LineSegment StartX=-49.19 StartY=5.75 StartZ=0 EndX=-1.5 EndY=5.75 EndZ=0
    g47: LineSegment StartX=-49.19 StartY=2.75 StartZ=0 EndX=-1.5 EndY=2.75 EndZ=0
  constraints (120):
    c: Vertical(g0)
    c: Distance(g0) = 3
    c: Block(g0)
    c: Vertical(g1)
    c: Distance(g1) = 3
    c: Vertical(g2)
    c: Equal(g0,g2) = 3
    c: Block(g2)
    c: Vertical(g3)
    c: Equal(g1,g3) = 3
    c: Vertical(g4)
    c: Equal(g0,g4) = 3
    c: Block(g4)
    c: Vertical(g5)
    c: Equal(g1,g5) = 3
    c: Vertical(g6)
    c: Equal(g0,g6) = 3
    c: Block(g6)
    c: Vertical(g7)
    c: Equal(g1,g7) = 3
    c: Vertical(g8)
    c: Equal(g0,g8) = 3
    c: Block(g8)
    c: Vertical(g9)
    c: Equal(g1,g9) = 3
    c: Vertical(g10)
    c: Equal(g0,g10) = 3
    c: Block(g10)
    c: Vertical(g11)
    c: Equal(g1,g11) = 3
    c: Block(g12)
    c: Block(g13)
    c: Block(g14)
    c: Block(g15)
    c: Block(g16)
    c: Block(g17)
    c: Block(g18)
    c: Block(g19)
    c: Block(g20)
    c: Block(g21)
    c: Block(g22)
    c: Block(g23)
    c: Block(g11)
    c: Block(g9)
    c: Block(g7)
    c: Block(g5)
    c: Block(g3)
    c: Block(g1)
    c: Coincident(g24,g0)
    c: Coincident(g24,g12)
    c: Horizontal(g24)
    c: Coincident(g25,g0)
    c: Coincident(g25,g12)
    c: Horizontal(g25)
    c: Coincident(g26,g1)
    c: Coincident(g26,g13)
    c: Horizontal(g26)
    c: Coincident(g27,g1)
    c: Coincident(g27,g13)
    c: Horizontal(g27)
    c: Coincident(g28,g2)
    c: Coincident(g28,g14)
    c: Horizontal(g28)
    c: Coincident(g29,g2)
    c: Coincident(g29,g14)
    c: Horizontal(g29)
    c: Coincident(g30,g3)
    c: Coincident(g30,g15)
    c: Horizontal(g30)
    c: Coincident(g31,g3)
    c: Coincident(g31,g15)
    c: Horizontal(g31)
    c: Coincident(g32,g4)
    c: Coincident(g32,g16)
    c: Horizontal(g32)
    c: Coincident(g33,g4)
    c: Coincident(g33,g16)
    c: Horizontal(g33)
    c: Coincident(g34,g5)
    c: Coincident(g34,g17)
    c: Horizontal(g34)
    c: Coincident(g35,g5)
    c: Coincident(g35,g17)
    c: Horizontal(g35)
    c: Coincident(g36,g6)
    c: Coincident(g36,g19)
    c: Horizontal(g36)
    c: Coincident(g37,g6)
    c: Coincident(g37,g19)
    c: Horizontal(g37)
    c: Coincident(g38,g7)
    c: Coincident(g38,g18)
    c: Horizontal(g38)
    c: Coincident(g39,g7)
    c: Coincident(g39,g18)
    c: Horizontal(g39)
    c: Coincident(g40,g8)
    c: Coincident(g40,g20)
    c: Horizontal(g40)
    c: Coincident(g41,g8)
    c: Coincident(g41,g20)
    c: Horizontal(g41)
    c: Coincident(g42,g9)
    c: Coincident(g42,g23)
    c: Horizontal(g42)
    c: Coincident(g43,g9)
    c: Coincident(g43,g23)
    c: Horizontal(g43)
    c: Coincident(g44,g10)
    c: Coincident(g44,g22)
    c: Horizontal(g44)
    c: Coincident(g45,g10)
    c: Coincident(g45,g22)
    c: Horizontal(g45)
    c: Coincident(g46,g11)
    c: Coincident(g46,g21)
    c: Horizontal(g46)
    c: Coincident(g47,g11)
    c: Coincident(g47,g21)
    c: Horizontal(g47)
FEATURE [Part::Extrusion] Extrude023
  Base = -> Sketch032
  Dir = (1,-2e-16,2e-16)
  DirMode = 2
  FaceMakerClass = Part::FaceMakerBullseye
  LengthFwd = 19
  LengthRev = 0
  Placement = pos=(-19,0,0) rot=(0,0,1;0rad)
  Solid = true
  Symmetric = false
FEATURE [Part::Fillet] Fillet023
  Base = -> Extrude023
  Edges = <same value as first occurrence — deduplicated (x4 in doc)>
  Placement = pos=(0,0.05,0) rot=(0,0,1;0rad)
FEATURE [Part::Cut] Cut014  label="bottom003"
  Base = -> Cut007
  Tool = -> Fusion047
FEATURE [Part::Cut] Cut021  label="bottom004"
  Base = -> Cut014
  Tool = -> Fillet023
FEATURE [Sketcher::SketchObject] Sketch033
  FullyConstrained = true
  Placement = pos=(117,19,0) rot=(0.57735,0.57735,0.57735;2.0944rad)
  sketch-geometry (8):
    g0: LineSegment StartX=-49.19 StartY=69.25 StartZ=0 EndX=-49.19 EndY=66.25 EndZ=0
    g1: LineSegment StartX=-49.19 StartY=5.75 StartZ=0 EndX=-49.19 EndY=2.75 EndZ=0
    g2: ArcOfCircle CenterX=-1.5 CenterY=67.75 CenterZ=0 NormalX=0 NormalY=0 NormalZ=1 AngleXU=0 Radius=1.5 StartAngle=4.71239 EndAngle=7.85398
    g3: ArcOfCircle CenterX=-1.5 CenterY=4.25 CenterZ=0 NormalX=0 NormalY=0 NormalZ=1 AngleXU=0 Radius=1.5 StartAngle=4.71239 EndAngle=7.85398
    g4: LineSegment StartX=-49.19 StartY=69.25 StartZ=0 EndX=-1.5 EndY=69.25 EndZ=0
    g5: LineSegment StartX=-49.19 StartY=66.25 StartZ=0 EndX=-1.5 EndY=66.25 EndZ=0
    g6: LineSegment StartX=-49.19 StartY=5.75 StartZ=0 EndX=-1.5 EndY=5.75 EndZ=0
    g7: LineSegment StartX=-49.19 StartY=2.75 StartZ=0 EndX=-1.5 EndY=2.75 EndZ=0
  constraints (19):
    c: Vertical(g0)
    c: Distance(g0) = 3
    c: Block(g0)
    c: Vertical(g1)
    c: Block(g2)
    c: Block(g3)
    c: Block(g1)
    c: Coincident(g4,g0)
    c: Coincident(g4,g2)
    c: Horizontal(g4)
    c: Coincident(g5,g0)
    c: Coincident(g5,g2)
    c: Horizontal(g5)
    c: Coincident(g6,g1)
    c: Coincident(g6,g3)
    c: Horizontal(g6)
    c: Coincident(g7,g1)
    c: Coincident(g7,g3)
    c: Horizontal(g7)
FEATURE [Sketcher::SketchObject] Sketch034
  FullyConstrained = true
  Placement = pos=(117,19,0) rot=(0.57735,0.57735,0.57735;2.0944rad)
  sketch-geometry (8):
    g0: LineSegment StartX=-49.19 StartY=63.5 StartZ=0 EndX=-49.19 EndY=60.5 EndZ=0
    g1: LineSegment StartX=-49.19 StartY=11.5 StartZ=0 EndX=-49.19 EndY=8.5 EndZ=0
    g2: ArcOfCircle CenterX=-1.5 CenterY=62 CenterZ=0 NormalX=0 NormalY=0 NormalZ=1 AngleXU=0 Radius=1.5 StartAngle=4.71239 EndAngle=7.85398
    g3: ArcOfCircle CenterX=-1.5 CenterY=10 CenterZ=0 NormalX=0 NormalY=0 NormalZ=1 AngleXU=0 Radius=1.5 StartAngle=4.71239 EndAngle=7.85398
    g4: LineSegment StartX=-49.19 StartY=63.5 StartZ=0 EndX=-1.5 EndY=63.5 EndZ=0
    g5: LineSegment StartX=-49.19 StartY=60.5 StartZ=0 EndX=-1.5 EndY=60.5 EndZ=0
    g6: LineSegment StartX=-49.19 StartY=11.5 StartZ=0 EndX=-1.5 EndY=11.5 EndZ=0
    g7: LineSegment StartX=-49.19 StartY=8.5 StartZ=0 EndX=-1.5 EndY=8.5 EndZ=0
  constraints (19):
    c: Vertical(g0)
    c: Distance(g0) = 3
    c: Vertical(g1)
    c: Block(g1)
    c: Block(g2)
    c: Block(g3)
    c: Block(g0)
    c: Coincident(g4,g0)
    c: Coincident(g4,g2)
    c: Horizontal(g4)
    c: Coincident(g5,g0)
    c: Coincident(g5,g2)
    c: Horizontal(g5)
    c: Coincident(g6,g1)
    c: Coincident(g6,g3)
    c: Horizontal(g6)
    c: Coincident(g7,g1)
    c: Coincident(g7,g3)
    c: Horizontal(g7)
FEATURE [Part::Extrusion] Extrude024
  Base = -> Sketch033
  Dir = (1,0,0)
  DirMode = 2
  FaceMakerClass = Part::FaceMakerBullseye
  LengthFwd = 10
  LengthRev = 0
  Solid = true
  Symmetric = false
FEATURE [Part::Extrusion] Extrude025
  Base = -> Sketch034
  Dir = (1,0,0)
  DirMode = 2
  FaceMakerClass = Part::FaceMakerBullseye
  LengthFwd = 10
  LengthRev = 0
  Solid = true
  Symmetric = false
FEATURE [Part::Fillet] Fillet024  label="removeFromtMoreFrontCaseScrewRetainers"
  Base = -> Extrude024
  Edges = 4 edges r=1.49: [Edge6,Edge11,Edge18,Edge23]
  Placement = pos=(-11,0,0) rot=(0,0,1;0rad)
FEATURE [Part::Fillet] Fillet025  label="removeFromtMoreFrontCaseScrewRetainers001"
  Base = -> Extrude025
  Edges = 4 edges r=1.49: [Edge6,Edge11,Edge18,Edge23]
  Placement = pos=(-19,0,0) rot=(0,0,1;0rad)
FEATURE [Part::Cut] Cut022
  Base = -> Cut015
  Tool = -> Fillet025
FEATURE [Part::Cut] Cut023  label="screwRetainers"
  Base = -> Cut022
  Tool = -> Fillet024
FEATURE [Part::MultiFuse] Fusion056  label="bottom005"
  Shapes = -> [Fusion044,Cut021]
FEATURE [Part::MultiFuse] Fusion057  label="casePillars001"
  Shapes = -> [Cut016,Fusion052]
FEATURE [Part::MultiFuse] Fusion058  label="bottom006"
  Shapes = -> [Fusion056,Cut023]
FEATURE [Part::MultiFuse] Fusion059  label="bottom007"
  Shapes = -> [Fusion058,Fillet005]
FEATURE [Part::MultiFuse] Fusion060  label="bottom008"
  Shapes = -> [Fusion059,Fusion]
FEATURE [Part::MultiFuse] Fusion061  label="top011"
  Shapes = -> [Cut006,Cut020]
FEATURE [Part::MultiFuse] Fusion062  label="top012"
  Shapes = -> [Fusion057,Fusion061]
FEATURE [Sketcher::SketchObject] Sketch035  label="topSketch007"
  FullyConstrained = true
  sketch-geometry (6):
    g0: LineSegment StartX=19 StartY=38 StartZ=0 EndX=117 EndY=38 EndZ=0
    g1: ArcOfCircle CenterX=19 CenterY=19 CenterZ=0 NormalX=0 NormalY=0 NormalZ=1 AngleXU=0 Radius=19 StartAngle=1.5708 EndAngle=3.14159
    g2: LineSegment StartX=117 StartY=38 StartZ=0 EndX=117 EndY=19 EndZ=0
    g3: LineSegment StartX=98 StartY=1.0161e-12 StartZ=0 EndX=5.22862e-06 EndY=1.0161e-12 EndZ=0
    g4: LineSegment StartX=5.22862e-06 StartY=19 StartZ=0 EndX=5.22862e-06 EndY=1.0161e-12 EndZ=0
    g5: ArcOfCircle CenterX=98 CenterY=19 CenterZ=0 NormalX=0 NormalY=0 NormalZ=1 AngleXU=0 Radius=19 StartAngle=4.71239 EndAngle=6.28319
  constraints (16):
    c: Horizontal(g0)
    c: Distance(g0) = 98
    c: Coincident(g1,g0)
    c: Block(g1)
    c: Coincident(g2,g0)
    c: Vertical(g2)
    c: Distance(g2) = 19
    c: Horizontal(g3)
    c: Coincident(g4,g1)
    c: Vertical(g4)
    c: Coincident(g3,g4)
    c: Block(g3)
    c: Coincident(g5,g2)
    c: Coincident(g5,g3)
    c: Block(g0)
    c: Block(g5)
FEATURE [Part::Extrusion] Extrude026  label="sideA001"
  Base = -> Sketch035
  Dir = (0,0,1)
  DirMode = 2
  FaceMakerClass = Part::FaceMakerBullseye
  LengthFwd = 3
  LengthRev = 0
  Placement = pos=(0,0,-2.7) rot=(0,0,1;0rad)
  Solid = true
  Symmetric = false
FEATURE [Sketcher::SketchObject] Sketch036  label="topSketch008"
  FullyConstrained = true
  sketch-geometry (6):
    g0: LineSegment StartX=19 StartY=38 StartZ=0 EndX=117 EndY=38 EndZ=0
    g1: ArcOfCircle CenterX=19 CenterY=19 CenterZ=0 NormalX=0 NormalY=0 NormalZ=1 AngleXU=0 Radius=19 StartAngle=1.5708 EndAngle=3.14159
    g2: LineSegment StartX=117 StartY=38 StartZ=0 EndX=117 EndY=19 EndZ=0
    g3: LineSegment StartX=98 StartY=1.0161e-12 StartZ=0 EndX=5.22862e-06 EndY=1.0161e-12 EndZ=0
    g4: LineSegment StartX=5.22862e-06 StartY=19 StartZ=0 EndX=5.22862e-06 EndY=1.0161e-12 EndZ=0
    g5: ArcOfCircle CenterX=98 CenterY=19 CenterZ=0 NormalX=0 NormalY=0 NormalZ=1 AngleXU=0 Radius=19 StartAngle=4.71239 EndAngle=6.28319
  constraints (16):
    c: Horizontal(g0)
    c: Distance(g0) = 98
    c: Coincident(g1,g0)
    c: Block(g1)
    c: Coincident(g2,g0)
    c: Vertical(g2)
    c: Distance(g2) = 19
    c: Horizontal(g3)
    c: Coincident(g4,g1)
    c: Vertical(g4)
    c: Coincident(g3,g4)
    c: Block(g3)
    c: Coincident(g5,g2)
    c: Coincident(g5,g3)
    c: Block(g0)
    c: Block(g5)
FEATURE [Part::Extrusion] Extrude027  label="sideB001"
  Base = -> Sketch036
  Dir = (0,0,1)
  DirMode = 2
  FaceMakerClass = Part::FaceMakerBullseye
  LengthFwd = 3
  LengthRev = 0
  Placement = pos=(0,0,71.7) rot=(0,0,1;0rad)
  Solid = true
  Symmetric = false
FEATURE [Part::MultiFuse] Fusion064  label="removeFromBottom"
  Shapes = -> [Extrude026,Extrude027]
FEATURE [Part::Cut] Cut024  label="bottom009"
  Base = -> Fusion060
  Tool = -> Fusion064
FEATURE [Sketcher::SketchObject] Sketch037  label="topSketch009"
  FullyConstrained = true
  sketch-geometry (6):
    g0: ArcOfCircle CenterX=19 CenterY=19 CenterZ=0 NormalX=0 NormalY=0 NormalZ=1 AngleXU=0 Radius=19 StartAngle=1.5708 EndAngle=3.14159
    g1: LineSegment StartX=5.22862e-06 StartY=19 StartZ=0 EndX=5.22862e-06 EndY=1.19904e-11 EndZ=0
    g2: LineSegment StartX=19 StartY=38 StartZ=0 EndX=124 EndY=38 EndZ=0
    g3: LineSegment StartX=5.22862e-06 StartY=1.19904e-11 StartZ=0 EndX=105 EndY=1.19904e-11 EndZ=0
    g4: ArcOfCircle CenterX=105 CenterY=19 CenterZ=0 NormalX=0 NormalY=0 NormalZ=1 AngleXU=0 Radius=19 StartAngle=4.71239 EndAngle=6.28319
    g5: LineSegment StartX=124 StartY=38 StartZ=0 EndX=124 EndY=19 EndZ=0
  constraints (16):
    c: Block(g0)
    c: Coincident(g1,g0)
    c: Vertical(g1)
    c: Horizontal(g2)
    c: Distance(g2) = 105
    c: Coincident(g2,g0)
    c: Distance(g1) = 19
    c: Coincident(g3,g1)
    c: Horizontal(g3)
    c: Distance(g3) = 105
    c: Block(g4)
    c: Coincident(g4,g3)
    c: Coincident(g5,g2)
    c: Coincident(g5,g4)
    c: Vertical(g5)
    c: Distance(g5) = 19
FEATURE [Part::Extrusion] Extrude028  label="sideB"
  Base = -> Sketch037
  Dir = (0,0,1)
  DirMode = 2
  FaceMakerClass = Part::FaceMakerBullseye
  LengthFwd = 3
  LengthRev = 0
  Placement = pos=(0,0,72) rot=(0,0,1;0rad)
  Solid = true
  Symmetric = false
FEATURE [Sketcher::SketchObject] Sketch038  label="topSketch010"
  FullyConstrained = true
  sketch-geometry (22):
    g0: LineSegment StartX=5.21097e-06 StartY=3 StartZ=0 EndX=5.21097e-06 EndY=19 EndZ=0
    g1: ArcOfCircle CenterX=19 CenterY=19 CenterZ=0 NormalX=0 NormalY=0 NormalZ=1 AngleXU=0 Radius=19 StartAngle=1.5708 EndAngle=3.14159
    g2: ArcOfCircle CenterX=19 CenterY=19 CenterZ=0 NormalX=0 NormalY=0 NormalZ=1 AngleXU=0 Radius=16 StartAngle=1.5708 EndAngle=3.14159
    g3: LineSegment StartX=114 StartY=35 StartZ=0 EndX=19 EndY=35 EndZ=0
    g4: LineSegment StartX=5.21097e-06 StartY=3 StartZ=0 EndX=5.21097e-06 EndY=0 EndZ=0
    g5: LineSegment StartX=3 StartY=0 StartZ=0 EndX=5.21097e-06 EndY=0 EndZ=0
    g6: LineSegment StartX=3 StartY=19 StartZ=0 EndX=3 EndY=0 EndZ=0
    g7: LineSegment StartX=19 StartY=38 StartZ=0 EndX=124 EndY=38 EndZ=0
    g8: Circle CenterX=119 CenterY=35 CenterZ=0 NormalX=0 NormalY=0 NormalZ=1 AngleXU=0 Radius=1
    g9: Circle CenterX=121 CenterY=35 CenterZ=0 NormalX=0 NormalY=0 NormalZ=1 AngleXU=0 Radius=1
    g10: Circle CenterX=121 CenterY=33 CenterZ=0 NormalX=0 NormalY=0 NormalZ=1 AngleXU=0 Radius=1
    g11: BSplineCurve PolesCount=3 KnotsCount=2 Degree=2 IsPeriodic=0
    g12: GeomPoint X=119 Y=35 Z=0
    g13: GeomPoint X=121 Y=33 Z=0
    g14: LineSegment StartX=119 StartY=35 StartZ=0 EndX=114 EndY=35 EndZ=0
    g15: ArcOfCircle CenterX=105 CenterY=19 CenterZ=0 NormalX=0 NormalY=0 NormalZ=1 AngleXU=0 Radius=16 StartAngle=5.60905 EndAngle=6.28319
    g16: LineSegment StartX=121 StartY=33 StartZ=0 EndX=121 EndY=19 EndZ=0
    g17: LineSegment StartX=117.5 StartY=9.01251 StartZ=0 EndX=121.163 EndY=9.0125 EndZ=0
    g18: ArcOfCircle CenterX=105 CenterY=19 CenterZ=0 NormalX=0 NormalY=0 NormalZ=1 AngleXU=0 Radius=20.6155 StartAngle=5.7297 EndAngle=6.28319
    g19: LineSegment StartX=121.163 StartY=9.0125 StartZ=0 EndX=122.538 EndY=8.16329 EndZ=0
    g20: LineSegment StartX=124 StartY=38 StartZ=0 EndX=125.616 EndY=38 EndZ=0
    g21: LineSegment StartX=125.616 StartY=19 StartZ=0 EndX=125.616 EndY=38 EndZ=0
  constraints (49):
    c: Vertical(g0)
    c: Block(g0)
    c: Coincident(g1,g0)
    c: Block(g1)
    c: Coincident(g2,g1)
    c: Block(g2)
    c: Coincident(g3,g2)
    c: Horizontal(g3)
    c: Tangent(g3,g2)
    c: Coincident(g4,g0)
    c: Distance(g4) = 3
    c: Vertical(g4)
    c: Coincident(g5,g4)
    c: Horizontal(g5)
    c: Coincident(g6,g2)
    c: Coincident(g6,g5)
    c: Vertical(g6)
    c: Horizontal(g7)
    c: Distance(g7) = 105
    c: Coincident(g7,g1)
    c: Block(g3)
    c: Weight(g8) = 1
    c: Equal(g8,g9)
    c: Equal(g8,g10)
    c: InternalAlignment(g8,g11)
    c: InternalAlignment(g9,g11)
    c: InternalAlignment(g10,g11)
    c: InternalAlignment(g12,g11)
    c: InternalAlignment(g13,g11)
    c: Block(g11)
    c: Coincident(g14,g11)
    c: Coincident(g14,g3)
    c: Horizontal(g14)
    c: Block(g15)
    c: Coincident(g16,g11)
    c: Coincident(g16,g15)
    c: Vertical(g16)
    c: Distance(g16) = 14
    c: Coincident(g17,g15)
    c: Block(g18)
    c: Coincident(g19,g18)
    c: Coincident(g20,g7)
    c: Horizontal(g20)
    c: Vertical(g21)
    c: Coincident(g20,g21)
    c: Block(g20)
    c: Block(g21)
    c: Block(g19)
    c: Block(g17)
FEATURE [Part::Extrusion] Extrude029
  Base = -> Sketch038
  Dir = (0,0,1)
  DirMode = 2
  FaceMakerClass = Part::FaceMakerBullseye
  LengthFwd = 72
  LengthRev = 0
  Solid = true
  Symmetric = false
FEATURE [Part::Feature] Face085
  shape: bbox 4.8 x 25.5 x 2e-07 mm, 1 faces, 0 solids (baked)
FEATURE [Part::Revolution] Revolve089  label="moreFrontCaseScrewPost003"
  Angle = 360
  Axis = (0,1,0)
  Base = (0,0,0)
  FaceMakerClass = Part::FaceMakerBullseye
  Placement = pos=(109.5,4.5,3.5) rot=(0,0,1;0rad)
  Solid = false
  Source = -> Face085
  Symmetric = false
FEATURE [Part::Feature] Face086
  shape: bbox 4.8 x 25.5 x 2e-07 mm, 1 faces, 0 solids (baked)
FEATURE [Part::Revolution] Revolve090  label="moreFrontCaseScrewPost004"
  Angle = 360
  Axis = (0,1,0)
  Base = (0,0,0)
  FaceMakerClass = Part::FaceMakerBullseye
  Placement = pos=(109.5,4.5,68.5) rot=(0,0,1;0rad)
  Solid = false
  Source = -> Face086
  Symmetric = false
FEATURE [Part::Fillet] Fillet026  label="top013"
  Base = -> Extrude029
  Edges = 1 edges r=2: [Edge35]
FEATURE [Sketcher::SketchObject] Sketch039
  FullyConstrained = true
  sketch-geometry (7):
    g0: LineSegment StartX=0 StartY=0 StartZ=0 EndX=0 EndY=6 EndZ=0
    g1: Circle CenterX=0 CenterY=0 CenterZ=0 NormalX=0 NormalY=0 NormalZ=1 AngleXU=0 Radius=1
    g2: Circle CenterX=8 CenterY=6 CenterZ=0 NormalX=0 NormalY=0 NormalZ=1 AngleXU=0 Radius=1
    g3: BSplineCurve PolesCount=3 KnotsCount=2 Degree=2 IsPeriodic=0
    g4: GeomPoint X=0 Y=0 Z=0
    g5: GeomPoint X=8 Y=6 Z=0
    g6: LineSegment StartX=0 StartY=6 StartZ=0 EndX=8 EndY=6 EndZ=0
  constraints (14):
    c: Coincident(g0,g-1)
    c: Distance(g0) = 6
    c: Vertical(g0)
    c: Coincident(g3,g0)
    c: Weight(g1) = 1
    c: Equal(g1,g2)
    c: InternalAlignment(g1,g3)
    c: InternalAlignment(g2,g3)
    c: InternalAlignment(g4,g3)
    c: InternalAlignment(g5,g3)
    c: Block(g3)
    c: Coincident(g6,g0)
    c: Coincident(g6,g3)
    c: Horizontal(g6)
FEATURE [Sketcher::SketchObject] Sketch040
  FullyConstrained = true
  sketch-geometry (7):
    g0: LineSegment StartX=0 StartY=0 StartZ=0 EndX=0 EndY=6 EndZ=0
    g1: Circle CenterX=0 CenterY=0 CenterZ=0 NormalX=0 NormalY=0 NormalZ=1 AngleXU=0 Radius=1
    g2: Circle CenterX=8 CenterY=6 CenterZ=0 NormalX=0 NormalY=0 NormalZ=1 AngleXU=0 Radius=1
    g3: BSplineCurve PolesCount=3 KnotsCount=2 Degree=2 IsPeriodic=0
    g4: GeomPoint X=0 Y=0 Z=0
    g5: GeomPoint X=8 Y=6 Z=0
    g6: LineSegment StartX=0 StartY=6 StartZ=0 EndX=8 EndY=6 EndZ=0
  constraints (14):
    c: Coincident(g0,g-1)
    c: Distance(g0) = 6
    c: Vertical(g0)
    c: Coincident(g3,g0)
    c: Weight(g1) = 1
    c: Equal(g1,g2)
    c: InternalAlignment(g1,g3)
    c: InternalAlignment(g2,g3)
    c: InternalAlignment(g4,g3)
    c: InternalAlignment(g5,g3)
    c: Block(g3)
    c: Coincident(g6,g0)
    c: Coincident(g6,g3)
    c: Horizontal(g6)
FEATURE [Sketcher::SketchObject] Sketch041
  FullyConstrained = true
  sketch-geometry (7):
    g0: LineSegment StartX=0 StartY=0 StartZ=0 EndX=0 EndY=6 EndZ=0
    g1: Circle CenterX=0 CenterY=0 CenterZ=0 NormalX=0 NormalY=0 NormalZ=1 AngleXU=0 Radius=1
    g2: Circle CenterX=8 CenterY=6 CenterZ=0 NormalX=0 NormalY=0 NormalZ=1 AngleXU=0 Radius=1
    g3: BSplineCurve PolesCount=3 KnotsCount=2 Degree=2 IsPeriodic=0
    g4: GeomPoint X=0 Y=0 Z=0
    g5: GeomPoint X=8 Y=6 Z=0
    g6: LineSegment StartX=0 StartY=6 StartZ=0 EndX=8 EndY=6 EndZ=0
  constraints (14):
    c: Coincident(g0,g-1)
    c: Distance(g0) = 6
    c: Vertical(g0)
    c: Coincident(g3,g0)
    c: Weight(g1) = 1
    c: Equal(g1,g2)
    c: InternalAlignment(g1,g3)
    c: InternalAlignment(g2,g3)
    c: InternalAlignment(g4,g3)
    c: InternalAlignment(g5,g3)
    c: Block(g3)
    c: Coincident(g6,g0)
    c: Coincident(g6,g3)
    c: Horizontal(g6)
FEATURE [Sketcher::SketchObject] Sketch042
  FullyConstrained = true
  sketch-geometry (7):
    g0: LineSegment StartX=0 StartY=0 StartZ=0 EndX=0 EndY=6 EndZ=0
    g1: Circle CenterX=0 CenterY=0 CenterZ=0 NormalX=0 NormalY=0 NormalZ=1 AngleXU=0 Radius=1
    g2: Circle CenterX=8 CenterY=6 CenterZ=0 NormalX=0 NormalY=0 NormalZ=1 AngleXU=0 Radius=1
    g3: BSplineCurve PolesCount=3 KnotsCount=2 Degree=2 IsPeriodic=0
    g4: GeomPoint X=0 Y=0 Z=0
    g5: GeomPoint X=8 Y=6 Z=0
    g6: LineSegment StartX=0 StartY=6 StartZ=0 EndX=8 EndY=6 EndZ=0
  constraints (14):
    c: Coincident(g0,g-1)
    c: Distance(g0) = 6
    c: Vertical(g0)
    c: Coincident(g3,g0)
    c: Weight(g1) = 1
    c: Equal(g1,g2)
    c: InternalAlignment(g1,g3)
    c: InternalAlignment(g2,g3)
    c: InternalAlignment(g4,g3)
    c: InternalAlignment(g5,g3)
    c: Block(g3)
    c: Coincident(g6,g0)
    c: Coincident(g6,g3)
    c: Horizontal(g6)
FEATURE [Part::Extrusion] Extrude030  label="caseScrewPillarBracket008"
  Base = -> Sketch039
  Dir = (0,0,1)
  DirMode = 2
  FaceMakerClass = Part::FaceMakerBullseye
  LengthFwd = 2.4
  LengthRev = 0
  Placement = pos=(15.76,29,8.8) rot=(0,1,0;0rad)
  Solid = true
  Symmetric = false
FEATURE [Part::Extrusion] Extrude031  label="caseScrewPillarBracket009"
  Base = -> Sketch040
  Dir = (0,0,1)
  DirMode = 2
  FaceMakerClass = Part::FaceMakerBullseye
  LengthFwd = 2.4
  LengthRev = 0
  Placement = pos=(15.76,29,60.8) rot=(0,0,1;0rad)
  Solid = true
  Symmetric = false
FEATURE [Part::Extrusion] Extrude032  label="caseScrewPillarBracket010"
  Base = -> Sketch041
  Dir = (0,0,1)
  DirMode = 2
  FaceMakerClass = Part::FaceMakerBullseye
  LengthFwd = 2.4
  LengthRev = 0
  Placement = pos=(13.7,29,13.26) rot=(0,-1,0;1.5708rad)
  Solid = true
  Symmetric = false
FEATURE [Part::Extrusion] Extrude033  label="caseScrewPillarBracket011"
  Base = -> Sketch042
  Dir = (0,0,1)
  DirMode = 2
  FaceMakerClass = Part::FaceMakerBullseye
  LengthFwd = 2.4
  LengthRev = 0
  Placement = pos=(11.3,29,58.74) rot=(0,1,0;1.5708rad)
  Solid = true
  Symmetric = false
FEATURE [Sketcher::SketchObject] Sketch043
  FullyConstrained = true
  sketch-geometry (7):
    g0: LineSegment StartX=0 StartY=0 StartZ=0 EndX=0 EndY=6 EndZ=0
    g1: Circle CenterX=0 CenterY=0 CenterZ=0 NormalX=0 NormalY=0 NormalZ=1 AngleXU=0 Radius=1
    g2: Circle CenterX=8 CenterY=6 CenterZ=0 NormalX=0 NormalY=0 NormalZ=1 AngleXU=0 Radius=1
    g3: BSplineCurve PolesCount=3 KnotsCount=2 Degree=2 IsPeriodic=0
    g4: GeomPoint X=0 Y=0 Z=0
    g5: GeomPoint X=8 Y=6 Z=0
    g6: LineSegment StartX=0 StartY=6 StartZ=0 EndX=8 EndY=6 EndZ=0
  constraints (14):
    c: Coincident(g0,g-1)
    c: Distance(g0) = 6
    c: Vertical(g0)
    c: Coincident(g3,g0)
    c: Weight(g1) = 1
    c: Equal(g1,g2)
    c: InternalAlignment(g1,g3)
    c: InternalAlignment(g2,g3)
    c: InternalAlignment(g4,g3)
    c: InternalAlignment(g5,g3)
    c: Block(g3)
    c: Coincident(g6,g0)
    c: Coincident(g6,g3)
    c: Horizontal(g6)
FEATURE [Part::Extrusion] Extrude034  label="caseScrewPillarBracket012"
  Base = -> Sketch043
  Dir = (0,0,1)
  DirMode = 2
  FaceMakerClass = Part::FaceMakerBullseye
  LengthFwd = 2.4
  LengthRev = 0
  Placement = pos=(88.3,29,65.23) rot=(0,1,0;1.5708rad)
  Solid = true
  Symmetric = false
FEATURE [Sketcher::SketchObject] Sketch044
  FullyConstrained = true
  sketch-geometry (7):
    g0: LineSegment StartX=0 StartY=0 StartZ=0 EndX=0 EndY=6 EndZ=0
    g1: Circle CenterX=0 CenterY=0 CenterZ=0 NormalX=0 NormalY=0 NormalZ=1 AngleXU=0 Radius=1
    g2: Circle CenterX=8 CenterY=6 CenterZ=0 NormalX=0 NormalY=0 NormalZ=1 AngleXU=0 Radius=1
    g3: BSplineCurve PolesCount=3 KnotsCount=2 Degree=2 IsPeriodic=0
    g4: GeomPoint X=0 Y=0 Z=0
    g5: GeomPoint X=8 Y=6 Z=0
    g6: LineSegment StartX=0 StartY=6 StartZ=0 EndX=8 EndY=6 EndZ=0
  constraints (14):
    c: Coincident(g0,g-1)
    c: Distance(g0) = 6
    c: Vertical(g0)
    c: Coincident(g3,g0)
    c: Weight(g1) = 1
    c: Equal(g1,g2)
    c: InternalAlignment(g1,g3)
    c: InternalAlignment(g2,g3)
    c: InternalAlignment(g4,g3)
    c: InternalAlignment(g5,g3)
    c: Block(g3)
    c: Coincident(g6,g0)
    c: Coincident(g6,g3)
    c: Horizontal(g6)
FEATURE [Part::Extrusion] Extrude035  label="caseScrewPillarBracket013"
  Base = -> Sketch044
  Dir = (0,0,1)
  DirMode = 2
  FaceMakerClass = Part::FaceMakerBullseye
  LengthFwd = 2.4
  LengthRev = 0
  Placement = pos=(90.7,29,6.77) rot=(0,-1,0;1.5708rad)
  Solid = true
  Symmetric = false
FEATURE [Sketcher::SketchObject] Sketch045
  FullyConstrained = true
  sketch-geometry (7):
    g0: LineSegment StartX=0 StartY=0 StartZ=0 EndX=0 EndY=6 EndZ=0
    g1: Circle CenterX=0 CenterY=0 CenterZ=0 NormalX=0 NormalY=0 NormalZ=1 AngleXU=0 Radius=1
    g2: Circle CenterX=8 CenterY=6 CenterZ=0 NormalX=0 NormalY=0 NormalZ=1 AngleXU=0 Radius=1
    g3: BSplineCurve PolesCount=3 KnotsCount=2 Degree=2 IsPeriodic=0
    g4: GeomPoint X=0 Y=0 Z=0
    g5: GeomPoint X=8 Y=6 Z=0
    g6: LineSegment StartX=0 StartY=6 StartZ=0 EndX=8 EndY=6 EndZ=0
  constraints (14):
    c: Coincident(g0,g-1)
    c: Distance(g0) = 6
    c: Vertical(g0)
    c: Coincident(g3,g0)
    c: Weight(g1) = 1
    c: Equal(g1,g2)
    c: InternalAlignment(g1,g3)
    c: InternalAlignment(g2,g3)
    c: InternalAlignment(g4,g3)
    c: InternalAlignment(g5,g3)
    c: Block(g3)
    c: Coincident(g6,g0)
    c: Coincident(g6,g3)
    c: Horizontal(g6)
FEATURE [Sketcher::SketchObject] Sketch046
  FullyConstrained = true
  sketch-geometry (7):
    g0: LineSegment StartX=0 StartY=0 StartZ=0 EndX=0 EndY=6 EndZ=0
    g1: Circle CenterX=0 CenterY=0 CenterZ=0 NormalX=0 NormalY=0 NormalZ=1 AngleXU=0 Radius=1
    g2: Circle CenterX=8 CenterY=6 CenterZ=0 NormalX=0 NormalY=0 NormalZ=1 AngleXU=0 Radius=1
    g3: BSplineCurve PolesCount=3 KnotsCount=2 Degree=2 IsPeriodic=0
    g4: GeomPoint X=0 Y=0 Z=0
    g5: GeomPoint X=8 Y=6 Z=0
    g6: LineSegment StartX=0 StartY=6 StartZ=0 EndX=8 EndY=6 EndZ=0
  constraints (14):
    c: Coincident(g0,g-1)
    c: Distance(g0) = 6
    c: Vertical(g0)
    c: Coincident(g3,g0)
    c: Weight(g1) = 1
    c: Equal(g1,g2)
    c: InternalAlignment(g1,g3)
    c: InternalAlignment(g2,g3)
    c: InternalAlignment(g4,g3)
    c: InternalAlignment(g5,g3)
    c: Block(g3)
    c: Coincident(g6,g0)
    c: Coincident(g6,g3)
    c: Horizontal(g6)
FEATURE [Part::Extrusion] Extrude036  label="caseScrewPillarBracket014"
  Base = -> Sketch045
  Dir = (0,0,1)
  DirMode = 2
  FaceMakerClass = Part::FaceMakerBullseye
  LengthFwd = 2.4
  LengthRev = 0
  Placement = pos=(110.7,29,6.77) rot=(0,-1,0;1.5708rad)
  Solid = true
  Symmetric = false
FEATURE [Part::Extrusion] Extrude037  label="caseScrewPillarBracket015"
  Base = -> Sketch046
  Dir = (0,0,1)
  DirMode = 2
  FaceMakerClass = Part::FaceMakerBullseye
  LengthFwd = 2.4
  LengthRev = 0
  Placement = pos=(108.3,29,65.23) rot=(0,1,0;1.5708rad)
  Solid = true
  Symmetric = false
FEATURE [Part::Box] Box013  label="frontCaseScrewPillarBracket002"
  AttacherType = Attacher::AttachEngine3D
  Height = 2.4
  Length = 22
  Placement = pos=(87,28,2.3) rot=(0,0,1;0rad)
  Width = 7
FEATURE [Part::Box] Box014  label="frontCaseScrewPillarBracket003"
  AttacherType = Attacher::AttachEngine3D
  Height = 2.4
  Length = 22
  Placement = pos=(87,28,67.3) rot=(0,0,1;0rad)
  Width = 7
FEATURE [Part::Feature] Face087
  shape: bbox 4.8 x 30.2 x 2e-07 mm, 1 faces, 0 solids (baked)
FEATURE [Part::Revolution] Revolve091  label="frontCaseScrewPost004"
  Angle = 360
  Axis = (0,1,0)
  Base = (0,0,0)
  FaceMakerClass = Part::FaceMakerBullseye
  Placement = pos=(89.5,4.5,3.5) rot=(0,0,1;0rad)
  Solid = false
  Source = -> Face087
  Symmetric = false
FEATURE [Part::Feature] Face088
  shape: bbox 4.8 x 30.2 x 2e-07 mm, 1 faces, 0 solids (baked)
FEATURE [Part::Revolution] Revolve092  label="frontCaseScrewPost005"
  Angle = 360
  Axis = (0,1,0)
  Base = (0,0,0)
  FaceMakerClass = Part::FaceMakerBullseye
  Placement = pos=(89.5,4.5,68.5) rot=(0,0,1;0rad)
  Solid = false
  Source = -> Face088
  Symmetric = false
FEATURE [Part::Feature] Face089
  shape: bbox 3.5 x 30.2 x 2e-07 mm, 1 faces, 0 solids (baked)
FEATURE [Part::Revolution] Revolve093  label="backCaseScrewPost002"
  Angle = 360
  Axis = (0,1,0)
  Base = (0,0,0)
  FaceMakerClass = Part::FaceMakerBullseye
  Placement = pos=(12.5,4.5,10) rot=(0,0,1;0rad)
  Solid = false
  Source = -> Face089
  Symmetric = false
FEATURE [Part::Feature] Face090
  shape: bbox 3.5 x 30.2 x 2e-07 mm, 1 faces, 0 solids (baked)
FEATURE [Part::Revolution] Revolve094  label="backCaseScrewPost003"
  Angle = 360
  Axis = (0,1,0)
  Base = (0,0,0)
  FaceMakerClass = Part::FaceMakerBullseye
  Placement = pos=(12.5,4.5,62) rot=(0,0,1;0rad)
  Solid = false
  Source = -> Face090
  Symmetric = false
FEATURE [Part::Box] Box015  label="Cube011"
  AttacherType = Attacher::AttachEngine3D
  Height = 28.8
  Length = 3
  Placement = pos=(107.3,28,21.6) rot=(0,0,1;0rad)
  Width = 7
FEATURE [Part::Box] Box016  label="Cube012"
  AttacherType = Attacher::AttachEngine3D
  Height = 3
  Length = 7.4
  Placement = pos=(107.3,28,18.6) rot=(0,0,1;0rad)
  Width = 7
FEATURE [Part::Box] Box017  label="Cube013"
  AttacherType = Attacher::AttachEngine3D
  Height = 3
  Length = 7.4
  Placement = pos=(107.3,28,50.4) rot=(0,0,1;0rad)
  Width = 7
FEATURE [Part::Cylinder] Cylinder024
  Angle = 360
  AttacherType = Attacher::AttachEngine3D
  Height = 20
  Placement = pos=(0,0,36.15) rot=(0,0,1;0rad)
  Radius = 14.3
FEATURE [Part::Cylinder] Cylinder025
  Angle = 360
  AttacherType = Attacher::AttachEngine3D
  Height = 10
  Placement = pos=(0,0,36.15) rot=(0,0,1;0rad)
  Radius = 4
FEATURE [Part::MultiFuse] Fusion066  label="removeToCreteHoleForPlugHousing009"
  Placement = pos=(70,19,36) rot=(0,1,0;1.5708rad)
  Shapes = -> [Cylinder024,Cylinder025]
FEATURE [Part::MultiFuse] Fusion065  label="plugHousingBracketHolder002"
  Shapes = -> [Box017,Box015,Box016]
FEATURE [Part::Cut] Cut025  label="plugHousingBracketHolder003"
  Base = -> Fusion065
  Placement = pos=(7,0,0) rot=(0,0,1;0rad)
  Tool = -> Fusion066
FEATURE [Sketcher::SketchObject] Sketch047
  FullyConstrained = false
  Placement = pos=(0,0,0) rot=(1,0,0;1.5708rad)
  sketch-geometry (24):
    g0: ArcOfCircle CenterX=-4 CenterY=-10.5 CenterZ=0 NormalX=0 NormalY=0 NormalZ=1 AngleXU=0 Radius=1.5 StartAngle=6e-16 EndAngle=3.14159
    g1: ArcOfCircle CenterX=-34.2 CenterY=-10.5 CenterZ=0 NormalX=0 NormalY=0 NormalZ=1 AngleXU=0 Radius=1.5 StartAngle=0 EndAngle=3.14159
    g2: ArcOfCircle CenterX=-34.2 CenterY=-27.7 CenterZ=0 NormalX=0 NormalY=0 NormalZ=1 AngleXU=0 Radius=1.5 StartAngle=3.14159 EndAngle=6.28319
    g3: ArcOfCircle CenterX=-4 CenterY=-27.7 CenterZ=0 NormalX=0 NormalY=0 NormalZ=1 AngleXU=0 Radius=1.5 StartAngle=3.1416 EndAngle=6.28319
    g4: ArcOfCircle CenterX=-10 CenterY=-4.3 CenterZ=0 NormalX=0 NormalY=0 NormalZ=1 AngleXU=0 Radius=1.5 StartAngle=2e-16 EndAngle=3.14159
    g5: ArcOfCircle CenterX=-16.1 CenterY=-1.8 CenterZ=0 NormalX=0 NormalY=0 NormalZ=1 AngleXU=0 Radius=1.5 StartAngle=5e-16 EndAngle=3.14159
    g6: ArcOfCircle CenterX=-22.1 CenterY=-1.8 CenterZ=0 NormalX=0 NormalY=0 NormalZ=1 AngleXU=0 Radius=1.5 StartAngle=5e-16 EndAngle=3.14159
    g7: ArcOfCircle CenterX=-28.2 CenterY=-4.3 CenterZ=0 NormalX=0 NormalY=0 NormalZ=1 AngleXU=0 Radius=1.5 StartAngle=2e-16 EndAngle=3.14159
    g8: ArcOfCircle CenterX=-10 CenterY=-33.9 CenterZ=0 NormalX=0 NormalY=0 NormalZ=1 AngleXU=0 Radius=1.5 StartAngle=3.14159 EndAngle=6.28319
    g9: ArcOfCircle CenterX=-16.1 CenterY=-36.4 CenterZ=0 NormalX=0 NormalY=0 NormalZ=1 AngleXU=0 Radius=1.5 StartAngle=3.14159 EndAngle=6.28319
    g10: ArcOfCircle CenterX=-22.1 CenterY=-36.4 CenterZ=0 NormalX=0 NormalY=0 NormalZ=1 AngleXU=0 Radius=1.5 StartAngle=3.14159 EndAngle=6.28319
    g11: ArcOfCircle CenterX=-28.2 CenterY=-33.9 CenterZ=0 NormalX=0 NormalY=0 NormalZ=1 AngleXU=0 Radius=1.5 StartAngle=3.14159 EndAngle=6.28319
    g12: LineSegment StartX=-35.7 StartY=-10.5 StartZ=0 EndX=-35.7 EndY=-27.7 EndZ=0
    g13: LineSegment StartX=-32.7 StartY=-10.5 StartZ=0 EndX=-32.7 EndY=-27.7 EndZ=0
    g14: LineSegment StartX=-29.7 StartY=-33.9 StartZ=0 EndX=-29.7 EndY=-4.3 EndZ=0
    g15: LineSegment StartX=-26.7 StartY=-33.9 StartZ=0 EndX=-26.7 EndY=-4.3 EndZ=0
    g16: LineSegment StartX=-2.5 StartY=-10.5 StartZ=0 EndX=-2.5 EndY=-27.7 EndZ=0
    g17: LineSegment StartX=-8.5 StartY=-4.3 StartZ=0 EndX=-8.5 EndY=-33.9 EndZ=0
    g18: LineSegment StartX=-5.5 StartY=-10.5 StartZ=0 EndX=-5.5 EndY=-27.7 EndZ=0
    g19: LineSegment StartX=-11.5 StartY=-4.3 StartZ=0 EndX=-11.5 EndY=-33.9 EndZ=0
    g20: LineSegment StartX=-14.6 StartY=-1.8 StartZ=0 EndX=-14.6 EndY=-36.4 EndZ=0
    g21: LineSegment StartX=-17.6 StartY=-1.8 StartZ=0 EndX=-17.6 EndY=-36.4 EndZ=0
    g22: LineSegment StartX=-20.6 StartY=-36.4 StartZ=0 EndX=-20.6 EndY=-1.8 EndZ=0
    g23: LineSegment StartX=-23.6 StartY=-1.8 StartZ=0 EndX=-23.6 EndY=-36.4 EndZ=0
  constraints (48):
    c: Block(g0)
    c: Block(g1)
    c: Block(g2)
    c: Block(g3)
    c: Block(g4)
    c: Block(g5)
    c: Block(g6)
    c: Block(g7)
    c: Block(g8)
    c: Block(g9)
    c: Block(g10)
    c: Block(g11)
    c: Coincident(g12,g1)
    c: Coincident(g12,g2)
    c: Vertical(g12)
    c: Coincident(g13,g1)
    c: Coincident(g13,g2)
    c: Vertical(g13)
    c: Coincident(g14,g11)
    c: Coincident(g14,g7)
    c: Vertical(g14)
    c: Coincident(g15,g11)
    c: Coincident(g15,g7)
    c: Vertical(g15)
    c: Coincident(g16,g0)
    c: Coincident(g16,g3)
    c: Vertical(g16)
    c: Coincident(g17,g4)
    c: Coincident(g17,g8)
    c: Vertical(g17)
    c: Coincident(g18,g0)
    c: Coincident(g18,g3)
    c: Vertical(g18)
    c: Coincident(g19,g4)
    c: Coincident(g19,g8)
    c: Vertical(g19)
    c: Coincident(g20,g5)
    c: Coincident(g20,g9)
    c: Vertical(g20)
    c: Coincident(g21,g5)
    c: Coincident(g21,g9)
    c: Vertical(g21)
    c: Coincident(g22,g10)
    c: Coincident(g22,g6)
    c: Vertical(g22)
    c: Coincident(g23,g6)
    c: Coincident(g23,g10)
    c: Vertical(g23)
FEATURE [Part::Extrusion] Extrude038  label="removeToCreateFanGrillHoles001"
  Base = -> Sketch047
  Dir = (0,-1,6e-16)
  DirMode = 2
  FaceMakerClass = Part::FaceMakerBullseye
  LengthFwd = 10
  LengthRev = 0
  Placement = pos=(65.4,44,54.82) rot=(0,0,1;0rad)
  Solid = true
  Symmetric = false
FEATURE [Part::Feature] Wire004
  shape: bbox 11 x 5.2 x 2e-07 mm, 0 faces, 0 solids (baked)
FEATURE [Part::Revolution] Revolve095
  Angle = 360
  Axis = (0,1,0)
  Base = (0,0,0)
  FaceMakerClass = Part::FaceMakerBullseye
  Placement = pos=(30.3,38,19.7) rot=(0,0,1;0rad)
  Solid = true
  Source = -> Wire004
  Symmetric = false
FEATURE [Part::Feature] Wire005
  shape: bbox 11 x 5.2 x 2e-07 mm, 0 faces, 0 solids (baked)
FEATURE [Part::Revolution] Revolve096
  Angle = 360
  Axis = (0,1,0)
  Base = (0,0,0)
  FaceMakerClass = Part::FaceMakerBullseye
  Placement = pos=(30.3,38,51.7) rot=(0,0,1;0rad)
  Solid = true
  Source = -> Wire005
  Symmetric = false
FEATURE [Part::Feature] Wire006
  shape: bbox 11 x 5.2 x 2e-07 mm, 0 faces, 0 solids (baked)
FEATURE [Part::Revolution] Revolve097
  Angle = 360
  Axis = (0,1,0)
  Base = (0,0,0)
  FaceMakerClass = Part::FaceMakerBullseye
  Placement = pos=(62.3,38,51.7) rot=(0,0,1;0rad)
  Solid = true
  Source = -> Wire006
  Symmetric = false
FEATURE [Part::Feature] Wire007
  shape: bbox 11 x 5.2 x 2e-07 mm, 0 faces, 0 solids (baked)
FEATURE [Part::Revolution] Revolve098
  Angle = 360
  Axis = (0,1,0)
  Base = (0,0,0)
  FaceMakerClass = Part::FaceMakerBullseye
  Placement = pos=(62.3,38,19.7) rot=(0,0,1;0rad)
  Solid = true
  Source = -> Wire007
  Symmetric = false
FEATURE [Part::MultiFuse] Fusion067  label="fanScrewHousing002"
  Shapes = -> [Revolve098,Revolve097,Revolve096,Revolve095]
FEATURE [Part::Feature] Face091 .. Face094  x4 (patterned run collapsed; names and placements below)
  shape: bbox 3.5 x 17.8 x 2e-07 mm, 1 faces, 0 solids (baked)
FEATURE [Part::Revolution] Revolve099  label="removeToCreateScrewAndThreadedInsertHole026"
  Angle = 360
  Axis = (0,1,0)
  Base = (0,0,0)
  FaceMakerClass = Part::FaceMakerBullseye
  Placement = pos=(62.3,30.3,19.7) rot=(0,0,1;0rad)
  Solid = false
  Source = -> Face091
  Symmetric = false
FEATURE [Part::Revolution] Revolve100  label="removeToCreateScrewAndThreadedInsertHole027"
  Angle = 360
  Axis = (0,1,0)
  Base = (0,0,0)
  FaceMakerClass = Part::FaceMakerBullseye
  Placement = pos=(62.3,30.3,51.7) rot=(0,0,1;0rad)
  Solid = false
  Source = -> Face092
  Symmetric = false
FEATURE [Part::Revolution] Revolve101  label="removeToCreateScrewAndThreadedInsertHole028"
  Angle = 360
  Axis = (0,1,0)
  Base = (0,0,0)
  FaceMakerClass = Part::FaceMakerBullseye
  Placement = pos=(30.3,30.3,19.7) rot=(0,0,1;0rad)
  Solid = false
  Source = -> Face093
  Symmetric = false
FEATURE [Part::Revolution] Revolve102  label="removeToCreateScrewAndThreadedInsertHole029"
  Angle = 360
  Axis = (0,1,0)
  Base = (0,0,0)
  FaceMakerClass = Part::FaceMakerBullseye
  Placement = pos=(30.3,30.3,51.7) rot=(0,0,1;0rad)
  Solid = false
  Source = -> Face094
  Symmetric = false
FEATURE [Part::MultiFuse] Fusion068  label="createThreadedInsertHolesForFan002"
  Shapes = -> [Revolve099,Revolve100,Revolve101,Revolve102]
FEATURE [Part::Cut] Cut026  label="fanScrewHousing003"
  Base = -> Fusion067
  Tool = -> Fusion068
FEATURE [Sketcher::SketchObject] Sketch048
  FullyConstrained = false
  Placement = pos=(0,0,0) rot=(1,0,0;1.5708rad)
  sketch-geometry (24):
    g0: ArcOfCircle CenterX=-4 CenterY=-10.5 CenterZ=0 NormalX=0 NormalY=0 NormalZ=1 AngleXU=0 Radius=1.5 StartAngle=6e-16 EndAngle=3.14159
    g1: ArcOfCircle CenterX=-34.2 CenterY=-10.5 CenterZ=0 NormalX=0 NormalY=0 NormalZ=1 AngleXU=0 Radius=1.5 StartAngle=0 EndAngle=3.14159
    g2: ArcOfCircle CenterX=-34.2 CenterY=-27.7 CenterZ=0 NormalX=0 NormalY=0 NormalZ=1 AngleXU=0 Radius=1.5 StartAngle=3.14159 EndAngle=6.28319
    g3: ArcOfCircle CenterX=-4 CenterY=-27.7 CenterZ=0 NormalX=0 NormalY=0 NormalZ=1 AngleXU=0 Radius=1.5 StartAngle=3.1416 EndAngle=6.28319
    g4: ArcOfCircle CenterX=-10 CenterY=-4.3 CenterZ=0 NormalX=0 NormalY=0 NormalZ=1 AngleXU=0 Radius=1.5 StartAngle=2e-16 EndAngle=3.14159
    g5: ArcOfCircle CenterX=-16.1 CenterY=-1.8 CenterZ=0 NormalX=0 NormalY=0 NormalZ=1 AngleXU=0 Radius=1.5 StartAngle=5e-16 EndAngle=3.14159
    g6: ArcOfCircle CenterX=-22.1 CenterY=-1.8 CenterZ=0 NormalX=0 NormalY=0 NormalZ=1 AngleXU=0 Radius=1.5 StartAngle=5e-16 EndAngle=3.14159
    g7: ArcOfCircle CenterX=-28.2 CenterY=-4.3 CenterZ=0 NormalX=0 NormalY=0 NormalZ=1 AngleXU=0 Radius=1.5 StartAngle=2e-16 EndAngle=3.14159
    g8: ArcOfCircle CenterX=-10 CenterY=-33.9 CenterZ=0 NormalX=0 NormalY=0 NormalZ=1 AngleXU=0 Radius=1.5 StartAngle=3.14159 EndAngle=6.28319
    g9: ArcOfCircle CenterX=-16.1 CenterY=-36.4 CenterZ=0 NormalX=0 NormalY=0 NormalZ=1 AngleXU=0 Radius=1.5 StartAngle=3.14159 EndAngle=6.28319
    g10: ArcOfCircle CenterX=-22.1 CenterY=-36.4 CenterZ=0 NormalX=0 NormalY=0 NormalZ=1 AngleXU=0 Radius=1.5 StartAngle=3.14159 EndAngle=6.28319
    g11: ArcOfCircle CenterX=-28.2 CenterY=-33.9 CenterZ=0 NormalX=0 NormalY=0 NormalZ=1 AngleXU=0 Radius=1.5 StartAngle=3.14159 EndAngle=6.28319
    g12: LineSegment StartX=-35.7 StartY=-10.5 StartZ=0 EndX=-35.7 EndY=-27.7 EndZ=0
    g13: LineSegment StartX=-32.7 StartY=-10.5 StartZ=0 EndX=-32.7 EndY=-27.7 EndZ=0
    g14: LineSegment StartX=-29.7 StartY=-33.9 StartZ=0 EndX=-29.7 EndY=-4.3 EndZ=0
    g15: LineSegment StartX=-26.7 StartY=-33.9 StartZ=0 EndX=-26.7 EndY=-4.3 EndZ=0
    g16: LineSegment StartX=-2.5 StartY=-10.5 StartZ=0 EndX=-2.5 EndY=-27.7 EndZ=0
    g17: LineSegment StartX=-8.5 StartY=-4.3 StartZ=0 EndX=-8.5 EndY=-33.9 EndZ=0
    g18: LineSegment StartX=-5.5 StartY=-10.5 StartZ=0 EndX=-5.5 EndY=-27.7 EndZ=0
    g19: LineSegment StartX=-11.5 StartY=-4.3 StartZ=0 EndX=-11.5 EndY=-33.9 EndZ=0
    g20: LineSegment StartX=-14.6 StartY=-1.8 StartZ=0 EndX=-14.6 EndY=-36.4 EndZ=0
    g21: LineSegment StartX=-17.6 StartY=-1.8 StartZ=0 EndX=-17.6 EndY=-36.4 EndZ=0
    g22: LineSegment StartX=-20.6 StartY=-36.4 StartZ=0 EndX=-20.6 EndY=-1.8 EndZ=0
    g23: LineSegment StartX=-23.6 StartY=-1.8 StartZ=0 EndX=-23.6 EndY=-36.4 EndZ=0
  constraints (48):
    c: Block(g0)
    c: Block(g1)
    c: Block(g2)
    c: Block(g3)
    c: Block(g4)
    c: Block(g5)
    c: Block(g6)
    c: Block(g7)
    c: Block(g8)
    c: Block(g9)
    c: Block(g10)
    c: Block(g11)
    c: Coincident(g12,g1)
    c: Coincident(g12,g2)
    c: Vertical(g12)
    c: Coincident(g13,g1)
    c: Coincident(g13,g2)
    c: Vertical(g13)
    c: Coincident(g14,g11)
    c: Coincident(g14,g7)
    c: Vertical(g14)
    c: Coincident(g15,g11)
    c: Coincident(g15,g7)
    c: Vertical(g15)
    c: Coincident(g16,g0)
    c: Coincident(g16,g3)
    c: Vertical(g16)
    c: Coincident(g17,g4)
    c: Coincident(g17,g8)
    c: Vertical(g17)
    c: Coincident(g18,g0)
    c: Coincident(g18,g3)
    c: Vertical(g18)
    c: Coincident(g19,g4)
    c: Coincident(g19,g8)
    c: Vertical(g19)
    c: Coincident(g20,g5)
    c: Coincident(g20,g9)
    c: Vertical(g20)
    c: Coincident(g21,g5)
    c: Coincident(g21,g9)
    c: Vertical(g21)
    c: Coincident(g22,g10)
    c: Coincident(g22,g6)
    c: Vertical(g22)
    c: Coincident(g23,g6)
    c: Coincident(g23,g10)
    c: Vertical(g23)
FEATURE [Part::Extrusion] Extrude039  label="removeToCreateFanGrillHoles002"
  Base = -> Sketch048
  Dir = (0,-1,6e-16)
  DirMode = 2
  FaceMakerClass = Part::FaceMakerBullseye
  LengthFwd = 10
  LengthRev = 0
  Placement = pos=(65.4,44,54.82) rot=(0,0,1;0rad)
  Solid = true
  Symmetric = false
FEATURE [Part::Cut] Cut027  label="fanScrewHousing004"
  Base = -> Cut026
  Tool = -> Extrude038
FEATURE [Part::Cut] Cut028  label="top014"
  Base = -> Fillet026
  Tool = -> Extrude039
FEATURE [Part::Feature] Face095 .. Face098  x4 (patterned run collapsed; names and placements below)
  shape: bbox 3.5 x 17.8 x 2e-07 mm, 1 faces, 0 solids (baked)
FEATURE [Part::Revolution] Revolve103  label="removeToCreateScrewAndThreadedInsertHole030"
  Angle = 360
  Axis = (0,1,0)
  Base = (0,0,0)
  FaceMakerClass = Part::FaceMakerBullseye
  Placement = pos=(62.3,30.3,19.7) rot=(0,0,1;0rad)
  Solid = false
  Source = -> Face095
  Symmetric = false
FEATURE [Part::Revolution] Revolve104  label="removeToCreateScrewAndThreadedInsertHole031"
  Angle = 360
  Axis = (0,1,0)
  Base = (0,0,0)
  FaceMakerClass = Part::FaceMakerBullseye
  Placement = pos=(62.3,30.3,51.7) rot=(0,0,1;0rad)
  Solid = false
  Source = -> Face096
  Symmetric = false
FEATURE [Part::Revolution] Revolve105  label="removeToCreateScrewAndThreadedInsertHole032"
  Angle = 360
  Axis = (0,1,0)
  Base = (0,0,0)
  FaceMakerClass = Part::FaceMakerBullseye
  Placement = pos=(30.3,30.3,19.7) rot=(0,0,1;0rad)
  Solid = false
  Source = -> Face097
  Symmetric = false
FEATURE [Part::Revolution] Revolve106  label="removeToCreateScrewAndThreadedInsertHole033"
  Angle = 360
  Axis = (0,1,0)
  Base = (0,0,0)
  FaceMakerClass = Part::FaceMakerBullseye
  Placement = pos=(30.3,30.3,51.7) rot=(0,0,1;0rad)
  Solid = false
  Source = -> Face098
  Symmetric = false
FEATURE [Part::MultiFuse] Fusion069  label="createThreadedInsertHolesForFan003"
  Shapes = -> [Revolve103,Revolve104,Revolve105,Revolve106]
FEATURE [Part::Cut] Cut029  label="top015"
  Base = -> Cut028
  Tool = -> Fusion054
FEATURE [Part::Cut] Cut030  label="fanScrewHousing005"
  Base = -> Cut027
  Tool = -> Fusion069
FEATURE [Part::Cylinder] Cylinder026  label="removeToCreteHoleForPlugHousing010"
  Angle = 360
  AttacherType = Attacher::AttachEngine3D
  Height = 20
  Placement = pos=(-2,19,36) rot=(0,1,0;1.5708rad)
  Radius = 14.3
FEATURE [Part::Box] Box018  label="removeToCreteHoleForPlugHousing011"
  AttacherType = Attacher::AttachEngine3D
  Height = 28.6
  Length = 10
  Placement = pos=(-2,0,21.7) rot=(0,0,1;0rad)
  Width = 19
FEATURE [Part::Box] Box019  label="wireHolderBottomCaseBit"
  AttacherType = Attacher::AttachEngine3D
  Height = 28
  Length = 3
  Placement = pos=(0,0,22) rot=(0,0,1;0rad)
  Width = 21
FEATURE [Part::Cylinder] Cylinder027  label="removeToCreteHoleForPlugHousing012"
  Angle = 360
  AttacherType = Attacher::AttachEngine3D
  Height = 20
  Placement = pos=(-2,19,36) rot=(0,1,0;1.5708rad)
  Radius = 14.3
FEATURE [Part::Cut] Cut031  label="wireHolderBottomCaseBit001"
  Base = -> Box019
  Tool = -> Cylinder027
FEATURE [Part::MultiFuse] Fusion070  label="removeToCreteHoleForPlugHousing013"
  Shapes = -> [Box018,Cylinder026]
FEATURE [Part::Cut] Cut032  label="top016"
  Base = -> Cut029
  Tool = -> Fusion070
FEATURE [Part::Cylinder] Cylinder028
  Angle = 360
  AttacherType = Attacher::AttachEngine3D
  Height = 20
  Placement = pos=(0,0,36.15) rot=(0,0,1;0rad)
  Radius = 14.3
FEATURE [Part::Cylinder] Cylinder029
  Angle = 360
  AttacherType = Attacher::AttachEngine3D
  Height = 10
  Placement = pos=(0,0,36.15) rot=(0,0,1;0rad)
  Radius = 4
FEATURE [Part::MultiFuse] Fusion071  label="removeToCreteHoleForPlugHousing014"
  Placement = pos=(70,19,36) rot=(0,1,0;1.5708rad)
  Shapes = -> [Cylinder028,Cylinder029]
FEATURE [Sketcher::SketchObject] Sketch049  label="topSketch011"
  FullyConstrained = true
  sketch-geometry (4):
    g0: ArcOfCircle CenterX=105 CenterY=19 CenterZ=0 NormalX=0 NormalY=0 NormalZ=1 AngleXU=0 Radius=20.6155 StartAngle=5.54125 EndAngle=6.28319
    g1: ArcOfCircle CenterX=105 CenterY=19 CenterZ=0 NormalX=0 NormalY=0 NormalZ=1 AngleXU=0 Radius=13 StartAngle=5.54125 EndAngle=6.28319
    g2: LineSegment StartX=118 StartY=19 StartZ=0 EndX=125.616 EndY=19 EndZ=0
    g3: LineSegment StartX=114.583 StartY=10.2157 StartZ=0 EndX=120.197 EndY=5.06982 EndZ=0
  constraints (7):
    c: Block(g0)
    c: Block(g1)
    c: Coincident(g2,g1)
    c: Coincident(g2,g0)
    c: Horizontal(g2)
    c: Coincident(g3,g1)
    c: Coincident(g3,g0)
FEATURE [Part::Box] Box020  label="removeToCreteHoleForPlugHousing015"
  AttacherType = Attacher::AttachEngine3D
  Height = 28.6
  Length = 20
  Placement = pos=(106.15,0,21.7) rot=(0,0,1;0rad)
  Width = 19
FEATURE [Part::MultiFuse] Fusion072  label="removeToCreteHoleForPlugHousing016"
  Shapes = -> [Box020,Fusion071]
FEATURE [Part::Cut] Cut033  label="removeToCreteHoleForPlugHousing017"
  Base = -> Cut032
  Tool = -> Fusion072
FEATURE [Part::Cylinder] Cylinder030
  Angle = 360
  AttacherType = Attacher::AttachEngine3D
  Height = 20
  Placement = pos=(0,0,36.15) rot=(0,0,1;0rad)
  Radius = 14.3
FEATURE [Part::Cylinder] Cylinder031
  Angle = 360
  AttacherType = Attacher::AttachEngine3D
  Height = 10
  Placement = pos=(0,0,36.15) rot=(0,0,1;0rad)
  Radius = 4
FEATURE [Part::Box] Box021  label="removeToCreteHoleForPlugHousing019"
  AttacherType = Attacher::AttachEngine3D
  Height = 28.6
  Length = 20
  Placement = pos=(106.15,0,21.7) rot=(0,0,1;0rad)
  Width = 19
FEATURE [Part::MultiFuse] Fusion074  label="removeToCreteHoleForPlugHousing020"
  Placement = pos=(70,19,36) rot=(0,1,0;1.5708rad)
  Shapes = -> [Cylinder030,Cylinder031]
FEATURE [Part::MultiFuse] Fusion073  label="removeToCreteHoleForPlugHousing018"
  Placement = pos=(0,0,28.3) rot=(0,0,1;0rad)
  Shapes = -> [Box021,Fusion074]
FEATURE [Part::Cylinder] Cylinder032
  Angle = 360
  AttacherType = Attacher::AttachEngine3D
  Height = 20
  Placement = pos=(0,0,36.15) rot=(0,0,1;0rad)
  Radius = 14.3
FEATURE [Part::Cylinder] Cylinder033
  Angle = 360
  AttacherType = Attacher::AttachEngine3D
  Height = 10
  Placement = pos=(0,0,36.15) rot=(0,0,1;0rad)
  Radius = 4
FEATURE [Part::Box] Box022  label="removeToCreteHoleForPlugHousing021"
  AttacherType = Attacher::AttachEngine3D
  Height = 28.6
  Length = 20
  Placement = pos=(106.15,0,21.7) rot=(0,0,1;0rad)
  Width = 19
FEATURE [Part::MultiFuse] Fusion076  label="removeToCreteHoleForPlugHousing023"
  Placement = pos=(70,19,36) rot=(0,1,0;1.5708rad)
  Shapes = -> [Cylinder032,Cylinder033]
FEATURE [Part::MultiFuse] Fusion075  label="removeToCreteHoleForPlugHousing022"
  Placement = pos=(0,0,-28.3) rot=(0,0,1;0rad)
  Shapes = -> [Box022,Fusion076]
FEATURE [Part::MultiFuse] Fusion077  label="removeToCreatePlugHousingBottomBit"
  Shapes = -> [Fusion075,Fusion073]
FEATURE [Part::Cylinder] Cylinder034
  Angle = 360
  AttacherType = Attacher::AttachEngine3D
  Height = 20
  Placement = pos=(0,0,36.15) rot=(0,0,1;0rad)
  Radius = 14
FEATURE [Part::Cylinder] Cylinder035
  Angle = 360
  AttacherType = Attacher::AttachEngine3D
  Height = 10
  Placement = pos=(0,0,36.15) rot=(0,0,1;0rad)
  Radius = 4
FEATURE [Part::MultiFuse] Fusion078  label="removeToCreteHoleForPlugHousing024"
  Placement = pos=(70,19,36) rot=(0,1,0;1.5708rad)
  Shapes = -> [Cylinder034,Cylinder035]
FEATURE [Part::MultiFuse] Fusion079  label="removeToCreatePlugHousingBottomBit001"
  Shapes = -> [Fusion078,Fusion077]
FEATURE [Part::Extrusion] Extrude040  label="bottomPlugHousingBit"
  Base = -> Sketch049
  Dir = (0,0,1)
  DirMode = 2
  FaceMakerClass = Part::FaceMakerBullseye
  LengthFwd = 72
  LengthRev = 0
  Solid = true
  Symmetric = false
FEATURE [Part::Cut] Cut034  label="bottomPlugHousingBit001"
  Base = -> Extrude040
  Placement = pos=(-0.09,0,0) rot=(0,0,1;0rad)
  Tool = -> Fusion079
FEATURE [Part::Box] Box023  label="Cube014"
  AttacherType = Attacher::AttachEngine3D
  Height = 16
  Length = 8
  Placement = pos=(12.7,31.52,28) rot=(0,0,1;0rad)
  Width = 4
FEATURE [Part::Cylinder] Cylinder036
  Angle = 360
  AttacherType = Attacher::AttachEngine3D
  Height = 10
  Placement = pos=(0,0,36.15) rot=(0,0,1;0rad)
  Radius = 4
FEATURE [Part::Cylinder] Cylinder037
  Angle = 360
  AttacherType = Attacher::AttachEngine3D
  Height = 20
  Placement = pos=(0,0,36.15) rot=(0,0,1;0rad)
  Radius = 8.2
FEATURE [Part::MultiFuse] Fusion080  label="removeToCreteHoleForPlugHousing025"
  Placement = pos=(-42,19,36) rot=(0,1,0;1.5708rad)
  Shapes = -> [Cylinder037,Cylinder036]
FEATURE [Sketcher::SketchObject] Sketch050  label="topSketch012"
  FullyConstrained = true
  sketch-geometry (4):
    g0: LineSegment StartX=16.8446 StartY=31.512 StartZ=0 EndX=16.3251 EndY=34.4666 EndZ=0
    g1: ArcOfCircle CenterX=19 CenterY=19.2524 CenterZ=0 NormalX=0 NormalY=0 NormalZ=1 AngleXU=0 Radius=15.4476 StartAngle=1.74483 EndAngle=2.72717
    g2: ArcOfCircle CenterX=19 CenterY=19.2524 CenterZ=0 NormalX=0 NormalY=0 NormalZ=1 AngleXU=0 Radius=12.4476 StartAngle=1.74483 EndAngle=2.73189
    g3: LineSegment StartX=4.86004 StartY=25.4725 StartZ=0 EndX=7.58253 EndY=24.2107 EndZ=0
  constraints (7):
    c: Block(g0)
    c: Coincident(g1,g0)
    c: Coincident(g2,g0)
    c: Coincident(g3,g1)
    c: Coincident(g3,g2)
    c: Block(g1)
    c: Block(g2)
FEATURE [Part::Extrusion] Extrude041
  Base = -> Sketch050
  Dir = (0,0,1)
  DirMode = 2
  FaceMakerClass = Part::FaceMakerBullseye
  LengthFwd = 10.6
  LengthRev = 0
  Placement = pos=(0,0,31) rot=(0,0,1;0rad)
  Solid = true
  Symmetric = false
FEATURE [Part::Cut] Cut035
  Base = -> Extrude041
  Placement = pos=(0,0,-0.3) rot=(0,0,1;0rad)
  Tool = -> Fusion080
FEATURE [Part::Cut] Cut036
  Base = -> Box023
  Tool = -> Cut035
FEATURE [Part::Fillet] Fillet027
  Base = -> Cut036
  Edges = 1 edges r=0.7: [Edge13]
FEATURE [Part::Fillet] Fillet028
  Base = -> Fillet027
  Edges = 1 edges r=0.7: [Edge13]
FEATURE [Part::Fillet] Fillet029
  Base = -> Fillet028
  Edges = 1 edges r=0.7: [Edge16]
FEATURE [Part::Fillet] Fillet030
  Base = -> Fillet029
  Edges = 1 edges r=0.7: [Edge11]
FEATURE [Part::Fillet] Fillet031
  Base = -> Fillet030
  Edges = 1 edges r=0.7: [Edge10]
FEATURE [Part::Fillet] Fillet032
  Base = -> Fillet031
  Edges = 1 edges r=1.2: [Edge5]
FEATURE [Part::Fillet] Fillet033
  Base = -> Fillet032
  Edges = 1 edges r=1.2: [Edge12]
FEATURE [Part::Fillet] Fillet034  label="wireHousingRetainer"
  Base = -> Fillet033
  Edges = 1 edges r=2: [Edge1]
  Placement = pos=(0.3,0,0) rot=(0,0,1;0rad)
FEATURE [Part::Feature] Face099
  shape: bbox 3.5 x 17.8 x 2e-07 mm, 1 faces, 0 solids (baked)
FEATURE [Part::Revolution] Revolve107  label="removeToCreateScrewAndThreadedInsertHole034"
  Angle = 360
  Axis = (0,1,0)
  Base = (0,0,0)
  FaceMakerClass = Part::FaceMakerBullseye
  Placement = pos=(12.5,0,10) rot=(0,0,1;0rad)
  Solid = false
  Source = -> Face099
  Symmetric = false
FEATURE [Part::Feature] Face100
  shape: bbox 3.5 x 17.8 x 2e-07 mm, 1 faces, 0 solids (baked)
FEATURE [Part::Revolution] Revolve108  label="removeToCreateScrewAndThreadedInsertHole035"
  Angle = 360
  Axis = (0,1,0)
  Base = (0,0,0)
  FaceMakerClass = Part::FaceMakerBullseye
  Placement = pos=(12.5,0,62) rot=(0,0,1;0rad)
  Solid = false
  Source = -> Face100
  Symmetric = false
FEATURE [Part::Feature] Face101
  shape: bbox 3.5 x 17.8 x 2e-07 mm, 1 faces, 0 solids (baked)
FEATURE [Part::Revolution] Revolve109  label="removeToCreateScrewAndThreadedInsertHole036"
  Angle = 360
  Axis = (0,1,0)
  Base = (0,0,0)
  FaceMakerClass = Part::FaceMakerBullseye
  Placement = pos=(89.5,0,68.5) rot=(0,0,1;0rad)
  Solid = false
  Source = -> Face101
  Symmetric = false
FEATURE [Part::Feature] Face102
  shape: bbox 3.5 x 17.8 x 2e-07 mm, 1 faces, 0 solids (baked)
FEATURE [Part::Revolution] Revolve110  label="removeToCreateScrewAndThreadedInsertHole037"
  Angle = 360
  Axis = (0,1,0)
  Base = (0,0,0)
  FaceMakerClass = Part::FaceMakerBullseye
  Placement = pos=(89.5,0,3.5) rot=(0,0,1;0rad)
  Solid = false
  Source = -> Face102
  Symmetric = false
FEATURE [Part::Feature] Face103
  shape: bbox 3.5 x 17.8 x 2e-07 mm, 1 faces, 0 solids (baked)
FEATURE [Part::Revolution] Revolve111  label="removeToCreateScrewAndThreadedInsertHole038"
  Angle = 360
  Axis = (0,1,0)
  Base = (0,0,0)
  FaceMakerClass = Part::FaceMakerBullseye
  Placement = pos=(109.5,4.7,3.5) rot=(0,0,1;0rad)
  Solid = false
  Source = -> Face103
  Symmetric = false
FEATURE [Part::Feature] Face104
  shape: bbox 3.5 x 17.8 x 2e-07 mm, 1 faces, 0 solids (baked)
FEATURE [Part::Revolution] Revolve112  label="removeToCreateScrewAndThreadedInsertHole039"
  Angle = 360
  Axis = (0,1,0)
  Base = (0,0,0)
  FaceMakerClass = Part::FaceMakerBullseye
  Placement = pos=(109.5,4.7,68.5) rot=(0,0,1;0rad)
  Solid = false
  Source = -> Face104
  Symmetric = false
FEATURE [Part::MultiFuse] Fusion081  label="removeToCreateScrewAndThreadedInsertHole040"
  Shapes = -> [Revolve107,Revolve108,Revolve109,Revolve110,Revolve111,Revolve112]
FEATURE [Part::MultiFuse] Fusion082  label="casePillars002"
  Shapes = -> [Revolve094,Revolve092,Revolve090,Revolve089,Revolve091,Revolve093]
FEATURE [Part::Cut] Cut037  label="casePillars003"
  Base = -> Fusion082
  Tool = -> Fusion081
FEATURE [Sketcher::SketchObject] Sketch051
  FullyConstrained = true
  Placement = pos=(117,19,0) rot=(0.57735,0.57735,0.57735;2.0944rad)
  sketch-geometry (48):
    g0: LineSegment StartX=-49.19 StartY=69.25 StartZ=0 EndX=-49.19 EndY=66.25 EndZ=0
    g1: LineSegment StartX=-49.19 StartY=63.5 StartZ=0 EndX=-49.19 EndY=60.5 EndZ=0
    g2: LineSegment StartX=-49.19 StartY=57.75 StartZ=0 EndX=-49.19 EndY=54.75 EndZ=0
    g3: LineSegment StartX=-49.19 StartY=52 StartZ=0 EndX=-49.19 EndY=49 EndZ=0
    g4: LineSegment StartX=-49.19 StartY=46.25 StartZ=0 EndX=-49.19 EndY=43.25 EndZ=0
    g5: LineSegment StartX=-49.19 StartY=40.5 StartZ=0 EndX=-49.19 EndY=37.5 EndZ=0
    g6: LineSegment StartX=-49.19 StartY=34.5 StartZ=0 EndX=-49.19 EndY=31.5 EndZ=0
    g7: LineSegment StartX=-49.19 StartY=28.75 StartZ=0 EndX=-49.19 EndY=25.75 EndZ=0
    g8: LineSegment StartX=-49.19 StartY=23 StartZ=0 EndX=-49.19 EndY=20 EndZ=0
    g9: LineSegment StartX=-49.19 StartY=17.25 StartZ=0 EndX=-49.19 EndY=14.25 EndZ=0
    g10: LineSegment StartX=-49.19 StartY=11.5 StartZ=0 EndX=-49.19 EndY=8.5 EndZ=0
    g11: LineSegment StartX=-49.19 StartY=5.75 StartZ=0 EndX=-49.19 EndY=2.75 EndZ=0
    g12: ArcOfCircle CenterX=-1.5 CenterY=67.75 CenterZ=0 NormalX=0 NormalY=0 NormalZ=1 AngleXU=0 Radius=1.5 StartAngle=4.71239 EndAngle=7.85398
    g13: ArcOfCircle CenterX=-1.5 CenterY=62 CenterZ=0 NormalX=0 NormalY=0 NormalZ=1 AngleXU=0 Radius=1.5 StartAngle=4.71239 EndAngle=7.85398
    g14: ArcOfCircle CenterX=-1.5 CenterY=56.25 CenterZ=0 NormalX=0 NormalY=0 NormalZ=1 AngleXU=0 Radius=1.5 StartAngle=4.71239 EndAngle=7.85398
    g15: ArcOfCircle CenterX=-11.49 CenterY=50.5 CenterZ=0 NormalX=0 NormalY=0 NormalZ=1 AngleXU=0 Radius=1.5 StartAngle=4.71239 EndAngle=7.85398
    g16: ArcOfCircle CenterX=-16.28 CenterY=44.75 CenterZ=0 NormalX=0 NormalY=0 NormalZ=1 AngleXU=0 Radius=1.5 StartAngle=4.71239 EndAngle=7.85398
    g17: ArcOfCircle CenterX=-18.2337 CenterY=39 CenterZ=0 NormalX=0 NormalY=0 NormalZ=1 AngleXU=0 Radius=1.5 StartAngle=4.71485 EndAngle=7.85398
    g18: ArcOfCircle CenterX=-16.2837 CenterY=27.25 CenterZ=0 NormalX=0 NormalY=0 NormalZ=1 AngleXU=0 Radius=1.5 StartAngle=4.71485 EndAngle=7.85398
    g19: ArcOfCircle CenterX=-18.2337 CenterY=33 CenterZ=0 NormalX=0 NormalY=0 NormalZ=1 AngleXU=0 Radius=1.5 StartAngle=4.71485 EndAngle=7.85398
    g20: ArcOfCircle CenterX=-11.49 CenterY=21.5 CenterZ=0 NormalX=0 NormalY=0 NormalZ=1 AngleXU=0 Radius=1.5 StartAngle=4.71239 EndAngle=7.85398
    g21: ArcOfCircle CenterX=-1.5 CenterY=4.25 CenterZ=0 NormalX=0 NormalY=0 NormalZ=1 AngleXU=0 Radius=1.5 StartAngle=4.71239 EndAngle=7.85398
    g22: ArcOfCircle CenterX=-1.5 CenterY=10 CenterZ=0 NormalX=0 NormalY=0 NormalZ=1 AngleXU=0 Radius=1.5 StartAngle=4.71239 EndAngle=7.85398
    g23: ArcOfCircle CenterX=-1.5 CenterY=15.75 CenterZ=0 NormalX=0 NormalY=0 NormalZ=1 AngleXU=0 Radius=1.5 StartAngle=4.71239 EndAngle=7.85398
    g24: LineSegment StartX=-49.19 StartY=69.25 StartZ=0 EndX=-1.5 EndY=69.25 EndZ=0
    g25: LineSegment StartX=-49.19 StartY=66.25 StartZ=0 EndX=-1.5 EndY=66.25 EndZ=0
    g26: LineSegment StartX=-49.19 StartY=63.5 StartZ=0 EndX=-1.5 EndY=63.5 EndZ=0
    g27: LineSegment StartX=-49.19 StartY=60.5 StartZ=0 EndX=-1.5 EndY=60.5 EndZ=0
    g28: LineSegment StartX=-49.19 StartY=57.75 StartZ=0 EndX=-1.5 EndY=57.75 EndZ=0
    g29: LineSegment StartX=-49.19 StartY=54.75 StartZ=0 EndX=-1.5 EndY=54.75 EndZ=0
    g30: LineSegment StartX=-49.19 StartY=52 StartZ=0 EndX=-11.49 EndY=52 EndZ=0
    g31: LineSegment StartX=-49.19 StartY=49 StartZ=0 EndX=-11.49 EndY=49 EndZ=0
    g32: LineSegment StartX=-49.19 StartY=46.25 StartZ=0 EndX=-16.28 EndY=46.25 EndZ=0
    g33: LineSegment StartX=-49.19 StartY=43.25 StartZ=0 EndX=-16.28 EndY=43.25 EndZ=0
    g34: LineSegment StartX=-49.19 StartY=40.5 StartZ=0 EndX=-18.2337 EndY=40.5 EndZ=0
    g35: LineSegment StartX=-49.19 StartY=37.5 StartZ=0 EndX=-18.23 EndY=37.5 EndZ=0
    g36: LineSegment StartX=-49.19 StartY=34.5 StartZ=0 EndX=-18.2337 EndY=34.5 EndZ=0
    g37: LineSegment StartX=-49.19 StartY=31.5 StartZ=0 EndX=-18.23 EndY=31.5 EndZ=0
    g38: LineSegment StartX=-49.19 StartY=28.75 StartZ=0 EndX=-16.2837 EndY=28.75 EndZ=0
    g39: LineSegment StartX=-49.19 StartY=25.75 StartZ=0 EndX=-16.28 EndY=25.75 EndZ=0
    g40: LineSegment StartX=-49.19 StartY=23 StartZ=0 EndX=-11.49 EndY=23 EndZ=0
    g41: LineSegment StartX=-49.19 StartY=20 StartZ=0 EndX=-11.49 EndY=20 EndZ=0
    g42: LineSegment StartX=-49.19 StartY=17.25 StartZ=0 EndX=-1.5 EndY=17.25 EndZ=0
    g43: LineSegment StartX=-49.19 StartY=14.25 StartZ=0 EndX=-1.5 EndY=14.25 EndZ=0
    g44: LineSegment StartX=-49.19 StartY=11.5 StartZ=0 EndX=-1.5 EndY=11.5 EndZ=0
    g45: LineSegment StartX=-49.19 StartY=8.5 StartZ=0 EndX=-1.5 EndY=8.5 EndZ=0
    g46: LineSegment StartX=-49.19 StartY=5.75 StartZ=0 EndX=-1.5 EndY=5.75 EndZ=0
    g47: LineSegment StartX=-49.19 StartY=2.75 StartZ=0 EndX=-1.5 EndY=2.75 EndZ=0
  constraints (120):
    c: Vertical(g0)
    c: Distance(g0) = 3
    c: Block(g0)
    c: Vertical(g1)
    c: Distance(g1) = 3
    c: Vertical(g2)
    c: Equal(g0,g2) = 3
    c: Block(g2)
    c: Vertical(g3)
    c: Equal(g1,g3) = 3
    c: Vertical(g4)
    c: Equal(g0,g4) = 3
    c: Block(g4)
    c: Vertical(g5)
    c: Equal(g1,g5) = 3
    c: Vertical(g6)
    c: Equal(g0,g6) = 3
    c: Block(g6)
    c: Vertical(g7)
    c: Equal(g1,g7) = 3
    c: Vertical(g8)
    c: Equal(g0,g8) = 3
    c: Block(g8)
    c: Vertical(g9)
    c: Equal(g1,g9) = 3
    c: Vertical(g10)
    c: Equal(g0,g10) = 3
    c: Block(g10)
    c: Vertical(g11)
    c: Equal(g1,g11) = 3
    c: Block(g12)
    c: Block(g13)
    c: Block(g14)
    c: Block(g15)
    c: Block(g16)
    c: Block(g17)
    c: Block(g18)
    c: Block(g19)
    c: Block(g20)
    c: Block(g21)
    c: Block(g22)
    c: Block(g23)
    c: Block(g11)
    c: Block(g9)
    c: Block(g7)
    c: Block(g5)
    c: Block(g3)
    c: Block(g1)
    c: Coincident(g24,g0)
    c: Coincident(g24,g12)
    c: Horizontal(g24)
    c: Coincident(g25,g0)
    c: Coincident(g25,g12)
    c: Horizontal(g25)
    c: Coincident(g26,g1)
    c: Coincident(g26,g13)
    c: Horizontal(g26)
    c: Coincident(g27,g1)
    c: Coincident(g27,g13)
    c: Horizontal(g27)
    c: Coincident(g28,g2)
    c: Coincident(g28,g14)
    c: Horizontal(g28)
    c: Coincident(g29,g2)
    c: Coincident(g29,g14)
    c: Horizontal(g29)
    c: Coincident(g30,g3)
    c: Coincident(g30,g15)
    c: Horizontal(g30)
    c: Coincident(g31,g3)
    c: Coincident(g31,g15)
    c: Horizontal(g31)
    c: Coincident(g32,g4)
    c: Coincident(g32,g16)
    c: Horizontal(g32)
    c: Coincident(g33,g4)
    c: Coincident(g33,g16)
    c: Horizontal(g33)
    c: Coincident(g34,g5)
    c: Coincident(g34,g17)
    c: Horizontal(g34)
    c: Coincident(g35,g5)
    c: Coincident(g35,g17)
    c: Horizontal(g35)
    c: Coincident(g36,g6)
    c: Coincident(g36,g19)
    c: Horizontal(g36)
    c: Coincident(g37,g6)
    c: Coincident(g37,g19)
    c: Horizontal(g37)
    c: Coincident(g38,g7)
    c: Coincident(g38,g18)
    c: Horizontal(g38)
    c: Coincident(g39,g7)
    c: Coincident(g39,g18)
    c: Horizontal(g39)
    c: Coincident(g40,g8)
    c: Coincident(g40,g20)
    c: Horizontal(g40)
    c: Coincident(g41,g8)
    c: Coincident(g41,g20)
    c: Horizontal(g41)
    c: Coincident(g42,g9)
    c: Coincident(g42,g23)
    c: Horizontal(g42)
    c: Coincident(g43,g9)
    c: Coincident(g43,g23)
    c: Horizontal(g43)
    c: Coincident(g44,g10)
    c: Coincident(g44,g22)
    c: Horizontal(g44)
    c: Coincident(g45,g10)
    c: Coincident(g45,g22)
    c: Horizontal(g45)
    c: Coincident(g46,g11)
    c: Coincident(g46,g21)
    c: Horizontal(g46)
    c: Coincident(g47,g11)
    c: Coincident(g47,g21)
    c: Horizontal(g47)
FEATURE [Part::Extrusion] Extrude042
  Base = -> Sketch051
  Dir = (1,-2e-16,2e-16)
  DirMode = 2
  FaceMakerClass = Part::FaceMakerBullseye
  LengthFwd = 19
  LengthRev = 0
  Placement = pos=(-19,0,0) rot=(0,0,1;0rad)
  Solid = true
  Symmetric = false
FEATURE [Part::Fillet] Fillet035  label="removeToCreateVentalationHoles"
  Base = -> Extrude042
  Edges = <same value as first occurrence — deduplicated (x4 in doc)>
  Placement = pos=(7,0,0) rot=(0,0,1;0rad)
FEATURE [Part::Cut] Cut038  label="top017"
  Base = -> Cut033
  Tool = -> Fillet035
FEATURE [Sketcher::SketchObject] Sketch052  label="bottomSketch001"
  FullyConstrained = true
  sketch-geometry (26):
    g0: LineSegment StartX=6.29999 StartY=8 StartZ=0 EndX=3.29999 EndY=8 EndZ=0
    g1: LineSegment StartX=3.29999 StartY=8 StartZ=0 EndX=3.29999 EndY=-6.03275e-07 EndZ=0
    g2: ArcOfCircle CenterX=8.29999 CenterY=5 CenterZ=0 NormalX=0 NormalY=0 NormalZ=1 AngleXU=0 Radius=2 StartAngle=3.14159 EndAngle=4.71239
    g3: LineSegment StartX=6.29999 StartY=8 StartZ=0 EndX=6.29999 EndY=5 EndZ=0
    g4: ArcOfCircle CenterX=105 CenterY=19 CenterZ=0 NormalX=0 NormalY=0 NormalZ=1 AngleXU=0 Radius=12.7 StartAngle=4.71239 EndAngle=6.28319
    g5-g11: Circle x7 (B-spline internal-alignment scaffolding for g12; pole/knot coordinates omitted)
    g12: BSplineCurve PolesCount=7 KnotsCount=5 Degree=3 IsPeriodic=0
    g13-g17: GeomPoint x5 (B-spline internal-alignment scaffolding for g12; pole/knot coordinates omitted)
    g18: ArcOfCircle CenterX=105 CenterY=19 CenterZ=0 NormalX=0 NormalY=0 NormalZ=1 AngleXU=0 Radius=15.7 StartAngle=5.81226 EndAngle=6.28319
    g19: LineSegment StartX=117.7 StartY=19 StartZ=0 EndX=120.7 EndY=19 EndZ=0
    g20: BSplineCurve PolesCount=5 KnotsCount=3 Degree=3 IsPeriodic=0
    g21: LineSegment StartX=8.29999 StartY=3 StartZ=0 EndX=101.7 EndY=3 EndZ=0
    g22: LineSegment StartX=3.29999 StartY=-6.03275e-07 StartZ=0 EndX=105 EndY=-6.03275e-07 EndZ=0
    g23: LineSegment StartX=120.974 StartY=8.71251 StartZ=0 EndX=122.332 EndY=7.83778 EndZ=0
    g24: LineSegment StartX=105 StartY=-6.03274e-07 StartZ=0 EndX=113 EndY=-6.03274e-07 EndZ=0
    g25: ArcOfCircle CenterX=105 CenterY=19 CenterZ=0 NormalX=0 NormalY=0 NormalZ=1 AngleXU=0 Radius=20.6155 StartAngle=5.11091 EndAngle=5.71103
  constraints (38):
    c: Horizontal(g0)
    c: Distance(g0) = 3
    c: Coincident(g1,g0)
    c: Vertical(g1)
    c: Block(g2)
    c: Block(g0)
    c: Coincident(g3,g0)
    c: Coincident(g3,g2)
    c: Vertical(g3)
    c: Block(g1)
    c: Block(g4)
    c: Coincident(g20,g4)
    c: Block(g20)
    c: Equal(g5, g6-g11) x6
    c: InternalAlignment(g5-g11 -> g12) x7
    c: InternalAlignment(g13-g17 -> g12) x5
    c: Block(g12)
    c: Coincident(g18,g12)
    c: Coincident(g19,g4)
    c: Coincident(g19,g18)
    c: Horizontal(g19)
    c: Block(g19)
    c: Block(g18)
    c: Coincident(g21,g2)
    c: Coincident(g21,g20)
    c: Horizontal(g21)
    c: Distance(g21) = 93.4
    c: Coincident(g22,g1)
    c: Horizontal(g22)
    c: Distance(g22) = 101.7
    c: Horizontal(g24)
    c: Distance(g24) = 8
    c: Coincident(g25,g24)
    c: Block(g24)
    c: Coincident(g23,g25)
    c: Block(g25)
    c: Block(g23)
    c: Distance(g23) = 1.61553
FEATURE [Part::Extrusion] Extrude043  label="bottom010"
  Base = -> Sketch052
  Dir = (0,0,1)
  DirMode = 2
  FaceMakerClass = Part::FaceMakerBullseye
  LengthFwd = 71.4
  LengthRev = 0
  Placement = pos=(0,0,0.3) rot=(0,0,1;0rad)
  Solid = true
  Symmetric = false
FEATURE [Sketcher::SketchObject] Sketch053  label="topSketch013"
  FullyConstrained = true
  sketch-geometry (22):
    g0: LineSegment StartX=5.21097e-06 StartY=3 StartZ=0 EndX=5.21097e-06 EndY=19 EndZ=0
    g1: ArcOfCircle CenterX=19 CenterY=19 CenterZ=0 NormalX=0 NormalY=0 NormalZ=1 AngleXU=0 Radius=19 StartAngle=1.5708 EndAngle=3.14159
    g2: ArcOfCircle CenterX=19 CenterY=19 CenterZ=0 NormalX=0 NormalY=0 NormalZ=1 AngleXU=0 Radius=16 StartAngle=1.5708 EndAngle=3.14159
    g3: LineSegment StartX=114 StartY=35 StartZ=0 EndX=19 EndY=35 EndZ=0
    g4: LineSegment StartX=5.21097e-06 StartY=3 StartZ=0 EndX=5.21097e-06 EndY=0 EndZ=0
    g5: LineSegment StartX=3 StartY=0 StartZ=0 EndX=5.21097e-06 EndY=0 EndZ=0
    g6: LineSegment StartX=3 StartY=19 StartZ=0 EndX=3 EndY=0 EndZ=0
    g7: LineSegment StartX=19 StartY=38 StartZ=0 EndX=124 EndY=38 EndZ=0
    g8: Circle CenterX=119 CenterY=35 CenterZ=0 NormalX=0 NormalY=0 NormalZ=1 AngleXU=0 Radius=1
    g9: Circle CenterX=121 CenterY=35 CenterZ=0 NormalX=0 NormalY=0 NormalZ=1 AngleXU=0 Radius=1
    g10: Circle CenterX=121 CenterY=33 CenterZ=0 NormalX=0 NormalY=0 NormalZ=1 AngleXU=0 Radius=1
    g11: BSplineCurve PolesCount=3 KnotsCount=2 Degree=2 IsPeriodic=0
    g12: GeomPoint X=119 Y=35 Z=0
    g13: GeomPoint X=121 Y=33 Z=0
    g14: LineSegment StartX=119 StartY=35 StartZ=0 EndX=114 EndY=35 EndZ=0
    g15: ArcOfCircle CenterX=105 CenterY=19 CenterZ=0 NormalX=0 NormalY=0 NormalZ=1 AngleXU=0 Radius=16 StartAngle=5.60905 EndAngle=6.28319
    g16: LineSegment StartX=121 StartY=33 StartZ=0 EndX=121 EndY=19 EndZ=0
    g17: LineSegment StartX=117.5 StartY=9.01251 StartZ=0 EndX=121.163 EndY=9.0125 EndZ=0
    g18: ArcOfCircle CenterX=105 CenterY=19 CenterZ=0 NormalX=0 NormalY=0 NormalZ=1 AngleXU=0 Radius=20.6155 StartAngle=5.7297 EndAngle=6.28319
    g19: LineSegment StartX=121.163 StartY=9.0125 StartZ=0 EndX=122.538 EndY=8.16329 EndZ=0
    g20: LineSegment StartX=124 StartY=38 StartZ=0 EndX=125.616 EndY=38 EndZ=0
    g21: LineSegment StartX=125.616 StartY=19 StartZ=0 EndX=125.616 EndY=38 EndZ=0
  constraints (50):
    c: Vertical(g0)
    c: Block(g0)
    c: Coincident(g1,g0)
    c: Block(g1)
    c: Coincident(g2,g1)
    c: Block(g2)
    c: Coincident(g3,g2)
    c: Horizontal(g3)
    c: Tangent(g3,g2)
    c: Coincident(g4,g0)
    c: Distance(g4) = 3
    c: Vertical(g4)
    c: Coincident(g5,g4)
    c: Horizontal(g5)
    c: Coincident(g6,g2)
    c: Coincident(g6,g5)
    c: Vertical(g6)
    c: Horizontal(g7)
    c: Distance(g7) = 105
    c: Coincident(g7,g1)
    c: Block(g3)
    c: Weight(g8) = 1
    c: Equal(g8,g9)
    c: Equal(g8,g10)
    c: InternalAlignment(g8,g11)
    c: InternalAlignment(g9,g11)
    c: InternalAlignment(g10,g11)
    c: InternalAlignment(g12,g11)
    c: InternalAlignment(g13,g11)
    c: Block(g11)
    c: Coincident(g14,g11)
    c: Coincident(g14,g3)
    c: Horizontal(g14)
    c: Block(g15)
    c: Coincident(g16,g11)
    c: Coincident(g16,g15)
    c: Vertical(g16)
    c: Distance(g16) = 14
    c: Coincident(g17,g15)
    c: Block(g18)
    c: Coincident(g19,g18)
    c: Coincident(g20,g7)
    c: Horizontal(g20)
    c: Vertical(g21)
    c: Coincident(g20,g21)
    c: Block(g20)
    c: Block(g21)
    c: Block(g19)
    c: Block(g17)
    c: Distance(g20) = 1.61553
FEATURE [Part::Extrusion] Extrude044
  Base = -> Sketch053
  Dir = (0,0,1)
  DirMode = 2
  FaceMakerClass = Part::FaceMakerBullseye
  LengthFwd = 72
  LengthRev = 0
  Solid = true
  Symmetric = false
FEATURE [Part::Fillet] Fillet036  label="top018"
  Base = -> Extrude044
  Edges = 1 edges r=2: [Edge41]
FEATURE [Part::Fillet] Fillet037  label="bottom011"
  Base = -> Extrude043
  Edges = 1 edges r=2.4: [Edge26]
FEATURE [Sketcher::SketchObject] Sketch054
  FullyConstrained = false
  Placement = pos=(0,0,0) rot=(1,0,0;1.5708rad)
  sketch-geometry (24):
    g0: ArcOfCircle CenterX=-4 CenterY=-10.5 CenterZ=0 NormalX=0 NormalY=0 NormalZ=1 AngleXU=0 Radius=1.5 StartAngle=6e-16 EndAngle=3.14159
    g1: ArcOfCircle CenterX=-34.2 CenterY=-10.5 CenterZ=0 NormalX=0 NormalY=0 NormalZ=1 AngleXU=0 Radius=1.5 StartAngle=0 EndAngle=3.14159
    g2: ArcOfCircle CenterX=-34.2 CenterY=-27.7 CenterZ=0 NormalX=0 NormalY=0 NormalZ=1 AngleXU=0 Radius=1.5 StartAngle=3.14159 EndAngle=6.28319
    g3: ArcOfCircle CenterX=-4 CenterY=-27.7 CenterZ=0 NormalX=0 NormalY=0 NormalZ=1 AngleXU=0 Radius=1.5 StartAngle=3.1416 EndAngle=6.28319
    g4: ArcOfCircle CenterX=-10 CenterY=-4.3 CenterZ=0 NormalX=0 NormalY=0 NormalZ=1 AngleXU=0 Radius=1.5 StartAngle=2e-16 EndAngle=3.14159
    g5: ArcOfCircle CenterX=-16.1 CenterY=-1.8 CenterZ=0 NormalX=0 NormalY=0 NormalZ=1 AngleXU=0 Radius=1.5 StartAngle=5e-16 EndAngle=3.14159
    g6: ArcOfCircle CenterX=-22.1 CenterY=-1.8 CenterZ=0 NormalX=0 NormalY=0 NormalZ=1 AngleXU=0 Radius=1.5 StartAngle=5e-16 EndAngle=3.14159
    g7: ArcOfCircle CenterX=-28.2 CenterY=-4.3 CenterZ=0 NormalX=0 NormalY=0 NormalZ=1 AngleXU=0 Radius=1.5 StartAngle=2e-16 EndAngle=3.14159
    g8: ArcOfCircle CenterX=-10 CenterY=-33.9 CenterZ=0 NormalX=0 NormalY=0 NormalZ=1 AngleXU=0 Radius=1.5 StartAngle=3.14159 EndAngle=6.28319
    g9: ArcOfCircle CenterX=-16.1 CenterY=-36.4 CenterZ=0 NormalX=0 NormalY=0 NormalZ=1 AngleXU=0 Radius=1.5 StartAngle=3.14159 EndAngle=6.28319
    g10: ArcOfCircle CenterX=-22.1 CenterY=-36.4 CenterZ=0 NormalX=0 NormalY=0 NormalZ=1 AngleXU=0 Radius=1.5 StartAngle=3.14159 EndAngle=6.28319
    g11: ArcOfCircle CenterX=-28.2 CenterY=-33.9 CenterZ=0 NormalX=0 NormalY=0 NormalZ=1 AngleXU=0 Radius=1.5 StartAngle=3.14159 EndAngle=6.28319
    g12: LineSegment StartX=-35.7 StartY=-10.5 StartZ=0 EndX=-35.7 EndY=-27.7 EndZ=0
    g13: LineSegment StartX=-32.7 StartY=-10.5 StartZ=0 EndX=-32.7 EndY=-27.7 EndZ=0
    g14: LineSegment StartX=-29.7 StartY=-33.9 StartZ=0 EndX=-29.7 EndY=-4.3 EndZ=0
    g15: LineSegment StartX=-26.7 StartY=-33.9 StartZ=0 EndX=-26.7 EndY=-4.3 EndZ=0
    g16: LineSegment StartX=-2.5 StartY=-10.5 StartZ=0 EndX=-2.5 EndY=-27.7 EndZ=0
    g17: LineSegment StartX=-8.5 StartY=-4.3 StartZ=0 EndX=-8.5 EndY=-33.9 EndZ=0
    g18: LineSegment StartX=-5.5 StartY=-10.5 StartZ=0 EndX=-5.5 EndY=-27.7 EndZ=0
    g19: LineSegment StartX=-11.5 StartY=-4.3 StartZ=0 EndX=-11.5 EndY=-33.9 EndZ=0
    g20: LineSegment StartX=-14.6 StartY=-1.8 StartZ=0 EndX=-14.6 EndY=-36.4 EndZ=0
    g21: LineSegment StartX=-17.6 StartY=-1.8 StartZ=0 EndX=-17.6 EndY=-36.4 EndZ=0
    g22: LineSegment StartX=-20.6 StartY=-36.4 StartZ=0 EndX=-20.6 EndY=-1.8 EndZ=0
    g23: LineSegment StartX=-23.6 StartY=-1.8 StartZ=0 EndX=-23.6 EndY=-36.4 EndZ=0
  constraints (48):
    c: Block(g0)
    c: Block(g1)
    c: Block(g2)
    c: Block(g3)
    c: Block(g4)
    c: Block(g5)
    c: Block(g6)
    c: Block(g7)
    c: Block(g8)
    c: Block(g9)
    c: Block(g10)
    c: Block(g11)
    c: Coincident(g12,g1)
    c: Coincident(g12,g2)
    c: Vertical(g12)
    c: Coincident(g13,g1)
    c: Coincident(g13,g2)
    c: Vertical(g13)
    c: Coincident(g14,g11)
    c: Coincident(g14,g7)
    c: Vertical(g14)
    c: Coincident(g15,g11)
    c: Coincident(g15,g7)
    c: Vertical(g15)
    c: Coincident(g16,g0)
    c: Coincident(g16,g3)
    c: Vertical(g16)
    c: Coincident(g17,g4)
    c: Coincident(g17,g8)
    c: Vertical(g17)
    c: Coincident(g18,g0)
    c: Coincident(g18,g3)
    c: Vertical(g18)
    c: Coincident(g19,g4)
    c: Coincident(g19,g8)
    c: Vertical(g19)
    c: Coincident(g20,g5)
    c: Coincident(g20,g9)
    c: Vertical(g20)
    c: Coincident(g21,g5)
    c: Coincident(g21,g9)
    c: Vertical(g21)
    c: Coincident(g22,g10)
    c: Coincident(g22,g6)
    c: Vertical(g22)
    c: Coincident(g23,g6)
    c: Coincident(g23,g10)
    c: Vertical(g23)
FEATURE [Part::Extrusion] Extrude045  label="removeToCreateFanGrillHoles003"
  Base = -> Sketch054
  Dir = (0,-1,6e-16)
  DirMode = 2
  FaceMakerClass = Part::FaceMakerBullseye
  LengthFwd = 10
  LengthRev = 0
  Placement = pos=(65.4,44,54.82) rot=(0,0,1;0rad)
  Solid = true
  Symmetric = false
FEATURE [Part::Feature] Face105 .. Face108  x4 (patterned run collapsed; names and placements below)
  shape: bbox 3.5 x 17.8 x 2e-07 mm, 1 faces, 0 solids (baked)
FEATURE [Part::Revolution] Revolve113  label="removeToCreateScrewAndThreadedInsertHole041"
  Angle = 360
  Axis = (0,1,0)
  Base = (0,0,0)
  FaceMakerClass = Part::FaceMakerBullseye
  Placement = pos=(62.3,30.3,19.7) rot=(0,0,1;0rad)
  Solid = false
  Source = -> Face105
  Symmetric = false
FEATURE [Part::Revolution] Revolve114  label="removeToCreateScrewAndThreadedInsertHole042"
  Angle = 360
  Axis = (0,1,0)
  Base = (0,0,0)
  FaceMakerClass = Part::FaceMakerBullseye
  Placement = pos=(62.3,30.3,51.7) rot=(0,0,1;0rad)
  Solid = false
  Source = -> Face106
  Symmetric = false
FEATURE [Part::Revolution] Revolve115  label="removeToCreateScrewAndThreadedInsertHole043"
  Angle = 360
  Axis = (0,1,0)
  Base = (0,0,0)
  FaceMakerClass = Part::FaceMakerBullseye
  Placement = pos=(30.3,30.3,19.7) rot=(0,0,1;0rad)
  Solid = false
  Source = -> Face107
  Symmetric = false
FEATURE [Part::Revolution] Revolve116  label="removeToCreateScrewAndThreadedInsertHole044"
  Angle = 360
  Axis = (0,1,0)
  Base = (0,0,0)
  FaceMakerClass = Part::FaceMakerBullseye
  Placement = pos=(30.3,30.3,51.7) rot=(0,0,1;0rad)
  Solid = false
  Source = -> Face108
  Symmetric = false
FEATURE [Part::MultiFuse] Fusion083  label="createThreadedInsertHolesForFan004"
  Shapes = -> [Revolve113,Revolve114,Revolve115,Revolve116]
FEATURE [Part::Box] Box024  label="removeToCreteHoleForPlugHousing026"
  AttacherType = Attacher::AttachEngine3D
  Height = 28.6
  Length = 10
  Placement = pos=(-2,0,21.7) rot=(0,0,1;0rad)
  Width = 19
FEATURE [Part::Cylinder] Cylinder038  label="removeToCreteHoleForPlugHousing027"
  Angle = 360
  AttacherType = Attacher::AttachEngine3D
  Height = 20
  Placement = pos=(-2,19,36) rot=(0,1,0;1.5708rad)
  Radius = 14.3
FEATURE [Part::MultiFuse] Fusion084  label="removeToCreteHoleForPlugHousing028"
  Shapes = -> [Box024,Cylinder038]
FEATURE [Part::Cylinder] Cylinder039
  Angle = 360
  AttacherType = Attacher::AttachEngine3D
  Height = 20
  Placement = pos=(0,0,36.15) rot=(0,0,1;0rad)
  Radius = 14.3
FEATURE [Part::Cylinder] Cylinder040
  Angle = 360
  AttacherType = Attacher::AttachEngine3D
  Height = 10
  Placement = pos=(0,0,36.15) rot=(0,0,1;0rad)
  Radius = 4
FEATURE [Part::Box] Box025  label="removeToCreteHoleForPlugHousing030"
  AttacherType = Attacher::AttachEngine3D
  Height = 28.6
  Length = 20
  Placement = pos=(106.15,0,21.7) rot=(0,0,1;0rad)
  Width = 19
FEATURE [Part::MultiFuse] Fusion086  label="removeToCreteHoleForPlugHousing031"
  Placement = pos=(70,19,36) rot=(0,1,0;1.5708rad)
  Shapes = -> [Cylinder039,Cylinder040]
FEATURE [Part::MultiFuse] Fusion085  label="removeToCreteHoleForPlugHousing029"
  Shapes = -> [Box025,Fusion086]
FEATURE [Sketcher::SketchObject] Sketch055
  FullyConstrained = true
  Placement = pos=(117,19,0) rot=(0.57735,0.57735,0.57735;2.0944rad)
  sketch-geometry (48):
    g0: LineSegment StartX=-49.19 StartY=69.25 StartZ=0 EndX=-49.19 EndY=66.25 EndZ=0
    g1: LineSegment StartX=-49.19 StartY=63.5 StartZ=0 EndX=-49.19 EndY=60.5 EndZ=0
    g2: LineSegment StartX=-49.19 StartY=57.75 StartZ=0 EndX=-49.19 EndY=54.75 EndZ=0
    g3: LineSegment StartX=-49.19 StartY=52 StartZ=0 EndX=-49.19 EndY=49 EndZ=0
    g4: LineSegment StartX=-49.19 StartY=46.25 StartZ=0 EndX=-49.19 EndY=43.25 EndZ=0
    g5: LineSegment StartX=-49.19 StartY=40.5 StartZ=0 EndX=-49.19 EndY=37.5 EndZ=0
    g6: LineSegment StartX=-49.19 StartY=34.5 StartZ=0 EndX=-49.19 EndY=31.5 EndZ=0
    g7: LineSegment StartX=-49.19 StartY=28.75 StartZ=0 EndX=-49.19 EndY=25.75 EndZ=0
    g8: LineSegment StartX=-49.19 StartY=23 StartZ=0 EndX=-49.19 EndY=20 EndZ=0
    g9: LineSegment StartX=-49.19 StartY=17.25 StartZ=0 EndX=-49.19 EndY=14.25 EndZ=0
    g10: LineSegment StartX=-49.19 StartY=11.5 StartZ=0 EndX=-49.19 EndY=8.5 EndZ=0
    g11: LineSegment StartX=-49.19 StartY=5.75 StartZ=0 EndX=-49.19 EndY=2.75 EndZ=0
    g12: ArcOfCircle CenterX=-1.5 CenterY=67.75 CenterZ=0 NormalX=0 NormalY=0 NormalZ=1 AngleXU=0 Radius=1.5 StartAngle=4.71239 EndAngle=7.85398
    g13: ArcOfCircle CenterX=-1.5 CenterY=62 CenterZ=0 NormalX=0 NormalY=0 NormalZ=1 AngleXU=0 Radius=1.5 StartAngle=4.71239 EndAngle=7.85398
    g14: ArcOfCircle CenterX=-1.5 CenterY=56.25 CenterZ=0 NormalX=0 NormalY=0 NormalZ=1 AngleXU=0 Radius=1.5 StartAngle=4.71239 EndAngle=7.85398
    g15: ArcOfCircle CenterX=-11.49 CenterY=50.5 CenterZ=0 NormalX=0 NormalY=0 NormalZ=1 AngleXU=0 Radius=1.5 StartAngle=4.71239 EndAngle=7.85398
    g16: ArcOfCircle CenterX=-16.28 CenterY=44.75 CenterZ=0 NormalX=0 NormalY=0 NormalZ=1 AngleXU=0 Radius=1.5 StartAngle=4.71239 EndAngle=7.85398
    g17: ArcOfCircle CenterX=-18.2337 CenterY=39 CenterZ=0 NormalX=0 NormalY=0 NormalZ=1 AngleXU=0 Radius=1.5 StartAngle=4.71485 EndAngle=7.85398
    g18: ArcOfCircle CenterX=-16.2837 CenterY=27.25 CenterZ=0 NormalX=0 NormalY=0 NormalZ=1 AngleXU=0 Radius=1.5 StartAngle=4.71485 EndAngle=7.85398
    g19: ArcOfCircle CenterX=-18.2337 CenterY=33 CenterZ=0 NormalX=0 NormalY=0 NormalZ=1 AngleXU=0 Radius=1.5 StartAngle=4.71485 EndAngle=7.85398
    g20: ArcOfCircle CenterX=-11.49 CenterY=21.5 CenterZ=0 NormalX=0 NormalY=0 NormalZ=1 AngleXU=0 Radius=1.5 StartAngle=4.71239 EndAngle=7.85398
    g21: ArcOfCircle CenterX=-1.5 CenterY=4.25 CenterZ=0 NormalX=0 NormalY=0 NormalZ=1 AngleXU=0 Radius=1.5 StartAngle=4.71239 EndAngle=7.85398
    g22: ArcOfCircle CenterX=-1.5 CenterY=10 CenterZ=0 NormalX=0 NormalY=0 NormalZ=1 AngleXU=0 Radius=1.5 StartAngle=4.71239 EndAngle=7.85398
    g23: ArcOfCircle CenterX=-1.5 CenterY=15.75 CenterZ=0 NormalX=0 NormalY=0 NormalZ=1 AngleXU=0 Radius=1.5 StartAngle=4.71239 EndAngle=7.85398
    g24: LineSegment StartX=-49.19 StartY=69.25 StartZ=0 EndX=-1.5 EndY=69.25 EndZ=0
    g25: LineSegment StartX=-49.19 StartY=66.25 StartZ=0 EndX=-1.5 EndY=66.25 EndZ=0
    g26: LineSegment StartX=-49.19 StartY=63.5 StartZ=0 EndX=-1.5 EndY=63.5 EndZ=0
    g27: LineSegment StartX=-49.19 StartY=60.5 StartZ=0 EndX=-1.5 EndY=60.5 EndZ=0
    g28: LineSegment StartX=-49.19 StartY=57.75 StartZ=0 EndX=-1.5 EndY=57.75 EndZ=0
    g29: LineSegment StartX=-49.19 StartY=54.75 StartZ=0 EndX=-1.5 EndY=54.75 EndZ=0
    g30: LineSegment StartX=-49.19 StartY=52 StartZ=0 EndX=-11.49 EndY=52 EndZ=0
    g31: LineSegment StartX=-49.19 StartY=49 StartZ=0 EndX=-11.49 EndY=49 EndZ=0
    g32: LineSegment StartX=-49.19 StartY=46.25 StartZ=0 EndX=-16.28 EndY=46.25 EndZ=0
    g33: LineSegment StartX=-49.19 StartY=43.25 StartZ=0 EndX=-16.28 EndY=43.25 EndZ=0
    g34: LineSegment StartX=-49.19 StartY=40.5 StartZ=0 EndX=-18.2337 EndY=40.5 EndZ=0
    g35: LineSegment StartX=-49.19 StartY=37.5 StartZ=0 EndX=-18.23 EndY=37.5 EndZ=0
    g36: LineSegment StartX=-49.19 StartY=34.5 StartZ=0 EndX=-18.2337 EndY=34.5 EndZ=0
    g37: LineSegment StartX=-49.19 StartY=31.5 StartZ=0 EndX=-18.23 EndY=31.5 EndZ=0
    g38: LineSegment StartX=-49.19 StartY=28.75 StartZ=0 EndX=-16.2837 EndY=28.75 EndZ=0
    g39: LineSegment StartX=-49.19 StartY=25.75 StartZ=0 EndX=-16.28 EndY=25.75 EndZ=0
    g40: LineSegment StartX=-49.19 StartY=23 StartZ=0 EndX=-11.49 EndY=23 EndZ=0
    g41: LineSegment StartX=-49.19 StartY=20 StartZ=0 EndX=-11.49 EndY=20 EndZ=0
    g42: LineSegment StartX=-49.19 StartY=17.25 StartZ=0 EndX=-1.5 EndY=17.25 EndZ=0
    g43: LineSegment StartX=-49.19 StartY=14.25 StartZ=0 EndX=-1.5 EndY=14.25 EndZ=0
    g44: LineSegment StartX=-49.19 StartY=11.5 StartZ=0 EndX=-1.5 EndY=11.5 EndZ=0
    g45: LineSegment StartX=-49.19 StartY=8.5 StartZ=0 EndX=-1.5 EndY=8.5 EndZ=0
    g46: LineSegment StartX=-49.19 StartY=5.75 StartZ=0 EndX=-1.5 EndY=5.75 EndZ=0
    g47: LineSegment StartX=-49.19 StartY=2.75 StartZ=0 EndX=-1.5 EndY=2.75 EndZ=0
  constraints (120):
    c: Vertical(g0)
    c: Distance(g0) = 3
    c: Block(g0)
    c: Vertical(g1)
    c: Distance(g1) = 3
    c: Vertical(g2)
    c: Equal(g0,g2) = 3
    c: Block(g2)
    c: Vertical(g3)
    c: Equal(g1,g3) = 3
    c: Vertical(g4)
    c: Equal(g0,g4) = 3
    c: Block(g4)
    c: Vertical(g5)
    c: Equal(g1,g5) = 3
    c: Vertical(g6)
    c: Equal(g0,g6) = 3
    c: Block(g6)
    c: Vertical(g7)
    c: Equal(g1,g7) = 3
    c: Vertical(g8)
    c: Equal(g0,g8) = 3
    c: Block(g8)
    c: Vertical(g9)
    c: Equal(g1,g9) = 3
    c: Vertical(g10)
    c: Equal(g0,g10) = 3
    c: Block(g10)
    c: Vertical(g11)
    c: Equal(g1,g11) = 3
    c: Block(g12)
    c: Block(g13)
    c: Block(g14)
    c: Block(g15)
    c: Block(g16)
    c: Block(g17)
    c: Block(g18)
    c: Block(g19)
    c: Block(g20)
    c: Block(g21)
    c: Block(g22)
    c: Block(g23)
    c: Block(g11)
    c: Block(g9)
    c: Block(g7)
    c: Block(g5)
    c: Block(g3)
    c: Block(g1)
    c: Coincident(g24,g0)
    c: Coincident(g24,g12)
    c: Horizontal(g24)
    c: Coincident(g25,g0)
    c: Coincident(g25,g12)
    c: Horizontal(g25)
    c: Coincident(g26,g1)
    c: Coincident(g26,g13)
    c: Horizontal(g26)
    c: Coincident(g27,g1)
    c: Coincident(g27,g13)
    c: Horizontal(g27)
    c: Coincident(g28,g2)
    c: Coincident(g28,g14)
    c: Horizontal(g28)
    c: Coincident(g29,g2)
    c: Coincident(g29,g14)
    c: Horizontal(g29)
    c: Coincident(g30,g3)
    c: Coincident(g30,g15)
    c: Horizontal(g30)
    c: Coincident(g31,g3)
    c: Coincident(g31,g15)
    c: Horizontal(g31)
    c: Coincident(g32,g4)
    c: Coincident(g32,g16)
    c: Horizontal(g32)
    c: Coincident(g33,g4)
    c: Coincident(g33,g16)
    c: Horizontal(g33)
    c: Coincident(g34,g5)
    c: Coincident(g34,g17)
    c: Horizontal(g34)
    c: Coincident(g35,g5)
    c: Coincident(g35,g17)
    c: Horizontal(g35)
    c: Coincident(g36,g6)
    c: Coincident(g36,g19)
    c: Horizontal(g36)
    c: Coincident(g37,g6)
    c: Coincident(g37,g19)
    c: Horizontal(g37)
    c: Coincident(g38,g7)
    c: Coincident(g38,g18)
    c: Horizontal(g38)
    c: Coincident(g39,g7)
    c: Coincident(g39,g18)
    c: Horizontal(g39)
    c: Coincident(g40,g8)
    c: Coincident(g40,g20)
    c: Horizontal(g40)
    c: Coincident(g41,g8)
    c: Coincident(g41,g20)
    c: Horizontal(g41)
    c: Coincident(g42,g9)
    c: Coincident(g42,g23)
    c: Horizontal(g42)
    c: Coincident(g43,g9)
    c: Coincident(g43,g23)
    c: Horizontal(g43)
    c: Coincident(g44,g10)
    c: Coincident(g44,g22)
    c: Horizontal(g44)
    c: Coincident(g45,g10)
    c: Coincident(g45,g22)
    c: Horizontal(g45)
    c: Coincident(g46,g11)
    c: Coincident(g46,g21)
    c: Horizontal(g46)
    c: Coincident(g47,g11)
    c: Coincident(g47,g21)
    c: Horizontal(g47)
FEATURE [Part::Extrusion] Extrude046
  Base = -> Sketch055
  Dir = (1,0,0)
  DirMode = 2
  FaceMakerClass = Part::FaceMakerBullseye
  LengthFwd = 23
  LengthRev = 0
  Placement = pos=(-19,0,0) rot=(0,0,1;0rad)
  Solid = true
  Symmetric = false
FEATURE [Part::Fillet] Fillet038  label="removeToCreateVentalationHoles001"
  Base = -> Extrude046
  Edges = <same value as first occurrence — deduplicated (x4 in doc)>
  Placement = pos=(7,0,0) rot=(0,0,1;0rad)
FEATURE [Sketcher::SketchObject] Sketch056  label="topSketch014"
  FullyConstrained = true
  sketch-geometry (22):
    g0: LineSegment StartX=5.21097e-06 StartY=3 StartZ=0 EndX=5.21097e-06 EndY=19 EndZ=0
    g1: ArcOfCircle CenterX=19 CenterY=19 CenterZ=0 NormalX=0 NormalY=0 NormalZ=1 AngleXU=0 Radius=19 StartAngle=1.5708 EndAngle=3.14159
    g2: ArcOfCircle CenterX=19 CenterY=19 CenterZ=0 NormalX=0 NormalY=0 NormalZ=1 AngleXU=0 Radius=16 StartAngle=1.5708 EndAngle=3.14159
    g3: LineSegment StartX=114 StartY=35 StartZ=0 EndX=19 EndY=35 EndZ=0
    g4: LineSegment StartX=5.21097e-06 StartY=3 StartZ=0 EndX=5.21097e-06 EndY=0 EndZ=0
    g5: LineSegment StartX=3 StartY=0 StartZ=0 EndX=5.21097e-06 EndY=0 EndZ=0
    g6: LineSegment StartX=3 StartY=19 StartZ=0 EndX=3 EndY=0 EndZ=0
    g7: LineSegment StartX=19 StartY=38 StartZ=0 EndX=124 EndY=38 EndZ=0
    g8: Circle CenterX=119 CenterY=35 CenterZ=0 NormalX=0 NormalY=0 NormalZ=1 AngleXU=0 Radius=1
    g9: Circle CenterX=121 CenterY=35 CenterZ=0 NormalX=0 NormalY=0 NormalZ=1 AngleXU=0 Radius=1
    g10: Circle CenterX=121 CenterY=33 CenterZ=0 NormalX=0 NormalY=0 NormalZ=1 AngleXU=0 Radius=1
    g11: BSplineCurve PolesCount=3 KnotsCount=2 Degree=2 IsPeriodic=0
    g12: GeomPoint X=119 Y=35 Z=0
    g13: GeomPoint X=121 Y=33 Z=0
    g14: LineSegment StartX=119 StartY=35 StartZ=0 EndX=114 EndY=35 EndZ=0
    g15: ArcOfCircle CenterX=105 CenterY=19 CenterZ=0 NormalX=0 NormalY=0 NormalZ=1 AngleXU=0 Radius=16 StartAngle=5.60905 EndAngle=6.28319
    g16: LineSegment StartX=121 StartY=33 StartZ=0 EndX=121 EndY=19 EndZ=0
    g17: LineSegment StartX=117.5 StartY=9.01251 StartZ=0 EndX=121.163 EndY=9.0125 EndZ=0
    g18: ArcOfCircle CenterX=105 CenterY=19 CenterZ=0 NormalX=0 NormalY=0 NormalZ=1 AngleXU=0 Radius=20.6155 StartAngle=5.7297 EndAngle=6.28319
    g19: LineSegment StartX=121.163 StartY=9.0125 StartZ=0 EndX=122.538 EndY=8.16329 EndZ=0
    g20: LineSegment StartX=124 StartY=38 StartZ=0 EndX=125.616 EndY=38 EndZ=0
    g21: LineSegment StartX=125.616 StartY=19 StartZ=0 EndX=125.616 EndY=38 EndZ=0
  constraints (49):
    c: Vertical(g0)
    c: Block(g0)
    c: Coincident(g1,g0)
    c: Block(g1)
    c: Coincident(g2,g1)
    c: Block(g2)
    c: Coincident(g3,g2)
    c: Horizontal(g3)
    c: Tangent(g3,g2)
    c: Coincident(g4,g0)
    c: Distance(g4) = 3
    c: Vertical(g4)
    c: Coincident(g5,g4)
    c: Horizontal(g5)
    c: Coincident(g6,g2)
    c: Coincident(g6,g5)
    c: Vertical(g6)
    c: Horizontal(g7)
    c: Distance(g7) = 105
    c: Coincident(g7,g1)
    c: Block(g3)
    c: Weight(g8) = 1
    c: Equal(g8,g9)
    c: Equal(g8,g10)
    c: InternalAlignment(g8,g11)
    c: InternalAlignment(g9,g11)
    c: InternalAlignment(g10,g11)
    c: InternalAlignment(g12,g11)
    c: InternalAlignment(g13,g11)
    c: Block(g11)
    c: Coincident(g14,g11)
    c: Coincident(g14,g3)
    c: Horizontal(g14)
    c: Block(g15)
    c: Coincident(g16,g11)
    c: Coincident(g16,g15)
    c: Vertical(g16)
    c: Distance(g16) = 14
    c: Coincident(g17,g15)
    c: Block(g18)
    c: Coincident(g19,g18)
    c: Coincident(g20,g7)
    c: Horizontal(g20)
    c: Vertical(g21)
    c: Coincident(g20,g21)
    c: Block(g20)
    c: Block(g21)
    c: Block(g19)
    c: Block(g17)
FEATURE [Part::Box] Box026  label="removeToCreteHoleForPlugHousing032"
  AttacherType = Attacher::AttachEngine3D
  Height = 28.6
  Length = 10
  Placement = pos=(-2,0,21.7) rot=(0,0,1;0rad)
  Width = 19
FEATURE [Part::Feature] Face109 .. Face112  x4 (patterned run collapsed; names and placements below)
  shape: bbox 3.5 x 17.8 x 2e-07 mm, 1 faces, 0 solids (baked)
FEATURE [Part::Revolution] Revolve117  label="removeToCreateScrewAndThreadedInsertHole045"
  Angle = 360
  Axis = (0,1,0)
  Base = (0,0,0)
  FaceMakerClass = Part::FaceMakerBullseye
  Placement = pos=(62.3,30.3,19.7) rot=(0,0,1;0rad)
  Solid = false
  Source = -> Face109
  Symmetric = false
FEATURE [Part::Revolution] Revolve118  label="removeToCreateScrewAndThreadedInsertHole046"
  Angle = 360
  Axis = (0,1,0)
  Base = (0,0,0)
  FaceMakerClass = Part::FaceMakerBullseye
  Placement = pos=(62.3,30.3,51.7) rot=(0,0,1;0rad)
  Solid = false
  Source = -> Face110
  Symmetric = false
FEATURE [Part::Revolution] Revolve119  label="removeToCreateScrewAndThreadedInsertHole047"
  Angle = 360
  Axis = (0,1,0)
  Base = (0,0,0)
  FaceMakerClass = Part::FaceMakerBullseye
  Placement = pos=(30.3,30.3,19.7) rot=(0,0,1;0rad)
  Solid = false
  Source = -> Face111
  Symmetric = false
FEATURE [Part::Revolution] Revolve120  label="removeToCreateScrewAndThreadedInsertHole048"
  Angle = 360
  Axis = (0,1,0)
  Base = (0,0,0)
  FaceMakerClass = Part::FaceMakerBullseye
  Placement = pos=(30.3,30.3,51.7) rot=(0,0,1;0rad)
  Solid = false
  Source = -> Face112
  Symmetric = false
FEATURE [Part::MultiFuse] Fusion087  label="createThreadedInsertHolesForFan005"
  Shapes = -> [Revolve117,Revolve118,Revolve119,Revolve120]
FEATURE [Part::Extrusion] Extrude047
  Base = -> Sketch056
  Dir = (0,0,1)
  DirMode = 2
  FaceMakerClass = Part::FaceMakerBullseye
  LengthFwd = 72
  LengthRev = 0
  Solid = true
  Symmetric = false
FEATURE [Part::Fillet] Fillet039  label="top019"
  Base = -> Extrude047
  Edges = 1 edges r=2: [Edge35]
FEATURE [Sketcher::SketchObject] Sketch057
  FullyConstrained = false
  Placement = pos=(0,0,0) rot=(1,0,0;1.5708rad)
  sketch-geometry (24):
    g0: ArcOfCircle CenterX=-4 CenterY=-10.5 CenterZ=0 NormalX=0 NormalY=0 NormalZ=1 AngleXU=0 Radius=1.5 StartAngle=6e-16 EndAngle=3.14159
    g1: ArcOfCircle CenterX=-34.2 CenterY=-10.5 CenterZ=0 NormalX=0 NormalY=0 NormalZ=1 AngleXU=0 Radius=1.5 StartAngle=0 EndAngle=3.14159
    g2: ArcOfCircle CenterX=-34.2 CenterY=-27.7 CenterZ=0 NormalX=0 NormalY=0 NormalZ=1 AngleXU=0 Radius=1.5 StartAngle=3.14159 EndAngle=6.28319
    g3: ArcOfCircle CenterX=-4 CenterY=-27.7 CenterZ=0 NormalX=0 NormalY=0 NormalZ=1 AngleXU=0 Radius=1.5 StartAngle=3.1416 EndAngle=6.28319
    g4: ArcOfCircle CenterX=-10 CenterY=-4.3 CenterZ=0 NormalX=0 NormalY=0 NormalZ=1 AngleXU=0 Radius=1.5 StartAngle=2e-16 EndAngle=3.14159
    g5: ArcOfCircle CenterX=-16.1 CenterY=-1.8 CenterZ=0 NormalX=0 NormalY=0 NormalZ=1 AngleXU=0 Radius=1.5 StartAngle=5e-16 EndAngle=3.14159
    g6: ArcOfCircle CenterX=-22.1 CenterY=-1.8 CenterZ=0 NormalX=0 NormalY=0 NormalZ=1 AngleXU=0 Radius=1.5 StartAngle=5e-16 EndAngle=3.14159
    g7: ArcOfCircle CenterX=-28.2 CenterY=-4.3 CenterZ=0 NormalX=0 NormalY=0 NormalZ=1 AngleXU=0 Radius=1.5 StartAngle=2e-16 EndAngle=3.14159
    g8: ArcOfCircle CenterX=-10 CenterY=-33.9 CenterZ=0 NormalX=0 NormalY=0 NormalZ=1 AngleXU=0 Radius=1.5 StartAngle=3.14159 EndAngle=6.28319
    g9: ArcOfCircle CenterX=-16.1 CenterY=-36.4 CenterZ=0 NormalX=0 NormalY=0 NormalZ=1 AngleXU=0 Radius=1.5 StartAngle=3.14159 EndAngle=6.28319
    g10: ArcOfCircle CenterX=-22.1 CenterY=-36.4 CenterZ=0 NormalX=0 NormalY=0 NormalZ=1 AngleXU=0 Radius=1.5 StartAngle=3.14159 EndAngle=6.28319
    g11: ArcOfCircle CenterX=-28.2 CenterY=-33.9 CenterZ=0 NormalX=0 NormalY=0 NormalZ=1 AngleXU=0 Radius=1.5 StartAngle=3.14159 EndAngle=6.28319
    g12: LineSegment StartX=-35.7 StartY=-10.5 StartZ=0 EndX=-35.7 EndY=-27.7 EndZ=0
    g13: LineSegment StartX=-32.7 StartY=-10.5 StartZ=0 EndX=-32.7 EndY=-27.7 EndZ=0
    g14: LineSegment StartX=-29.7 StartY=-33.9 StartZ=0 EndX=-29.7 EndY=-4.3 EndZ=0
    g15: LineSegment StartX=-26.7 StartY=-33.9 StartZ=0 EndX=-26.7 EndY=-4.3 EndZ=0
    g16: LineSegment StartX=-2.5 StartY=-10.5 StartZ=0 EndX=-2.5 EndY=-27.7 EndZ=0
    g17: LineSegment StartX=-8.5 StartY=-4.3 StartZ=0 EndX=-8.5 EndY=-33.9 EndZ=0
    g18: LineSegment StartX=-5.5 StartY=-10.5 StartZ=0 EndX=-5.5 EndY=-27.7 EndZ=0
    g19: LineSegment StartX=-11.5 StartY=-4.3 StartZ=0 EndX=-11.5 EndY=-33.9 EndZ=0
    g20: LineSegment StartX=-14.6 StartY=-1.8 StartZ=0 EndX=-14.6 EndY=-36.4 EndZ=0
    g21: LineSegment StartX=-17.6 StartY=-1.8 StartZ=0 EndX=-17.6 EndY=-36.4 EndZ=0
    g22: LineSegment StartX=-20.6 StartY=-36.4 StartZ=0 EndX=-20.6 EndY=-1.8 EndZ=0
    g23: LineSegment StartX=-23.6 StartY=-1.8 StartZ=0 EndX=-23.6 EndY=-36.4 EndZ=0
  constraints (48):
    c: Block(g0)
    c: Block(g1)
    c: Block(g2)
    c: Block(g3)
    c: Block(g4)
    c: Block(g5)
    c: Block(g6)
    c: Block(g7)
    c: Block(g8)
    c: Block(g9)
    c: Block(g10)
    c: Block(g11)
    c: Coincident(g12,g1)
    c: Coincident(g12,g2)
    c: Vertical(g12)
    c: Coincident(g13,g1)
    c: Coincident(g13,g2)
    c: Vertical(g13)
    c: Coincident(g14,g11)
    c: Coincident(g14,g7)
    c: Vertical(g14)
    c: Coincident(g15,g11)
    c: Coincident(g15,g7)
    c: Vertical(g15)
    c: Coincident(g16,g0)
    c: Coincident(g16,g3)
    c: Vertical(g16)
    c: Coincident(g17,g4)
    c: Coincident(g17,g8)
    c: Vertical(g17)
    c: Coincident(g18,g0)
    c: Coincident(g18,g3)
    c: Vertical(g18)
    c: Coincident(g19,g4)
    c: Coincident(g19,g8)
    c: Vertical(g19)
    c: Coincident(g20,g5)
    c: Coincident(g20,g9)
    c: Vertical(g20)
    c: Coincident(g21,g5)
    c: Coincident(g21,g9)
    c: Vertical(g21)
    c: Coincident(g22,g10)
    c: Coincident(g22,g6)
    c: Vertical(g22)
    c: Coincident(g23,g6)
    c: Coincident(g23,g10)
    c: Vertical(g23)
FEATURE [Part::Extrusion] Extrude048  label="removeToCreateFanGrillHoles004"
  Base = -> Sketch057
  Dir = (0,-1,6e-16)
  DirMode = 2
  FaceMakerClass = Part::FaceMakerBullseye
  LengthFwd = 10
  LengthRev = 0
  Placement = pos=(65.4,44,54.82) rot=(0,0,1;0rad)
  Solid = true
  Symmetric = false
FEATURE [Part::Cut] Cut040  label="top021"
  Base = -> Fillet039
  Tool = -> Extrude048
FEATURE [Part::Cylinder] Cylinder041  label="removeToCreteHoleForPlugHousing034"
  Angle = 360
  AttacherType = Attacher::AttachEngine3D
  Height = 20
  Placement = pos=(-2,19,36) rot=(0,1,0;1.5708rad)
  Radius = 14.3
FEATURE [Part::MultiFuse] Fusion089  label="removeToCreteHoleForPlugHousing035"
  Shapes = -> [Box026,Cylinder041]
FEATURE [Part::Cylinder] Cylinder042
  Angle = 360
  AttacherType = Attacher::AttachEngine3D
  Height = 20
  Placement = pos=(0,0,36.15) rot=(0,0,1;0rad)
  Radius = 14.3
FEATURE [Part::Cylinder] Cylinder043
  Angle = 360
  AttacherType = Attacher::AttachEngine3D
  Height = 10
  Placement = pos=(0,0,36.15) rot=(0,0,1;0rad)
  Radius = 4
FEATURE [Part::Box] Box027  label="removeToCreteHoleForPlugHousing036"
  AttacherType = Attacher::AttachEngine3D
  Height = 28.6
  Length = 20
  Placement = pos=(106.15,0,21.7) rot=(0,0,1;0rad)
  Width = 19
FEATURE [Part::Cut] Cut041  label="top022"
  Base = -> Cut040
  Tool = -> Fusion087
FEATURE [Part::Cut] Cut039  label="top020"
  Base = -> Cut041
  Tool = -> Fusion089
FEATURE [Part::MultiFuse] Fusion090  label="removeToCreteHoleForPlugHousing037"
  Placement = pos=(70,19,36) rot=(0,1,0;1.5708rad)
  Shapes = -> [Cylinder042,Cylinder043]
FEATURE [Part::MultiFuse] Fusion088  label="removeToCreteHoleForPlugHousing033"
  Shapes = -> [Box027,Fusion090]
FEATURE [Part::Cut] Cut042  label="removeToCreteHoleForPlugHousing038"
  Base = -> Cut039
  Tool = -> Fusion088
FEATURE [Part::MultiFuse] Fusion091  label="removeFromTop"
  Shapes = -> [Fillet038,Fusion085,Fusion084,Fusion083,Extrude045]
FEATURE [Part::Cut] Cut043  label="removeToCreteHoleForPlugHousing039"
  Base = -> Fillet036
  Tool = -> Fusion091
FEATURE [Part::MultiFuse] Fusion092  label="caseScrewPillarBracket016"
  Shapes = -> [Extrude030,Extrude031,Extrude032,Extrude033,Extrude034,Extrude035,Extrude036,Extrude037,Box013,Box014]
FEATURE [Sketcher::SketchObject] Sketch058  label="topSketch015"
  FullyConstrained = true
  sketch-geometry (20):
    g0: LineSegment StartX=5.21097e-06 StartY=3 StartZ=0 EndX=5.21097e-06 EndY=19 EndZ=0
    g1: ArcOfCircle CenterX=19 CenterY=19 CenterZ=0 NormalX=0 NormalY=0 NormalZ=1 AngleXU=0 Radius=19 StartAngle=1.5708 EndAngle=3.14159
    g2: ArcOfCircle CenterX=19 CenterY=19 CenterZ=0 NormalX=0 NormalY=0 NormalZ=1 AngleXU=0 Radius=16 StartAngle=1.5708 EndAngle=3.14159
    g3: LineSegment StartX=114 StartY=35 StartZ=0 EndX=19 EndY=35 EndZ=0
    g4: LineSegment StartX=5.21097e-06 StartY=3 StartZ=0 EndX=5.21097e-06 EndY=0 EndZ=0
    g5: LineSegment StartX=3 StartY=0 StartZ=0 EndX=5.21097e-06 EndY=0 EndZ=0
    g6: LineSegment StartX=3 StartY=19 StartZ=0 EndX=3 EndY=0 EndZ=0
    g7: LineSegment StartX=19 StartY=38 StartZ=0 EndX=124 EndY=38 EndZ=0
    g8: Circle CenterX=119 CenterY=35 CenterZ=0 NormalX=0 NormalY=0 NormalZ=1 AngleXU=0 Radius=1
    g9: Circle CenterX=121 CenterY=35 CenterZ=0 NormalX=0 NormalY=0 NormalZ=1 AngleXU=0 Radius=1
    g10: Circle CenterX=121 CenterY=33 CenterZ=0 NormalX=0 NormalY=0 NormalZ=1 AngleXU=0 Radius=1
    g11: BSplineCurve PolesCount=3 KnotsCount=2 Degree=2 IsPeriodic=0
    g12: GeomPoint X=119 Y=35 Z=0
    g13: GeomPoint X=121 Y=33 Z=0
    g14: LineSegment StartX=119 StartY=35 StartZ=0 EndX=114 EndY=35 EndZ=0
    g15: ArcOfCircle CenterX=105 CenterY=19 CenterZ=0 NormalX=0 NormalY=0 NormalZ=1 AngleXU=0 Radius=19 StartAngle=5.7297 EndAngle=6.28319
    g16: ArcOfCircle CenterX=105 CenterY=19 CenterZ=0 NormalX=0 NormalY=0 NormalZ=1 AngleXU=0 Radius=16 StartAngle=5.60905 EndAngle=6.28319
    g17: LineSegment StartX=121 StartY=33 StartZ=0 EndX=121 EndY=19 EndZ=0
    g18: LineSegment StartX=124 StartY=38 StartZ=0 EndX=124 EndY=19 EndZ=0
    g19: LineSegment StartX=117.5 StartY=9.01251 StartZ=0 EndX=121.163 EndY=9.0125 EndZ=0
  constraints (46):
    c: Vertical(g0)
    c: Block(g0)
    c: Coincident(g1,g0)
    c: Block(g1)
    c: Coincident(g2,g1)
    c: Block(g2)
    c: Coincident(g3,g2)
    c: Horizontal(g3)
    c: Tangent(g3,g2)
    c: Coincident(g4,g0)
    c: Distance(g4) = 3
    c: Vertical(g4)
    c: Coincident(g5,g4)
    c: Horizontal(g5)
    c: Coincident(g6,g2)
    c: Coincident(g6,g5)
    c: Vertical(g6)
    c: Horizontal(g7)
    c: Distance(g7) = 105
    c: Coincident(g7,g1)
    c: Block(g3)
    c: Weight(g8) = 1
    c: Equal(g8,g9)
    c: Equal(g8,g10)
    c: InternalAlignment(g8,g11)
    c: InternalAlignment(g9,g11)
    c: InternalAlignment(g10,g11)
    c: InternalAlignment(g12,g11)
    c: InternalAlignment(g13,g11)
    c: Block(g11)
    c: Coincident(g14,g11)
    c: Coincident(g14,g3)
    c: Horizontal(g14)
    c: Block(g15)
    c: Coincident(g16,g15)
    c: Block(g16)
    c: Coincident(g17,g11)
    c: Coincident(g17,g16)
    c: Vertical(g17)
    c: Distance(g17) = 14
    c: Coincident(g18,g7)
    c: Coincident(g18,g15)
    c: Vertical(g18)
    c: Distance(g18) = 19
    c: Coincident(g19,g16)
    c: Coincident(g19,g15)
FEATURE [Part::Extrusion] Extrude049  label="top023"
  Base = -> Sketch058
  Dir = (0,0,1)
  DirMode = 2
  FaceMakerClass = Part::FaceMakerBullseye
  LengthFwd = 72
  LengthRev = 0
  Solid = true
  Symmetric = false
FEATURE [Sketcher::SketchObject] Sketch059
  FullyConstrained = true
  MapMode = 3
  Placement = pos=(0,0,0) rot=(1,0,0;1.5708rad)
  Support = -> [Extrude049]
  sketch-geometry (8):
    g0: Circle CenterX=80.351 CenterY=-67.6202 CenterZ=0 NormalX=0 NormalY=0 NormalZ=1 AngleXU=0 Radius=2
    g1: Circle CenterX=80.351 CenterY=-67.6202 CenterZ=0 NormalX=0 NormalY=0 NormalZ=1 AngleXU=0 Radius=3
    g2: Circle CenterX=80.351 CenterY=-4.92017 CenterZ=0 NormalX=0 NormalY=0 NormalZ=1 AngleXU=0 Radius=2
    g3: Circle CenterX=80.351 CenterY=-4.92017 CenterZ=0 NormalX=0 NormalY=0 NormalZ=1 AngleXU=0 Radius=3
    g4: Circle CenterX=23.851 CenterY=-4.92017 CenterZ=0 NormalX=0 NormalY=0 NormalZ=1 AngleXU=0 Radius=2
    g5: Circle CenterX=23.851 CenterY=-4.92017 CenterZ=0 NormalX=0 NormalY=0 NormalZ=1 AngleXU=0 Radius=3
    g6: Circle CenterX=23.851 CenterY=-67.6202 CenterZ=0 NormalX=0 NormalY=0 NormalZ=1 AngleXU=0 Radius=2
    g7: Circle CenterX=23.851 CenterY=-67.6202 CenterZ=0 NormalX=0 NormalY=0 NormalZ=1 AngleXU=0 Radius=3
  constraints (8):
    c: Block(g3)
    c: Block(g2)
    c: Block(g1)
    c: Block(g0)
    c: Block(g6)
    c: Block(g7)
    c: Block(g4)
    c: Block(g5)
FEATURE [Sketcher::SketchObject] Sketch060
  FullyConstrained = true
  MapMode = 3
  Placement = pos=(0,0,0) rot=(1,0,0;1.5708rad)
  Support = -> [Extrude049]
  sketch-geometry (8):
    g0: Circle CenterX=80.351 CenterY=-67.6202 CenterZ=0 NormalX=0 NormalY=0 NormalZ=1 AngleXU=0 Radius=3
    g1: Circle CenterX=80.351 CenterY=-4.92017 CenterZ=0 NormalX=0 NormalY=0 NormalZ=1 AngleXU=0 Radius=3
    g2: Circle CenterX=23.851 CenterY=-4.92017 CenterZ=0 NormalX=0 NormalY=0 NormalZ=1 AngleXU=0 Radius=3
    g3: Circle CenterX=23.851 CenterY=-67.6202 CenterZ=0 NormalX=0 NormalY=0 NormalZ=1 AngleXU=0 Radius=3
    g4: Circle CenterX=23.851 CenterY=-67.6202 CenterZ=0 NormalX=0 NormalY=0 NormalZ=1 AngleXU=0 Radius=5
    g5: Circle CenterX=80.351 CenterY=-67.6202 CenterZ=0 NormalX=0 NormalY=0 NormalZ=1 AngleXU=0 Radius=5
    g6: Circle CenterX=23.851 CenterY=-4.92017 CenterZ=0 NormalX=0 NormalY=0 NormalZ=1 AngleXU=0 Radius=5
    g7: Circle CenterX=80.351 CenterY=-4.92017 CenterZ=0 NormalX=0 NormalY=0 NormalZ=1 AngleXU=0 Radius=5
  constraints (8):
    c: Block(g1)
    c: Block(g0)
    c: Block(g3)
    c: Block(g2)
    c: Block(g5)
    c: Block(g4)
    c: Block(g6)
    c: Block(g7)
FEATURE [Sketcher::SketchObject] Sketch061
  FullyConstrained = true
  MapMode = 3
  Placement = pos=(0,0,0) rot=(1,0,0;1.5708rad)
  sketch-geometry (8):
    g0: Circle CenterX=80.351 CenterY=-67.6202 CenterZ=0 NormalX=0 NormalY=0 NormalZ=1 AngleXU=0 Radius=3
    g1: Circle CenterX=80.351 CenterY=-4.92017 CenterZ=0 NormalX=0 NormalY=0 NormalZ=1 AngleXU=0 Radius=3
    g2: Circle CenterX=23.851 CenterY=-4.92017 CenterZ=0 NormalX=0 NormalY=0 NormalZ=1 AngleXU=0 Radius=3
    g3: Circle CenterX=23.851 CenterY=-67.6202 CenterZ=0 NormalX=0 NormalY=0 NormalZ=1 AngleXU=0 Radius=3
    g4: Circle CenterX=23.851 CenterY=-67.6202 CenterZ=0 NormalX=0 NormalY=0 NormalZ=1 AngleXU=0 Radius=5
    g5: Circle CenterX=80.351 CenterY=-67.6202 CenterZ=0 NormalX=0 NormalY=0 NormalZ=1 AngleXU=0 Radius=5
    g6: Circle CenterX=23.851 CenterY=-4.92017 CenterZ=0 NormalX=0 NormalY=0 NormalZ=1 AngleXU=0 Radius=5
    g7: Circle CenterX=80.351 CenterY=-4.92017 CenterZ=0 NormalX=0 NormalY=0 NormalZ=1 AngleXU=0 Radius=5
  constraints (8):
    c: Block(g1)
    c: Block(g0)
    c: Block(g3)
    c: Block(g2)
    c: Block(g5)
    c: Block(g4)
    c: Block(g6)
    c: Block(g7)
FEATURE [Sketcher::SketchObject] Sketch062  label="topSketch016"
  FullyConstrained = true
  sketch-geometry (20):
    g0: LineSegment StartX=5.21097e-06 StartY=3 StartZ=0 EndX=5.21097e-06 EndY=19 EndZ=0
    g1: ArcOfCircle CenterX=19 CenterY=19 CenterZ=0 NormalX=0 NormalY=0 NormalZ=1 AngleXU=0 Radius=19 StartAngle=1.5708 EndAngle=3.14159
    g2: ArcOfCircle CenterX=19 CenterY=19 CenterZ=0 NormalX=0 NormalY=0 NormalZ=1 AngleXU=0 Radius=16 StartAngle=1.5708 EndAngle=3.14159
    g3: LineSegment StartX=114 StartY=35 StartZ=0 EndX=19 EndY=35 EndZ=0
    g4: LineSegment StartX=5.21097e-06 StartY=3 StartZ=0 EndX=5.21097e-06 EndY=0 EndZ=0
    g5: LineSegment StartX=3 StartY=0 StartZ=0 EndX=5.21097e-06 EndY=0 EndZ=0
    g6: LineSegment StartX=3 StartY=19 StartZ=0 EndX=3 EndY=0 EndZ=0
    g7: LineSegment StartX=19 StartY=38 StartZ=0 EndX=124 EndY=38 EndZ=0
    g8: Circle CenterX=119 CenterY=35 CenterZ=0 NormalX=0 NormalY=0 NormalZ=1 AngleXU=0 Radius=1
    g9: Circle CenterX=121 CenterY=35 CenterZ=0 NormalX=0 NormalY=0 NormalZ=1 AngleXU=0 Radius=1
    g10: Circle CenterX=121 CenterY=33 CenterZ=0 NormalX=0 NormalY=0 NormalZ=1 AngleXU=0 Radius=1
    g11: BSplineCurve PolesCount=3 KnotsCount=2 Degree=2 IsPeriodic=0
    g12: GeomPoint X=119 Y=35 Z=0
    g13: GeomPoint X=121 Y=33 Z=0
    g14: LineSegment StartX=119 StartY=35 StartZ=0 EndX=114 EndY=35 EndZ=0
    g15: ArcOfCircle CenterX=105 CenterY=19 CenterZ=0 NormalX=0 NormalY=0 NormalZ=1 AngleXU=0 Radius=19 StartAngle=5.7297 EndAngle=6.28319
    g16: ArcOfCircle CenterX=105 CenterY=19 CenterZ=0 NormalX=0 NormalY=0 NormalZ=1 AngleXU=0 Radius=16 StartAngle=5.60905 EndAngle=6.28319
    g17: LineSegment StartX=121 StartY=33 StartZ=0 EndX=121 EndY=19 EndZ=0
    g18: LineSegment StartX=124 StartY=38 StartZ=0 EndX=124 EndY=19 EndZ=0
    g19: LineSegment StartX=117.5 StartY=9.01251 StartZ=0 EndX=121.163 EndY=9.0125 EndZ=0
  constraints (46):
    c: Vertical(g0)
    c: Block(g0)
    c: Coincident(g1,g0)
    c: Block(g1)
    c: Coincident(g2,g1)
    c: Block(g2)
    c: Coincident(g3,g2)
    c: Horizontal(g3)
    c: Tangent(g3,g2)
    c: Coincident(g4,g0)
    c: Distance(g4) = 3
    c: Vertical(g4)
    c: Coincident(g5,g4)
    c: Horizontal(g5)
    c: Coincident(g6,g2)
    c: Coincident(g6,g5)
    c: Vertical(g6)
    c: Horizontal(g7)
    c: Distance(g7) = 105
    c: Coincident(g7,g1)
    c: Block(g3)
    c: Weight(g8) = 1
    c: Equal(g8,g9)
    c: Equal(g8,g10)
    c: InternalAlignment(g8,g11)
    c: InternalAlignment(g9,g11)
    c: InternalAlignment(g10,g11)
    c: InternalAlignment(g12,g11)
    c: InternalAlignment(g13,g11)
    c: Block(g11)
    c: Coincident(g14,g11)
    c: Coincident(g14,g3)
    c: Horizontal(g14)
    c: Block(g15)
    c: Coincident(g16,g15)
    c: Block(g16)
    c: Coincident(g17,g11)
    c: Coincident(g17,g16)
    c: Vertical(g17)
    c: Distance(g17) = 14
    c: Coincident(g18,g7)
    c: Coincident(g18,g15)
    c: Vertical(g18)
    c: Distance(g18) = 19
    c: Coincident(g19,g16)
    c: Coincident(g19,g15)
FEATURE [Part::Extrusion] Extrude053  label="top024"
  Base = -> Sketch062
  Dir = (0,0,1)
  DirMode = 2
  FaceMakerClass = Part::FaceMakerBullseye
  LengthFwd = 72
  LengthRev = 0
  Solid = true
  Symmetric = false
FEATURE [Sketcher::SketchObject] Sketch063
  FullyConstrained = true
  MapMode = 3
  Placement = pos=(0,0,0) rot=(1,0,0;1.5708rad)
  Support = -> [Extrude053]
  sketch-geometry (8):
    g0: Circle CenterX=80.351 CenterY=-67.6202 CenterZ=0 NormalX=0 NormalY=0 NormalZ=1 AngleXU=0 Radius=2
    g1: Circle CenterX=80.351 CenterY=-67.6202 CenterZ=0 NormalX=0 NormalY=0 NormalZ=1 AngleXU=0 Radius=3
    g2: Circle CenterX=80.351 CenterY=-4.92017 CenterZ=0 NormalX=0 NormalY=0 NormalZ=1 AngleXU=0 Radius=2
    g3: Circle CenterX=80.351 CenterY=-4.92017 CenterZ=0 NormalX=0 NormalY=0 NormalZ=1 AngleXU=0 Radius=3
    g4: Circle CenterX=23.851 CenterY=-4.92017 CenterZ=0 NormalX=0 NormalY=0 NormalZ=1 AngleXU=0 Radius=2
    g5: Circle CenterX=23.851 CenterY=-4.92017 CenterZ=0 NormalX=0 NormalY=0 NormalZ=1 AngleXU=0 Radius=3
    g6: Circle CenterX=23.851 CenterY=-67.6202 CenterZ=0 NormalX=0 NormalY=0 NormalZ=1 AngleXU=0 Radius=2
    g7: Circle CenterX=23.851 CenterY=-67.6202 CenterZ=0 NormalX=0 NormalY=0 NormalZ=1 AngleXU=0 Radius=3
  constraints (8):
    c: Block(g3)
    c: Block(g2)
    c: Block(g1)
    c: Block(g0)
    c: Block(g6)
    c: Block(g7)
    c: Block(g4)
    c: Block(g5)
FEATURE [Part::Extrusion] Extrude054
  Base = -> Sketch063
  Dir = (0,-1,2e-16)
  DirMode = 2
  FaceMakerClass = Part::FaceMakerBullseye
  LengthFwd = 6
  LengthRev = 0
  Placement = pos=(0,9,0) rot=(0,0,1;0rad)
  Solid = true
  Symmetric = false
FEATURE [Sketcher::SketchObject] Sketch064  label="topSketch017"
  FullyConstrained = true
  sketch-geometry (20):
    g0: LineSegment StartX=5.21097e-06 StartY=3 StartZ=0 EndX=5.21097e-06 EndY=19 EndZ=0
    g1: ArcOfCircle CenterX=19 CenterY=19 CenterZ=0 NormalX=0 NormalY=0 NormalZ=1 AngleXU=0 Radius=19 StartAngle=1.5708 EndAngle=3.14159
    g2: ArcOfCircle CenterX=19 CenterY=19 CenterZ=0 NormalX=0 NormalY=0 NormalZ=1 AngleXU=0 Radius=16 StartAngle=1.5708 EndAngle=3.14159
    g3: LineSegment StartX=114 StartY=35 StartZ=0 EndX=19 EndY=35 EndZ=0
    g4: LineSegment StartX=5.21097e-06 StartY=3 StartZ=0 EndX=5.21097e-06 EndY=0 EndZ=0
    g5: LineSegment StartX=3 StartY=0 StartZ=0 EndX=5.21097e-06 EndY=0 EndZ=0
    g6: LineSegment StartX=3 StartY=19 StartZ=0 EndX=3 EndY=0 EndZ=0
    g7: LineSegment StartX=19 StartY=38 StartZ=0 EndX=124 EndY=38 EndZ=0
    g8: Circle CenterX=119 CenterY=35 CenterZ=0 NormalX=0 NormalY=0 NormalZ=1 AngleXU=0 Radius=1
    g9: Circle CenterX=121 CenterY=35 CenterZ=0 NormalX=0 NormalY=0 NormalZ=1 AngleXU=0 Radius=1
    g10: Circle CenterX=121 CenterY=33 CenterZ=0 NormalX=0 NormalY=0 NormalZ=1 AngleXU=0 Radius=1
    g11: BSplineCurve PolesCount=3 KnotsCount=2 Degree=2 IsPeriodic=0
    g12: GeomPoint X=119 Y=35 Z=0
    g13: GeomPoint X=121 Y=33 Z=0
    g14: LineSegment StartX=119 StartY=35 StartZ=0 EndX=114 EndY=35 EndZ=0
    g15: ArcOfCircle CenterX=105 CenterY=19 CenterZ=0 NormalX=0 NormalY=0 NormalZ=1 AngleXU=0 Radius=19 StartAngle=5.7297 EndAngle=6.28319
    g16: ArcOfCircle CenterX=105 CenterY=19 CenterZ=0 NormalX=0 NormalY=0 NormalZ=1 AngleXU=0 Radius=16 StartAngle=5.60905 EndAngle=6.28319
    g17: LineSegment StartX=121 StartY=33 StartZ=0 EndX=121 EndY=19 EndZ=0
    g18: LineSegment StartX=124 StartY=38 StartZ=0 EndX=124 EndY=19 EndZ=0
    g19: LineSegment StartX=117.5 StartY=9.01251 StartZ=0 EndX=121.163 EndY=9.0125 EndZ=0
  constraints (46):
    c: Vertical(g0)
    c: Block(g0)
    c: Coincident(g1,g0)
    c: Block(g1)
    c: Coincident(g2,g1)
    c: Block(g2)
    c: Coincident(g3,g2)
    c: Horizontal(g3)
    c: Tangent(g3,g2)
    c: Coincident(g4,g0)
    c: Distance(g4) = 3
    c: Vertical(g4)
    c: Coincident(g5,g4)
    c: Horizontal(g5)
    c: Coincident(g6,g2)
    c: Coincident(g6,g5)
    c: Vertical(g6)
    c: Horizontal(g7)
    c: Distance(g7) = 105
    c: Coincident(g7,g1)
    c: Block(g3)
    c: Weight(g8) = 1
    c: Equal(g8,g9)
    c: Equal(g8,g10)
    c: InternalAlignment(g8,g11)
    c: InternalAlignment(g9,g11)
    c: InternalAlignment(g10,g11)
    c: InternalAlignment(g12,g11)
    c: InternalAlignment(g13,g11)
    c: Block(g11)
    c: Coincident(g14,g11)
    c: Coincident(g14,g3)
    c: Horizontal(g14)
    c: Block(g15)
    c: Coincident(g16,g15)
    c: Block(g16)
    c: Coincident(g17,g11)
    c: Coincident(g17,g16)
    c: Vertical(g17)
    c: Distance(g17) = 14
    c: Coincident(g18,g7)
    c: Coincident(g18,g15)
    c: Vertical(g18)
    c: Distance(g18) = 19
    c: Coincident(g19,g16)
    c: Coincident(g19,g15)
FEATURE [Sketcher::SketchObject] Sketch065
  FullyConstrained = true
  MapMode = 3
  Placement = pos=(0,0,0) rot=(1,0,0;1.5708rad)
  sketch-geometry (8):
    g0: Circle CenterX=80.351 CenterY=-67.6202 CenterZ=0 NormalX=0 NormalY=0 NormalZ=1 AngleXU=0 Radius=3
    g1: Circle CenterX=80.351 CenterY=-4.92017 CenterZ=0 NormalX=0 NormalY=0 NormalZ=1 AngleXU=0 Radius=3
    g2: Circle CenterX=23.851 CenterY=-4.92017 CenterZ=0 NormalX=0 NormalY=0 NormalZ=1 AngleXU=0 Radius=3
    g3: Circle CenterX=23.851 CenterY=-67.6202 CenterZ=0 NormalX=0 NormalY=0 NormalZ=1 AngleXU=0 Radius=3
    g4: Circle CenterX=23.851 CenterY=-67.6202 CenterZ=0 NormalX=0 NormalY=0 NormalZ=1 AngleXU=0 Radius=5
    g5: Circle CenterX=80.351 CenterY=-67.6202 CenterZ=0 NormalX=0 NormalY=0 NormalZ=1 AngleXU=0 Radius=5
    g6: Circle CenterX=23.851 CenterY=-4.92017 CenterZ=0 NormalX=0 NormalY=0 NormalZ=1 AngleXU=0 Radius=5
    g7: Circle CenterX=80.351 CenterY=-4.92017 CenterZ=0 NormalX=0 NormalY=0 NormalZ=1 AngleXU=0 Radius=5
  constraints (8):
    c: Block(g1)
    c: Block(g0)
    c: Block(g3)
    c: Block(g2)
    c: Block(g5)
    c: Block(g4)
    c: Block(g6)
    c: Block(g7)
FEATURE [Part::Extrusion] Extrude056
  Base = -> Sketch065
  Dir = (0,-1,2e-16)
  DirMode = 2
  FaceMakerClass = Part::FaceMakerBullseye
  LengthFwd = 2
  LengthRev = 0
  Solid = true
  Symmetric = false
FEATURE [Part::Extrusion] Extrude057  label="top025"
  Base = -> Sketch064
  Dir = (0,0,1)
  DirMode = 2
  FaceMakerClass = Part::FaceMakerBullseye
  LengthFwd = 72
  LengthRev = 0
  Solid = true
  Symmetric = false
FEATURE [Sketcher::SketchObject] Sketch066
  FullyConstrained = true
  MapMode = 3
  Placement = pos=(0,0,0) rot=(1,0,0;1.5708rad)
  Support = -> [Extrude057]
  sketch-geometry (8):
    g0: Circle CenterX=80.351 CenterY=-67.6202 CenterZ=0 NormalX=0 NormalY=0 NormalZ=1 AngleXU=0 Radius=3
    g1: Circle CenterX=80.351 CenterY=-4.92017 CenterZ=0 NormalX=0 NormalY=0 NormalZ=1 AngleXU=0 Radius=3
    g2: Circle CenterX=23.851 CenterY=-4.92017 CenterZ=0 NormalX=0 NormalY=0 NormalZ=1 AngleXU=0 Radius=3
    g3: Circle CenterX=23.851 CenterY=-67.6202 CenterZ=0 NormalX=0 NormalY=0 NormalZ=1 AngleXU=0 Radius=3
    g4: Circle CenterX=23.851 CenterY=-67.6202 CenterZ=0 NormalX=0 NormalY=0 NormalZ=1 AngleXU=0 Radius=5
    g5: Circle CenterX=80.351 CenterY=-67.6202 CenterZ=0 NormalX=0 NormalY=0 NormalZ=1 AngleXU=0 Radius=5
    g6: Circle CenterX=23.851 CenterY=-4.92017 CenterZ=0 NormalX=0 NormalY=0 NormalZ=1 AngleXU=0 Radius=5
    g7: Circle CenterX=80.351 CenterY=-4.92017 CenterZ=0 NormalX=0 NormalY=0 NormalZ=1 AngleXU=0 Radius=5
  constraints (8):
    c: Block(g1)
    c: Block(g0)
    c: Block(g3)
    c: Block(g2)
    c: Block(g5)
    c: Block(g4)
    c: Block(g6)
    c: Block(g7)
FEATURE [Part::Extrusion] Extrude055
  Base = -> Sketch066
  Dir = (0,-1,2e-16)
  DirMode = 2
  FaceMakerClass = Part::FaceMakerBullseye
  LengthFwd = 2
  LengthRev = 0
  Solid = true
  Symmetric = false
FEATURE [Part::Fillet] Fillet041
  Base = -> Extrude056
  Edges = 4 edges r=1.99: [Edge6,Edge12,Edge18,Edge24]
FEATURE [Part::Cut] Cut045
  Base = -> Extrude055
  Placement = pos=(0,6,0) rot=(0,0,1;0rad)
  Tool = -> Fillet041
FEATURE [Part::MultiFuse] Fusion095  label="pcbScrewPillars"
  Placement = pos=(-3.2,-1,72.3) rot=(0,0,1;0rad)
  Shapes = -> [Cut045,Extrude054]
FEATURE [Part::Feature] Face113
  shape: bbox 3.2 x 1.5 x 2e-07 mm, 1 faces, 0 solids (baked)
FEATURE [Part::Revolution] Revolve121  label="backCaseScrewRetainer002"
  Angle = 360
  Axis = (0,1,0)
  Base = (0,0,0)
  FaceMakerClass = Part::FaceMakerBullseye
  Placement = pos=(12.5,3,62) rot=(0,0,1;0rad)
  Solid = false
  Source = -> Face113
  Symmetric = false
FEATURE [Part::Feature] Face114
  shape: bbox 3.2 x 1.5 x 2e-07 mm, 1 faces, 0 solids (baked)
FEATURE [Part::Feature] Face115
  shape: bbox 3.2 x 1.5 x 2e-07 mm, 1 faces, 0 solids (baked)
FEATURE [Part::Feature] Face116
  shape: bbox 3.2 x 1.5 x 2e-07 mm, 1 faces, 0 solids (baked)
FEATURE [Part::Revolution] Revolve122  label="frontCaseScrewRetainer004"
  Angle = 360
  Axis = (0,1,0)
  Base = (0,0,0)
  FaceMakerClass = Part::FaceMakerBullseye
  Placement = pos=(89.5,3,68.5) rot=(0,0,1;0rad)
  Solid = false
  Source = -> Face115
  Symmetric = false
FEATURE [Part::Revolution] Revolve123  label="frontCaseScrewRetainer005"
  Angle = 360
  Axis = (0,1,0)
  Base = (0,0,0)
  FaceMakerClass = Part::FaceMakerBullseye
  Placement = pos=(89.5,3,3.5) rot=(0,0,1;0rad)
  Solid = false
  Source = -> Face116
  Symmetric = false
FEATURE [Part::Revolution] Revolve124  label="backCaseScrewRetainer003"
  Angle = 360
  Axis = (0,1,0)
  Base = (0,0,0)
  FaceMakerClass = Part::FaceMakerBullseye
  Placement = pos=(12.5,3,10) rot=(0,0,1;0rad)
  Solid = false
  Source = -> Face114
  Symmetric = false
FEATURE [Part::Feature] Face117
  shape: bbox 3.6 x 3.2 x 2e-07 mm, 1 faces, 0 solids (baked)
FEATURE [Part::Revolution] Revolve125  label="moreFrontCaseScrewRetainer004"
  Angle = 360
  Axis = (0,1,0)
  Base = (0,0,0)
  FaceMakerClass = Part::FaceMakerBullseye
  Placement = pos=(109.5,4.5,68.5) rot=(0,0,1;0rad)
  Solid = false
  Source = -> Face117
  Symmetric = false
FEATURE [Part::Feature] Face118
  shape: bbox 3.6 x 3.2 x 2e-07 mm, 1 faces, 0 solids (baked)
FEATURE [Part::Revolution] Revolve126  label="moreFrontCaseScrewRetainer005"
  Angle = 360
  Axis = (0,1,0)
  Base = (0,0,0)
  FaceMakerClass = Part::FaceMakerBullseye
  Placement = pos=(109.5,4.5,3.5) rot=(0,0,1;0rad)
  Solid = false
  Source = -> Face118
  Symmetric = false
FEATURE [Part::MultiFuse] Fusion096  label="screwRetainers001"
  Shapes = -> [Revolve126,Revolve125,Revolve124,Revolve123,Revolve122,Revolve121]
FEATURE [Part::Feature] Face119
  shape: bbox 10 x 16.5 x 2e-07 mm, 1 faces, 0 solids (baked)
FEATURE [Part::Revolution] Revolve130  label="plugHousing050"
  Angle = 360
  Axis = (0,1,0)
  Base = (0,0,0)
  FaceMakerClass = Part::FaceMakerBullseye
  Placement = pos=(0,0,36.15) rot=(0,0,1;0rad)
  Solid = false
  Source = -> Face119
  Symmetric = false
FEATURE [Part::Feature] Face120
  shape: bbox 10 x 16.5 x 2e-07 mm, 1 faces, 0 solids (baked)
FEATURE [Part::Feature] Face121
  shape: bbox 10 x 16.5 x 2e-07 mm, 1 faces, 0 solids (baked)
FEATURE [Part::Revolution] Revolve127  label="plugHousing047"
  Angle = 360
  Axis = (0,1,0)
  Base = (0,0,0)
  FaceMakerClass = Part::FaceMakerBullseye
  Placement = pos=(0,0,36.15) rot=(0,0,1;0rad)
  Solid = false
  Source = -> Face121
  Symmetric = false
FEATURE [Part::Feature] Face122
  shape: bbox 10 x 16.5 x 2e-07 mm, 1 faces, 0 solids (baked)
FEATURE [Part::Feature] Face123
  shape: bbox 10 x 16.5 x 2e-07 mm, 1 faces, 0 solids (baked)
FEATURE [Part::Revolution] Revolve128  label="plugHousing048"
  Angle = 360
  Axis = (0,1,0)
  Base = (0,0,0)
  FaceMakerClass = Part::FaceMakerBullseye
  Placement = pos=(0,0,36.15) rot=(0,0,1;0rad)
  Solid = false
  Source = -> Face123
  Symmetric = false
FEATURE [Part::MultiFuse] Fusion100  label="plugHousing054"
  Placement = pos=(0,0,0) rot=(0,0,1;1.5708rad)
  Shapes = -> [Revolve130,Revolve128]
FEATURE [Part::Feature] Face124
  shape: bbox 10 x 16.5 x 2e-07 mm, 1 faces, 0 solids (baked)
FEATURE [Part::Feature] Face125
  shape: bbox 10 x 16.5 x 2e-07 mm, 1 faces, 0 solids (baked)
FEATURE [Part::Revolution] Revolve129  label="plugHousing049"
  Angle = 360
  Axis = (0,1,0)
  Base = (0,0,0)
  FaceMakerClass = Part::FaceMakerBullseye
  Placement = pos=(0,0,36.15) rot=(0,0,1;0rad)
  Solid = false
  Source = -> Face125
  Symmetric = false
FEATURE [Part::Feature] Face126
  shape: bbox 10 x 16.5 x 2e-07 mm, 1 faces, 0 solids (baked)
FEATURE [Part::Revolution] Revolve131  label="plugHousing058"
  Angle = 360
  Axis = (0,1,0)
  Base = (0,0,0)
  FaceMakerClass = Part::FaceMakerBullseye
  Placement = pos=(0,0,36.15) rot=(0,0,1;0rad)
  Solid = false
  Source = -> Face120
  Symmetric = false
FEATURE [Part::MultiFuse] Fusion099  label="plugHousing053"
  Placement = pos=(0,0,0) rot=(0,0,1;1.5708rad)
  Shapes = -> [Revolve127,Revolve131]
FEATURE [Part::MultiFuse] Fusion102  label="plugHousing056"
  Placement = pos=(0,19,0) rot=(0,0,1;3.14159rad)
  Shapes = -> [Fusion100,Fusion099]
FEATURE [Part::Revolution] Revolve132  label="plugHousing059"
  Angle = 360
  Axis = (0,1,0)
  Base = (0,0,0)
  FaceMakerClass = Part::FaceMakerBullseye
  Placement = pos=(0,0,36.15) rot=(0,0,1;0rad)
  Solid = false
  Source = -> Face126
  Symmetric = false
FEATURE [Part::Revolution] Revolve133  label="plugHousing060"
  Angle = 360
  Axis = (0,1,0)
  Base = (0,0,0)
  FaceMakerClass = Part::FaceMakerBullseye
  Placement = pos=(0,0,36.15) rot=(0,0,1;0rad)
  Solid = false
  Source = -> Face122
  Symmetric = false
FEATURE [Part::MultiFuse] Fusion097  label="plugHousing051"
  Placement = pos=(0,0,0) rot=(0,0,1;1.5708rad)
  Shapes = -> [Revolve133,Revolve132]
FEATURE [Part::Revolution] Revolve134  label="plugHousing061"
  Angle = 360
  Axis = (0,1,0)
  Base = (0,0,0)
  FaceMakerClass = Part::FaceMakerBullseye
  Placement = pos=(0,0,36.15) rot=(0,0,1;0rad)
  Solid = false
  Source = -> Face124
  Symmetric = false
FEATURE [Part::MultiFuse] Fusion101  label="plugHousing055"
  Placement = pos=(0,0,0) rot=(0,0,1;1.5708rad)
  Shapes = -> [Revolve129,Revolve134]
FEATURE [Part::MultiFuse] Fusion098  label="plugHousing052"
  Placement = pos=(0,19,0) rot=(0,0,1;3.14159rad)
  Shapes = -> [Fusion097,Fusion101]
FEATURE [Part::MultiFuse] Fusion103  label="plugHousing057"
  Placement = pos=(122.621,0,-0.15) rot=(0,0,1;0rad)
  Shapes = -> [Fusion102,Fusion098]
FEATURE [Part::Box] Box028  label="Cube015"
  AttacherType = Attacher::AttachEngine3D
  Height = 28
  Length = 3
  Placement = pos=(110.7,19,22) rot=(0,0,1;0rad)
  Width = 15.7
FEATURE [Part::Cylinder] Cylinder044
  Angle = 360
  AttacherType = Attacher::AttachEngine3D
  Height = 20
  Placement = pos=(0,0,36.15) rot=(0,0,1;0rad)
  Radius = 10.3
FEATURE [Part::Cylinder] Cylinder045
  Angle = 360
  AttacherType = Attacher::AttachEngine3D
  Height = 10
  Placement = pos=(0,0,36.15) rot=(0,0,1;0rad)
  Radius = 4
FEATURE [Part::MultiFuse] Fusion104  label="removeToCreteHoleForPlugHousing040"
  Placement = pos=(70,19,36) rot=(0,1,0;1.5708rad)
  Shapes = -> [Cylinder044,Cylinder045]
FEATURE [Part::Cut] Cut046  label="plugHousingTab003"
  Base = -> Box028
  Tool = -> Fusion104
FEATURE [Part::MultiFuse] Fusion105  label="plugHousing062"
  Shapes = -> [Fusion103,Cut046]
FEATURE [Part::Fillet] Fillet042
  Base = -> Fusion105
  Edges = 1 edges r=2: [Edge25]
FEATURE [Part::Fillet] Fillet043  label="plugHousing063"
  Base = -> Fillet042
  Edges = 1 edges r=2: [Edge8]
  Placement = pos=(7,0,0) rot=(0,0,1;0rad)
FEATURE [Part::Feature] Face127
  shape: bbox 10 x 16.5 x 2e-07 mm, 1 faces, 0 solids (baked)
FEATURE [Part::Feature] Face128
  shape: bbox 10 x 16.5 x 2e-07 mm, 1 faces, 0 solids (baked)
FEATURE [Part::Revolution] Revolve137  label="plugHousing070"
  Angle = 360
  Axis = (0,1,0)
  Base = (0,0,0)
  FaceMakerClass = Part::FaceMakerBullseye
  Placement = pos=(0,0,36.15) rot=(0,0,1;0rad)
  Solid = false
  Source = -> Face127
  Symmetric = false
FEATURE [Part::Revolution] Revolve140  label="plugHousing073"
  Angle = 360
  Axis = (0,1,0)
  Base = (0,0,0)
  FaceMakerClass = Part::FaceMakerBullseye
  Placement = pos=(0,0,36.15) rot=(0,0,1;0rad)
  Solid = false
  Source = -> Face128
  Symmetric = false
FEATURE [Part::Feature] Face129
  shape: bbox 10 x 16.5 x 2e-07 mm, 1 faces, 0 solids (baked)
FEATURE [Part::Revolution] Revolve138  label="plugHousing071"
  Angle = 360
  Axis = (0,1,0)
  Base = (0,0,0)
  FaceMakerClass = Part::FaceMakerBullseye
  Placement = pos=(0,0,36.15) rot=(0,0,1;0rad)
  Solid = false
  Source = -> Face129
  Symmetric = false
FEATURE [Part::Feature] Face130
  shape: bbox 10 x 16.5 x 2e-07 mm, 1 faces, 0 solids (baked)
FEATURE [Part::Revolution] Revolve139  label="plugHousing072"
  Angle = 360
  Axis = (0,1,0)
  Base = (0,0,0)
  FaceMakerClass = Part::FaceMakerBullseye
  Placement = pos=(0,0,36.15) rot=(0,0,1;0rad)
  Solid = false
  Source = -> Face130
  Symmetric = false
FEATURE [Part::Feature] Face131
  shape: bbox 10 x 16.5 x 2e-07 mm, 1 faces, 0 solids (baked)
FEATURE [Part::Revolution] Revolve135  label="plugHousing068"
  Angle = 360
  Axis = (0,1,0)
  Base = (0,0,0)
  FaceMakerClass = Part::FaceMakerBullseye
  Placement = pos=(0,0,36.15) rot=(0,0,1;0rad)
  Solid = false
  Source = -> Face131
  Symmetric = false
FEATURE [Part::MultiFuse] Fusion112  label="plugHousing078"
  Placement = pos=(0,0,0) rot=(0,0,1;1.5708rad)
  Shapes = -> [Revolve135,Revolve139]
FEATURE [Part::Feature] Face132
  shape: bbox 10 x 16.5 x 2e-07 mm, 1 faces, 0 solids (baked)
FEATURE [Part::Revolution] Revolve141  label="plugHousing074"
  Angle = 360
  Axis = (0,1,0)
  Base = (0,0,0)
  FaceMakerClass = Part::FaceMakerBullseye
  Placement = pos=(0,0,36.15) rot=(0,0,1;0rad)
  Solid = false
  Source = -> Face132
  Symmetric = false
FEATURE [Part::MultiFuse] Fusion110  label="plugHousing076"
  Placement = pos=(0,0,0) rot=(0,0,1;1.5708rad)
  Shapes = -> [Revolve141,Revolve140]
FEATURE [Part::Feature] Face133
  shape: bbox 10 x 16.5 x 2e-07 mm, 1 faces, 0 solids (baked)
FEATURE [Part::Revolution] Revolve136  label="plugHousing069"
  Angle = 360
  Axis = (0,1,0)
  Base = (0,0,0)
  FaceMakerClass = Part::FaceMakerBullseye
  Placement = pos=(0,0,36.15) rot=(0,0,1;0rad)
  Solid = false
  Source = -> Face133
  Symmetric = false
FEATURE [Part::MultiFuse] Fusion106  label="plugHousing064"
  Placement = pos=(0,0,0) rot=(0,0,1;1.5708rad)
  Shapes = -> [Revolve138,Revolve136]
FEATURE [Part::MultiFuse] Fusion108  label="plugHousing066"
  Placement = pos=(0,19,0) rot=(0,0,1;3.14159rad)
  Shapes = -> [Fusion106,Fusion112]
FEATURE [Part::Feature] Face134
  shape: bbox 10 x 16.5 x 2e-07 mm, 1 faces, 0 solids (baked)
FEATURE [Part::Revolution] Revolve142  label="plugHousing075"
  Angle = 360
  Axis = (0,1,0)
  Base = (0,0,0)
  FaceMakerClass = Part::FaceMakerBullseye
  Placement = pos=(0,0,36.15) rot=(0,0,1;0rad)
  Solid = false
  Source = -> Face134
  Symmetric = false
FEATURE [Part::MultiFuse] Fusion107  label="plugHousing065"
  Placement = pos=(0,0,0) rot=(0,0,1;1.5708rad)
  Shapes = -> [Revolve137,Revolve142]
FEATURE [Part::MultiFuse] Fusion111  label="plugHousing077"
  Placement = pos=(0,19,0) rot=(0,0,1;3.14159rad)
  Shapes = -> [Fusion110,Fusion107]
FEATURE [Part::MultiFuse] Fusion109  label="plugHousing067"
  Placement = pos=(131.236,0,-0.15) rot=(0,0,1;0rad)
  Shapes = -> [Fusion108,Fusion111]
FEATURE [Part::MultiFuse] Fusion113  label="plugHousing079"
  Shapes = -> [Fillet043,Fusion109]
FEATURE [Part::Feature] Face135
  shape: bbox 3.5 x 17.8 x 2e-07 mm, 1 faces, 0 solids (baked)
FEATURE [Part::Revolution] Revolve143  label="removeToCreateScrewAndThreadedInsertHole049"
  Angle = 360
  Axis = (0,1,0)
  Base = (0,0,0)
  FaceMakerClass = Part::FaceMakerBullseye
  Placement = pos=(12.5,0,10) rot=(0,0,1;0rad)
  Solid = false
  Source = -> Face135
  Symmetric = false
FEATURE [Part::Feature] Face136
  shape: bbox 3.5 x 17.8 x 2e-07 mm, 1 faces, 0 solids (baked)
FEATURE [Part::Revolution] Revolve144  label="removeToCreateScrewAndThreadedInsertHole050"
  Angle = 360
  Axis = (0,1,0)
  Base = (0,0,0)
  FaceMakerClass = Part::FaceMakerBullseye
  Placement = pos=(12.5,0,62) rot=(0,0,1;0rad)
  Solid = false
  Source = -> Face136
  Symmetric = false
FEATURE [Part::Feature] Face137
  shape: bbox 3.5 x 17.8 x 2e-07 mm, 1 faces, 0 solids (baked)
FEATURE [Part::Revolution] Revolve145  label="removeToCreateScrewAndThreadedInsertHole051"
  Angle = 360
  Axis = (0,1,0)
  Base = (0,0,0)
  FaceMakerClass = Part::FaceMakerBullseye
  Placement = pos=(89.5,0,68.5) rot=(0,0,1;0rad)
  Solid = false
  Source = -> Face137
  Symmetric = false
FEATURE [Part::Feature] Face138
  shape: bbox 3.5 x 17.8 x 2e-07 mm, 1 faces, 0 solids (baked)
FEATURE [Part::Revolution] Revolve146  label="removeToCreateScrewAndThreadedInsertHole052"
  Angle = 360
  Axis = (0,1,0)
  Base = (0,0,0)
  FaceMakerClass = Part::FaceMakerBullseye
  Placement = pos=(89.5,0,3.5) rot=(0,0,1;0rad)
  Solid = false
  Source = -> Face138
  Symmetric = false
FEATURE [Part::Feature] Face139
  shape: bbox 3.5 x 17.8 x 2e-07 mm, 1 faces, 0 solids (baked)
FEATURE [Part::Revolution] Revolve147  label="removeToCreateScrewAndThreadedInsertHole053"
  Angle = 360
  Axis = (0,1,0)
  Base = (0,0,0)
  FaceMakerClass = Part::FaceMakerBullseye
  Placement = pos=(109.5,4.7,3.5) rot=(0,0,1;0rad)
  Solid = false
  Source = -> Face139
  Symmetric = false
FEATURE [Part::Feature] Face140
  shape: bbox 3.5 x 17.8 x 2e-07 mm, 1 faces, 0 solids (baked)
FEATURE [Part::Revolution] Revolve148  label="removeToCreateScrewAndThreadedInsertHole054"
  Angle = 360
  Axis = (0,1,0)
  Base = (0,0,0)
  FaceMakerClass = Part::FaceMakerBullseye
  Placement = pos=(109.5,4.7,68.5) rot=(0,0,1;0rad)
  Solid = false
  Source = -> Face140
  Symmetric = false
FEATURE [Part::MultiFuse] Fusion114  label="removeToCreateScrewAndThreadedInsertHole055"
  Shapes = -> [Revolve148,Revolve147,Revolve146,Revolve145,Revolve144,Revolve143]
FEATURE [Part::Cut] Cut047  label="casePillars004"
  Base = -> Cut037
  Tool = -> Fusion114
FEATURE [Part::Feature] Face141
  shape: bbox 3.5 x 17.8 x 2e-07 mm, 1 faces, 0 solids (baked)
FEATURE [Part::Feature] Face142
  shape: bbox 3.5 x 17.8 x 2e-07 mm, 1 faces, 0 solids (baked)
FEATURE [Part::Feature] Face143
  shape: bbox 3.5 x 17.8 x 2e-07 mm, 1 faces, 0 solids (baked)
FEATURE [Part::Revolution] Revolve149  label="removeToCreateScrewAndThreadedInsertHole057"
  Angle = 360
  Axis = (0,1,0)
  Base = (0,0,0)
  FaceMakerClass = Part::FaceMakerBullseye
  Placement = pos=(12.5,0,10) rot=(0,0,1;0rad)
  Solid = false
  Source = -> Face141
  Symmetric = false
FEATURE [Part::Feature] Face144
  shape: bbox 3.5 x 17.8 x 2e-07 mm, 1 faces, 0 solids (baked)
FEATURE [Part::Feature] Face145
  shape: bbox 3.5 x 17.8 x 2e-07 mm, 1 faces, 0 solids (baked)
FEATURE [Part::Feature] Face146
  shape: bbox 3.5 x 17.8 x 2e-07 mm, 1 faces, 0 solids (baked)
FEATURE [Part::Revolution] Revolve150  label="removeToCreateScrewAndThreadedInsertHole058"
  Angle = 360
  Axis = (0,1,0)
  Base = (0,0,0)
  FaceMakerClass = Part::FaceMakerBullseye
  Placement = pos=(12.5,0,62) rot=(0,0,1;0rad)
  Solid = false
  Source = -> Face146
  Symmetric = false
FEATURE [Part::Revolution] Revolve151  label="removeToCreateScrewAndThreadedInsertHole059"
  Angle = 360
  Axis = (0,1,0)
  Base = (0,0,0)
  FaceMakerClass = Part::FaceMakerBullseye
  Placement = pos=(89.5,0,68.5) rot=(0,0,1;0rad)
  Solid = false
  Source = -> Face143
  Symmetric = false
FEATURE [Part::Revolution] Revolve152  label="removeToCreateScrewAndThreadedInsertHole060"
  Angle = 360
  Axis = (0,1,0)
  Base = (0,0,0)
  FaceMakerClass = Part::FaceMakerBullseye
  Placement = pos=(89.5,0,3.5) rot=(0,0,1;0rad)
  Solid = false
  Source = -> Face142
  Symmetric = false
FEATURE [Part::Revolution] Revolve153  label="removeToCreateScrewAndThreadedInsertHole061"
  Angle = 360
  Axis = (0,1,0)
  Base = (0,0,0)
  FaceMakerClass = Part::FaceMakerBullseye
  Placement = pos=(109.5,4.7,3.5) rot=(0,0,1;0rad)
  Solid = false
  Source = -> Face145
  Symmetric = false
FEATURE [Part::Revolution] Revolve154  label="removeToCreateScrewAndThreadedInsertHole062"
  Angle = 360
  Axis = (0,1,0)
  Base = (0,0,0)
  FaceMakerClass = Part::FaceMakerBullseye
  Placement = pos=(109.5,4.7,68.5) rot=(0,0,1;0rad)
  Solid = false
  Source = -> Face144
  Symmetric = false
FEATURE [Part::MultiFuse] Fusion115  label="removeToCreateScrewAndThreadedInsertHole056"
  Shapes = -> [Revolve154,Revolve153,Revolve152,Revolve151,Revolve150,Revolve149]
FEATURE [Part::Feature] Face147
  shape: bbox 9.8 x 26.5 x 2e-07 mm, 1 faces, 0 solids (baked)
FEATURE [Part::Revolution] Revolve155
  Angle = 360
  Axis = (0,1,0)
  Base = (0,0,0)
  FaceMakerClass = Part::FaceMakerBullseye
  Placement = pos=(0,0,0) rot=(0,0,1;1.5708rad)
  Solid = false
  Source = -> Face147
  Symmetric = false
FEATURE [Part::Feature] Face148
  shape: bbox 9.8 x 26.5 x 2e-07 mm, 1 faces, 0 solids (baked)
FEATURE [Part::Revolution] Revolve156
  Angle = 360
  Axis = (0,1,0)
  Base = (0,0,0)
  FaceMakerClass = Part::FaceMakerBullseye
  Placement = pos=(0,0,0) rot=(0,0,1;1.5708rad)
  Solid = false
  Source = -> Face148
  Symmetric = false
FEATURE [Part::MultiFuse] Fusion116
  Placement = pos=(-18,19,36) rot=(0,0,1;0rad)
  Shapes = -> [Revolve156,Revolve155]
FEATURE [Part::Box] Box029  label="Cube016"
  AttacherType = Attacher::AttachEngine3D
  Height = 28
  Length = 3
  Placement = pos=(110.7,19,22) rot=(0,0,1;0rad)
  Width = 15.7
FEATURE [Part::Cylinder] Cylinder046
  Angle = 360
  AttacherType = Attacher::AttachEngine3D
  Height = 10
  Placement = pos=(0,0,36.15) rot=(0,0,1;0rad)
  Radius = 4
FEATURE [Part::Cylinder] Cylinder047
  Angle = 360
  AttacherType = Attacher::AttachEngine3D
  Height = 20
  Placement = pos=(0,0,36.15) rot=(0,0,1;0rad)
  Radius = 10.3
FEATURE [Part::MultiFuse] Fusion117  label="removeToCreteHoleForPlugHousing041"
  Placement = pos=(70,19,36) rot=(0,1,0;1.5708rad)
  Shapes = -> [Cylinder047,Cylinder046]
FEATURE [Part::Cut] Cut049  label="plugHousingTab004"
  Base = -> Box029
  Placement = pos=(-107.4,-14,0) rot=(0,0,1;0rad)
  Tool = -> Fusion117
FEATURE [Part::Box] Box030  label="Cube017"
  AttacherType = Attacher::AttachEngine3D
  Height = 28
  Length = 3
  Placement = pos=(110.7,19,22) rot=(0,0,1;0rad)
  Width = 15.7
FEATURE [Part::Cylinder] Cylinder048
  Angle = 360
  AttacherType = Attacher::AttachEngine3D
  Height = 10
  Placement = pos=(0,0,36.15) rot=(0,0,1;0rad)
  Radius = 4
FEATURE [Part::Cylinder] Cylinder049
  Angle = 360
  AttacherType = Attacher::AttachEngine3D
  Height = 20
  Placement = pos=(0,0,36.15) rot=(0,0,1;0rad)
  Radius = 10.3
FEATURE [Part::MultiFuse] Fusion118  label="removeToCreteHoleForPlugHousing042"
  Placement = pos=(70,19,36) rot=(0,1,0;1.5708rad)
  Shapes = -> [Cylinder049,Cylinder048]
FEATURE [Part::Cut] Cut050  label="plugHousingTab005"
  Base = -> Box030
  Placement = pos=(-107.4,-14,0) rot=(0,0,1;0rad)
  Tool = -> Fusion118
FEATURE [Part::MultiFuse] Fusion119
  Placement = pos=(9.6,23,0) rot=(0,0,1;3.14159rad)
  Shapes = -> [Cut049,Cut050]
FEATURE [Part::Box] Box031  label="Cube018"
  AttacherType = Attacher::AttachEngine3D
  Height = 10
  Length = 3
  Placement = pos=(3.3,4,12) rot=(0,0,1;0rad)
  Width = 10
FEATURE [Part::Fillet] Fillet044
  Base = -> Box031
  Edges = 1 edges r=2: [Edge11]
FEATURE [Part::Box] Box032  label="Cube019"
  AttacherType = Attacher::AttachEngine3D
  Height = 10
  Length = 3
  Placement = pos=(3.3,4,50) rot=(0,0,1;0rad)
  Width = 10
FEATURE [Part::Fillet] Fillet045
  Base = -> Box032
  Edges = 1 edges r=2: [Edge12]
FEATURE [Part::Box] Box033  label="Cube020"
  AttacherType = Attacher::AttachEngine3D
  Height = 28
  Length = 4
  Placement = pos=(5,0,22) rot=(0,0,1;0rad)
  Width = 10
FEATURE [Part::Fillet] Fillet046
  Base = -> Box033
  Edges = 1 edges r=1: [Edge7]
FEATURE [Part::Fillet] Fillet047
  Base = -> Fillet046
  Edges = 1 edges r=2: [Edge5]
FEATURE [Part::Fillet] Fillet048
  Base = -> Fillet047
  Edges = 1 edges r=2: [Edge2]
FEATURE [Part::Cylinder] Cylinder050
  Angle = 360
  AttacherType = Attacher::AttachEngine3D
  Height = 20
  Placement = pos=(0,0,36.15) rot=(0,0,1;0rad)
  Radius = 8.2
FEATURE [Part::Cylinder] Cylinder051
  Angle = 360
  AttacherType = Attacher::AttachEngine3D
  Height = 10
  Placement = pos=(0,0,36.15) rot=(0,0,1;0rad)
  Radius = 4
FEATURE [Part::MultiFuse] Fusion120  label="removeToCreteHoleForPlugHousing043"
  Placement = pos=(-42,19,36) rot=(0,1,0;1.5708rad)
  Shapes = -> [Cylinder050,Cylinder051]
FEATURE [Sketcher::SketchObject] Sketch067  label="topSketch018"
  FullyConstrained = true
  sketch-geometry (4):
    g0: LineSegment StartX=16.8446 StartY=31.512 StartZ=0 EndX=16.3251 EndY=34.4666 EndZ=0
    g1: ArcOfCircle CenterX=19 CenterY=19.2524 CenterZ=0 NormalX=0 NormalY=0 NormalZ=1 AngleXU=0 Radius=15.4476 StartAngle=1.74483 EndAngle=2.72717
    g2: ArcOfCircle CenterX=19 CenterY=19.2524 CenterZ=0 NormalX=0 NormalY=0 NormalZ=1 AngleXU=0 Radius=12.4476 StartAngle=1.74483 EndAngle=2.73189
    g3: LineSegment StartX=4.86004 StartY=25.4725 StartZ=0 EndX=7.58253 EndY=24.2107 EndZ=0
  constraints (7):
    c: Block(g0)
    c: Coincident(g1,g0)
    c: Coincident(g2,g0)
    c: Coincident(g3,g1)
    c: Coincident(g3,g2)
    c: Block(g1)
    c: Block(g2)
FEATURE [Part::Extrusion] Extrude058
  Base = -> Sketch067
  Dir = (0,0,1)
  DirMode = 2
  FaceMakerClass = Part::FaceMakerBullseye
  LengthFwd = 10
  LengthRev = 0
  Placement = pos=(0,0,31) rot=(0,0,1;0rad)
  Solid = true
  Symmetric = false
FEATURE [Part::Cut] Cut051
  Base = -> Extrude058
  Tool = -> Fusion120
FEATURE [Part::Fillet] Fillet049
  Base = -> Cut051
  Edges = 1 edges r=2: [Edge1]
FEATURE [Part::Fillet] Fillet050
  Base = -> Fillet049
  Edges = 1 edges r=2.5: [Edge1]
FEATURE [Part::Fillet] Fillet051
  Base = -> Fillet050
  Edges = 1 edges r=2.5: [Edge2]
FEATURE [Part::MultiFuse] Fusion121  label="wireHolder003"
  Shapes = -> [Fusion116,Fillet051]
FEATURE [Part::MultiFuse] Fusion122
  Shapes = -> [Fillet045,Fusion121]
FEATURE [Part::MultiFuse] Fusion123  label="wireHolder004"
  Shapes = -> [Fusion122,Fillet048]
FEATURE [Part::MultiFuse] Fusion124  label="wireHolder005"
  Shapes = -> [Fillet044,Fusion119,Fusion123]
FEATURE [Part::MultiFuse] Fusion125  label="bottom012"
  Shapes = -> [Fillet037,Cut034]
FEATURE [Part::Cut] Cut052
  Base = -> Fusion125
  Tool = -> Fusion115
